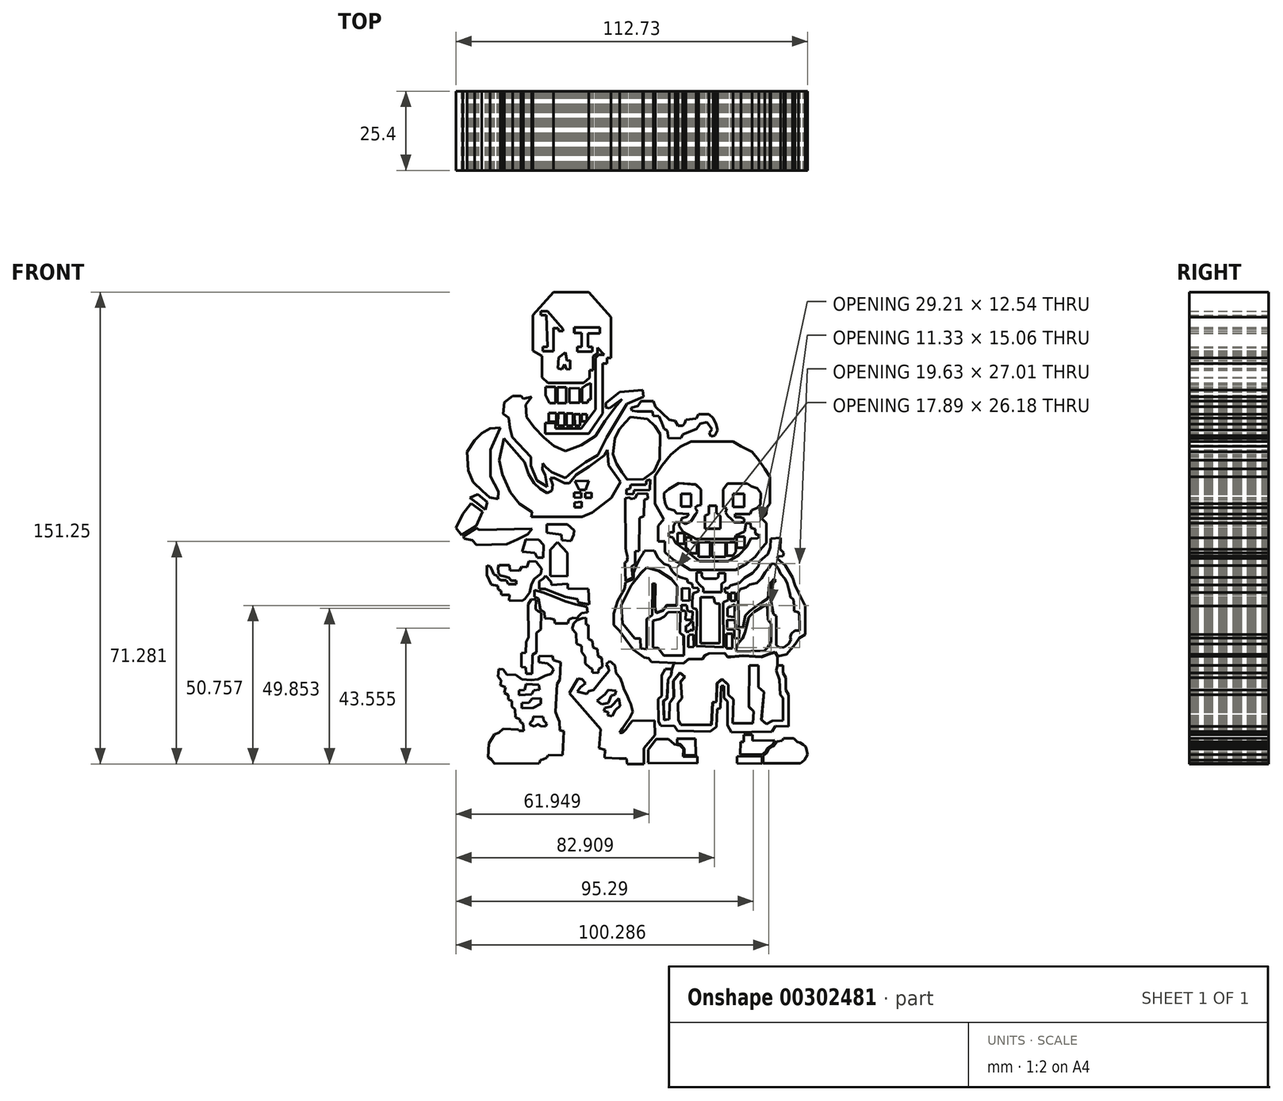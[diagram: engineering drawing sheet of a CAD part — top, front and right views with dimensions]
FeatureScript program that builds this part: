
annotation { "Feature Type Name" : "Feature", "Feature Type Description" : "" }
export const myFeature = defineFeature(function(context is Context, id is Id, definition is map)
    precondition{}
    {
        {
            var Q0;
            Q0=qCreatedBy(makeId("Front.planeOp"),FACE);
            var sketch = newSketch(context, id + "F0", { "sketchPlane" : qUnion([Q0])});
            skLineSegment(sketch, "E0", {"start": v(-16.69, 75) * mm, "end": v(-28, 75) * mm});
            skLineSegment(sketch, "E1", {"start": v(-28, 75) * mm, "end": v(-34.64, 67.58) * mm});
            skLineSegment(sketch, "E2", {"start": v(-34.64, 67.58) * mm, "end": v(-34.64, 56.21) * mm});
            skLineSegment(sketch, "E3", {"start": v(-34.64, 56.21) * mm, "end": v(-31.66, 54.56) * mm});
            skLineSegment(sketch, "E4", {"start": v(-31.66, 54.56) * mm, "end": v(-31.66, 47.68) * mm});
            skLineSegment(sketch, "E5", {"start": v(-31.66, 47.68) * mm, "end": v(-29.8, 45.82) * mm});
            skLineSegment(sketch, "E6", {"start": v(-29.8, 45.82) * mm, "end": v(-18.33, 45.82) * mm});
            skLineSegment(sketch, "E7", {"start": v(-18.33, 45.82) * mm, "end": v(-16.52, 47.56) * mm});
            skLineSegment(sketch, "E8", {"start": v(-16.52, 47.56) * mm, "end": v(-16.52, 49.98) * mm});
            skLineSegment(sketch, "E9", {"start": v(-16.52, 49.98) * mm, "end": v(-15.38, 49.98) * mm});
            skLineSegment(sketch, "E10", {"start": v(-15.38, 49.98) * mm, "end": v(-15.38, 54.44) * mm});
            skLineSegment(sketch, "E11", {"start": v(-15.38, 54.44) * mm, "end": v(-14.6, 54.44) * mm});
            skLineSegment(sketch, "E12", {"start": v(-14.6, 54.44) * mm, "end": v(-14.6, 37.31) * mm});
            skLineSegment(sketch, "E13", {"start": v(-14.6, 37.31) * mm, "end": v(-19.11, 31.33) * mm});
            skLineSegment(sketch, "E14", {"start": v(-19.11, 31.33) * mm, "end": v(-27.42, 31.33) * mm});
            skLineSegment(sketch, "E15", {"start": v(-27.42, 31.33) * mm, "end": v(-27.42, 32.99) * mm});
            skLineSegment(sketch, "E16", {"start": v(-27.42, 32.99) * mm, "end": v(-30.74, 32.99) * mm});
            skLineSegment(sketch, "E17", {"start": v(-30.74, 32.99) * mm, "end": v(-30.74, 29.66) * mm});
            skLineSegment(sketch, "E18", {"start": v(-30.74, 29.66) * mm, "end": v(-16.75, 29.66) * mm});
            skLineSegment(sketch, "E19", {"start": v(-16.75, 29.66) * mm, "end": v(-12.34, 36.12) * mm});
            skLineSegment(sketch, "E20", {"start": v(-12.34, 36.12) * mm, "end": v(-12.34, 52.15) * mm});
            skLineSegment(sketch, "E21", {"start": v(-12.34, 52.15) * mm, "end": v(-10.87, 52.15) * mm});
            skLineSegment(sketch, "E22", {"start": v(-10.87, 52.15) * mm, "end": v(-10.87, 53.88) * mm});
            skLineSegment(sketch, "E23", {"start": v(-10.87, 53.88) * mm, "end": v(-9.6, 53.88) * mm});
            skLineSegment(sketch, "E24", {"start": v(-9.6, 53.88) * mm, "end": v(-9.6, 66.91) * mm});
            skLineSegment(sketch, "E25", {"start": v(-9.6, 66.91) * mm, "end": v(-16.69, 75) * mm});
            skLineSegment(sketch, "E26", {"start": v(-29.94, 57.5) * mm, "end": v(-31.48, 57.5) * mm});
            skLineSegment(sketch, "E27", {"start": v(-31.48, 57.5) * mm, "end": v(-31.48, 56.06) * mm});
            skLineSegment(sketch, "E28", {"start": v(-31.48, 56.06) * mm, "end": v(-28.08, 56.06) * mm});
            skLineSegment(sketch, "E29", {"start": v(-28.08, 56.06) * mm, "end": v(-28.08, 63.46) * mm});
            skLineSegment(sketch, "E30", {"start": v(-28.08, 63.46) * mm, "end": v(-26.52, 63.46) * mm});
            skLineSegment(sketch, "E31", {"start": v(-26.52, 63.46) * mm, "end": v(-26.44, 62.47) * mm});
            skLineSegment(sketch, "E32", {"start": v(-26.44, 62.47) * mm, "end": v(-24.97, 62.47) * mm});
            skLineSegment(sketch, "E33", {"start": v(-24.97, 62.47) * mm, "end": v(-24.97, 63.1) * mm});
            skLineSegment(sketch, "E34", {"start": v(-24.97, 63.1) * mm, "end": v(-29.96, 68.9) * mm});
            skLineSegment(sketch, "E35", {"start": v(-29.96, 68.9) * mm, "end": v(-32.1, 68.9) * mm});
            skLineSegment(sketch, "E36", {"start": v(-32.1, 68.9) * mm, "end": v(-32.1, 67.6) * mm});
            skLineSegment(sketch, "E37", {"start": v(-32.1, 67.6) * mm, "end": v(-30.3, 67.6) * mm});
            skLineSegment(sketch, "E38", {"start": v(-30.3, 67.6) * mm, "end": v(-29.94, 57.5) * mm});
            skLineSegment(sketch, "E39", {"start": v(-21.37, 63.41) * mm, "end": v(-21.37, 61.88) * mm});
            skLineSegment(sketch, "E40", {"start": v(-21.37, 61.88) * mm, "end": v(-19.04, 61.88) * mm});
            skLineSegment(sketch, "E41", {"start": v(-19.04, 61.88) * mm, "end": v(-19.04, 57.4) * mm});
            skLineSegment(sketch, "E42", {"start": v(-19.04, 57.4) * mm, "end": v(-20.43, 57.4) * mm});
            skLineSegment(sketch, "E43", {"start": v(-20.43, 57.4) * mm, "end": v(-20.43, 55.93) * mm});
            skLineSegment(sketch, "E44", {"start": v(-20.43, 55.93) * mm, "end": v(-15.62, 55.93) * mm});
            skLineSegment(sketch, "E45", {"start": v(-15.62, 55.93) * mm, "end": v(-15.62, 57.47) * mm});
            skLineSegment(sketch, "E46", {"start": v(-15.62, 57.47) * mm, "end": v(-16.99, 57.47) * mm});
            skLineSegment(sketch, "E47", {"start": v(-16.99, 57.47) * mm, "end": v(-16.99, 61.76) * mm});
            skLineSegment(sketch, "E48", {"start": v(-16.99, 61.76) * mm, "end": v(-13.12, 61.76) * mm});
            skLineSegment(sketch, "E49", {"start": v(-13.12, 61.76) * mm, "end": v(-13.12, 63.61) * mm});
            skLineSegment(sketch, "E50", {"start": v(-13.12, 63.61) * mm, "end": v(-21.37, 63.61) * mm});
            skLineSegment(sketch, "E51", {"start": v(-21.37, 63.61) * mm, "end": v(-21.37, 63.41) * mm});
            skLineSegment(sketch, "E52", {"start": v(-24.17, 55.7) * mm, "end": v(-23.76, 52.96) * mm});
            skLineSegment(sketch, "E53", {"start": v(-23.76, 52.96) * mm, "end": v(-22.73, 53.11) * mm});
            skLineSegment(sketch, "E54", {"start": v(-22.73, 53.11) * mm, "end": v(-22.73, 50.35) * mm});
            skLineSegment(sketch, "E55", {"start": v(-22.73, 50.35) * mm, "end": v(-23.86, 50.22) * mm});
            skLineSegment(sketch, "E56", {"start": v(-23.86, 50.22) * mm, "end": v(-24.5, 51.88) * mm});
            skLineSegment(sketch, "E57", {"start": v(-24.5, 51.88) * mm, "end": v(-25.32, 50.18) * mm});
            skLineSegment(sketch, "E58", {"start": v(-25.32, 50.18) * mm, "end": v(-26.67, 50.56) * mm});
            skLineSegment(sketch, "E59", {"start": v(-26.67, 50.56) * mm, "end": v(-26.33, 54.04) * mm});
            skLineSegment(sketch, "E60", {"start": v(-26.33, 54.04) * mm, "end": v(-24.17, 55.7) * mm});
            skLineSegment(sketch, "E61", {"start": v(-13.91, 57.13) * mm, "end": v(-13.91, 54.9) * mm});
            skLineSegment(sketch, "E62", {"start": v(-13.91, 54.9) * mm, "end": v(-11.83, 54.86) * mm});
            skLineSegment(sketch, "E63", {"start": v(-11.83, 54.86) * mm, "end": v(-13.91, 57.13) * mm});
            skLineSegment(sketch, "E64", {"start": v(-15.38, 54.44) * mm, "end": v(-13.91, 55.31) * mm});
            skLineSegment(sketch, "E65", {"start": v(-13.91, 55.31) * mm, "end": v(-13.91, 54.9) * mm});
            skLineSegment(sketch, "E66", {"start": v(-14.6, 53.9) * mm, "end": v(-13.52, 54.89) * mm});
            skLineSegment(sketch, "E67", {"start": v(-13.52, 54.89) * mm, "end": v(-13.91, 54.9) * mm});
            skLineSegment(sketch, "E68", {"start": v(-30.64, 44.3) * mm, "end": v(-30.64, 41.9) * mm});
            skLineSegment(sketch, "E69", {"start": v(-30.64, 41.9) * mm, "end": v(-29.36, 39.43) * mm});
            skLineSegment(sketch, "E70", {"start": v(-29.36, 39.43) * mm, "end": v(-27.4, 39.43) * mm});
            skLineSegment(sketch, "E71", {"start": v(-27.4, 39.43) * mm, "end": v(-27.4, 44.55) * mm});
            skLineSegment(sketch, "E72", {"start": v(-27.4, 44.55) * mm, "end": v(-30.64, 44.55) * mm});
            skLineSegment(sketch, "E73", {"start": v(-30.64, 44.55) * mm, "end": v(-30.64, 44.3) * mm});
            skLineSegment(sketch, "E74", {"start": v(-26.73, 44.47) * mm, "end": v(-26.73, 39.36) * mm});
            skLineSegment(sketch, "E75", {"start": v(-26.73, 39.36) * mm, "end": v(-23.91, 39.36) * mm});
            skLineSegment(sketch, "E76", {"start": v(-23.91, 39.36) * mm, "end": v(-23.91, 44.44) * mm});
            skLineSegment(sketch, "E77", {"start": v(-23.91, 44.44) * mm, "end": v(-26.73, 44.47) * mm});
            skLineSegment(sketch, "E78", {"start": v(-22.96, 44.18) * mm, "end": v(-22.96, 39.55) * mm});
            skLineSegment(sketch, "E79", {"start": v(-22.96, 39.55) * mm, "end": v(-19.7, 39.55) * mm});
            skLineSegment(sketch, "E80", {"start": v(-19.7, 39.55) * mm, "end": v(-19.7, 44.15) * mm});
            skLineSegment(sketch, "E81", {"start": v(-19.7, 44.15) * mm, "end": v(-22.96, 44.18) * mm});
            skLineSegment(sketch, "E82", {"start": v(-18.87, 44.28) * mm, "end": v(-18.87, 39.55) * mm});
            skLineSegment(sketch, "E83", {"start": v(-18.87, 39.55) * mm, "end": v(-17.17, 39.55) * mm});
            skLineSegment(sketch, "E84", {"start": v(-17.17, 39.55) * mm, "end": v(-16.82, 40.54) * mm});
            skLineSegment(sketch, "E85", {"start": v(-16.82, 40.54) * mm, "end": v(-16.15, 40.54) * mm});
            skLineSegment(sketch, "E86", {"start": v(-16.15, 40.54) * mm, "end": v(-16.15, 45.78) * mm});
            skLineSegment(sketch, "E87", {"start": v(-16.15, 45.78) * mm, "end": v(-17.5, 45.27) * mm});
            skLineSegment(sketch, "E88", {"start": v(-17.5, 45.27) * mm, "end": v(-18.87, 44.28) * mm});
            skLineSegment(sketch, "E89", {"start": v(-29.52, 33.48) * mm, "end": v(-29.52, 36.2) * mm});
            skLineSegment(sketch, "E90", {"start": v(-29.52, 36.2) * mm, "end": v(-27.18, 36.2) * mm});
            skLineSegment(sketch, "E91", {"start": v(-27.18, 36.2) * mm, "end": v(-27.18, 33.48) * mm});
            skLineSegment(sketch, "E92", {"start": v(-27.18, 33.48) * mm, "end": v(-29.52, 33.48) * mm});
            skLineSegment(sketch, "E93", {"start": v(-26.62, 32.2) * mm, "end": v(-24.53, 32.2) * mm});
            skLineSegment(sketch, "E94", {"start": v(-24.53, 32.2) * mm, "end": v(-24.53, 36.2) * mm});
            skLineSegment(sketch, "E95", {"start": v(-24.53, 36.2) * mm, "end": v(-26.54, 36.2) * mm});
            skLineSegment(sketch, "E96", {"start": v(-26.54, 36.2) * mm, "end": v(-26.62, 32.2) * mm});
            skLineSegment(sketch, "E97", {"start": v(-23.9, 32.2) * mm, "end": v(-21.85, 32.2) * mm});
            skLineSegment(sketch, "E98", {"start": v(-21.85, 32.2) * mm, "end": v(-21.85, 36.03) * mm});
            skLineSegment(sketch, "E99", {"start": v(-21.85, 36.03) * mm, "end": v(-23.85, 36.03) * mm});
            skLineSegment(sketch, "E100", {"start": v(-23.85, 36.03) * mm, "end": v(-23.9, 32.2) * mm});
            skLineSegment(sketch, "E101", {"start": v(-21.17, 32.15) * mm, "end": v(-19.55, 32.15) * mm});
            skLineSegment(sketch, "E102", {"start": v(-19.55, 32.15) * mm, "end": v(-19.55, 35.86) * mm});
            skLineSegment(sketch, "E103", {"start": v(-19.55, 35.86) * mm, "end": v(-21.25, 35.86) * mm});
            skLineSegment(sketch, "E104", {"start": v(-21.25, 35.86) * mm, "end": v(-21.17, 32.15) * mm});
            skLineSegment(sketch, "E105", {"start": v(-19.03, 35.57) * mm, "end": v(-19.03, 33.6) * mm});
            skLineSegment(sketch, "E106", {"start": v(-19.03, 33.6) * mm, "end": v(-17.4, 33.6) * mm});
            skLineSegment(sketch, "E107", {"start": v(-17.4, 33.6) * mm, "end": v(-17.4, 35.86) * mm});
            skLineSegment(sketch, "E108", {"start": v(-17.4, 35.86) * mm, "end": v(-19.03, 35.86) * mm});
            skLineSegment(sketch, "E109", {"start": v(-19.03, 35.86) * mm, "end": v(-19.03, 35.57) * mm});
            skLineSegment(sketch, "E110", {"start": v(-35.03, 41.37) * mm, "end": v(-36.94, 38.85) * mm});
            skLineSegment(sketch, "E111", {"start": v(-36.94, 38.85) * mm, "end": v(-36.63, 34.91) * mm});
            skLineSegment(sketch, "E112", {"start": v(-36.63, 34.91) * mm, "end": v(-34.2, 31.65) * mm});
            skLineSegment(sketch, "E113", {"start": v(-34.2, 31.65) * mm, "end": v(-31.08, 28.3) * mm});
            skLineSegment(sketch, "E114", {"start": v(-31.08, 28.3) * mm, "end": v(-27.97, 25.64) * mm});
            skLineSegment(sketch, "E115", {"start": v(-27.97, 25.64) * mm, "end": v(-24.17, 24.05) * mm});
            skLineSegment(sketch, "E116", {"start": v(-24.17, 24.05) * mm, "end": v(-19.15, 25.87) * mm});
            skLineSegment(sketch, "E117", {"start": v(-19.15, 25.87) * mm, "end": v(-14.52, 28.83) * mm});
            skLineSegment(sketch, "E118", {"start": v(-14.52, 28.83) * mm, "end": v(-11.48, 33.7) * mm});
            skLineSegment(sketch, "E119", {"start": v(-11.48, 33.7) * mm, "end": v(-7.76, 38.71) * mm});
            skLineSegment(sketch, "E120", {"start": v(-7.76, 38.71) * mm, "end": v(-6.09, 40.61) * mm});
            skLineSegment(sketch, "E121", {"start": v(-6.09, 40.61) * mm, "end": v(-10.11, 37.72) * mm});
            skLineSegment(sketch, "E122", {"start": v(-10.11, 37.72) * mm, "end": v(-11.33, 38.03) * mm});
            skLineSegment(sketch, "E123", {"start": v(-11.33, 38.03) * mm, "end": v(-11.33, 39.4) * mm});
            skLineSegment(sketch, "E124", {"start": v(-11.33, 39.4) * mm, "end": v(-6.85, 42.97) * mm});
            skLineSegment(sketch, "E125", {"start": v(-6.85, 42.97) * mm, "end": v(0.6, 43.57) * mm});
            skLineSegment(sketch, "E126", {"start": v(0.6, 43.57) * mm, "end": v(0.77, 41.46) * mm});
            skLineSegment(sketch, "E127", {"start": v(0.77, 41.46) * mm, "end": v(-4.5, 39.1) * mm});
            skLineSegment(sketch, "E128", {"start": v(-4.5, 39.1) * mm, "end": v(-10.96, 28.4) * mm});
            skLineSegment(sketch, "E129", {"start": v(-10.96, 28.4) * mm, "end": v(-13.86, 22.7) * mm});
            skLineSegment(sketch, "E130", {"start": v(-13.86, 22.7) * mm, "end": v(-17.73, 20.45) * mm});
            skLineSegment(sketch, "E131", {"start": v(-17.73, 20.45) * mm, "end": v(-21.97, 17.44) * mm});
            skLineSegment(sketch, "E132", {"start": v(-21.97, 17.44) * mm, "end": v(-24.18, 15.4) * mm});
            skLineSegment(sketch, "E133", {"start": v(-24.18, 15.4) * mm, "end": v(-28.69, 17.33) * mm});
            skLineSegment(sketch, "E134", {"start": v(-28.69, 17.33) * mm, "end": v(-30.62, 18.95) * mm});
            skLineSegment(sketch, "E135", {"start": v(-30.62, 18.95) * mm, "end": v(-31.43, 20.08) * mm});
            skLineSegment(sketch, "E136", {"start": v(-31.43, 20.08) * mm, "end": v(-31.55, 18.1) * mm});
            skLineSegment(sketch, "E137", {"start": v(-31.55, 18.1) * mm, "end": v(-30.65, 16.38) * mm});
            skLineSegment(sketch, "E138", {"start": v(-30.65, 16.38) * mm, "end": v(-30.1, 12.59) * mm});
            skLineSegment(sketch, "E139", {"start": v(-30.1, 12.59) * mm, "end": v(-33.36, 14.66) * mm});
            skLineSegment(sketch, "E140", {"start": v(-33.36, 14.66) * mm, "end": v(-35.26, 19.36) * mm});
            skLineSegment(sketch, "E141", {"start": v(-35.26, 19.36) * mm, "end": v(-35.26, 22.16) * mm});
            skLineSegment(sketch, "E142", {"start": v(-35.26, 22.16) * mm, "end": v(-41.3, 28.49) * mm});
            skLineSegment(sketch, "E143", {"start": v(-41.3, 28.49) * mm, "end": v(-42.03, 31.47) * mm});
            skLineSegment(sketch, "E144", {"start": v(-42.03, 31.47) * mm, "end": v(-42.4, 34.72) * mm});
            skLineSegment(sketch, "E145", {"start": v(-42.4, 34.72) * mm, "end": v(-44.2, 35.99) * mm});
            skLineSegment(sketch, "E146", {"start": v(-44.2, 35.99) * mm, "end": v(-43.75, 39.6) * mm});
            skLineSegment(sketch, "E147", {"start": v(-43.75, 39.6) * mm, "end": v(-41.13, 41.68) * mm});
            skLineSegment(sketch, "E148", {"start": v(-41.13, 41.68) * mm, "end": v(-38.42, 41.68) * mm});
            skLineSegment(sketch, "E149", {"start": v(-38.42, 41.68) * mm, "end": v(-37.7, 40.78) * mm});
            skLineSegment(sketch, "E150", {"start": v(-37.7, 40.78) * mm, "end": v(-35.03, 41.37) * mm});
            skLineSegment(sketch, "E151", {"start": v(-3.09, 37.93) * mm, "end": v(-0.94, 38.5) * mm});
            skLineSegment(sketch, "E152", {"start": v(-0.94, 38.5) * mm, "end": v(0, 40.09) * mm});
            skLineSegment(sketch, "E153", {"start": v(0, 40.09) * mm, "end": v(3.94, 40.09) * mm});
            skLineSegment(sketch, "E154", {"start": v(3.94, 40.09) * mm, "end": v(4.66, 38.3) * mm});
            skLineSegment(sketch, "E155", {"start": v(4.66, 38.3) * mm, "end": v(9.1, 34.06) * mm});
            skLineSegment(sketch, "E156", {"start": v(9.1, 34.06) * mm, "end": v(10.9, 33.7) * mm});
            skLineSegment(sketch, "E157", {"start": v(10.9, 33.7) * mm, "end": v(11.83, 32.13) * mm});
            skLineSegment(sketch, "E158", {"start": v(11.83, 32.13) * mm, "end": v(13.4, 32.2) * mm});
            skLineSegment(sketch, "E159", {"start": v(13.4, 32.2) * mm, "end": v(13.98, 32.91) * mm});
            skLineSegment(sketch, "E160", {"start": v(13.98, 32.91) * mm, "end": v(14.4, 34.06) * mm});
            skLineSegment(sketch, "E161", {"start": v(14.4, 34.06) * mm, "end": v(17.64, 34.42) * mm});
            skLineSegment(sketch, "E162", {"start": v(17.64, 34.42) * mm, "end": v(18.5, 35.78) * mm});
            skLineSegment(sketch, "E163", {"start": v(18.5, 35.78) * mm, "end": v(21.72, 35.78) * mm});
            skLineSegment(sketch, "E164", {"start": v(21.72, 35.78) * mm, "end": v(23.09, 34.56) * mm});
            skLineSegment(sketch, "E165", {"start": v(23.09, 34.56) * mm, "end": v(24.02, 32.63) * mm});
            skLineSegment(sketch, "E166", {"start": v(24.02, 32.63) * mm, "end": v(24.6, 30.76) * mm});
            skLineSegment(sketch, "E167", {"start": v(24.6, 30.76) * mm, "end": v(23.66, 29.04) * mm});
            skLineSegment(sketch, "E168", {"start": v(23.66, 29.04) * mm, "end": v(22.44, 28.76) * mm});
            skLineSegment(sketch, "E169", {"start": v(22.44, 28.76) * mm, "end": v(21.87, 29.83) * mm});
            skLineSegment(sketch, "E170", {"start": v(21.87, 29.83) * mm, "end": v(22.73, 31.05) * mm});
            skLineSegment(sketch, "E171", {"start": v(22.73, 31.05) * mm, "end": v(21.15, 33.34) * mm});
            skLineSegment(sketch, "E172", {"start": v(21.15, 33.34) * mm, "end": v(19, 32.77) * mm});
            skLineSegment(sketch, "E173", {"start": v(19, 32.77) * mm, "end": v(17.78, 31.2) * mm});
            skLineSegment(sketch, "E174", {"start": v(17.78, 31.2) * mm, "end": v(15.05, 30.05) * mm});
            skLineSegment(sketch, "E175", {"start": v(15.05, 30.05) * mm, "end": v(13.4, 29.33) * mm});
            skLineSegment(sketch, "E176", {"start": v(13.4, 29.33) * mm, "end": v(12.83, 28.25) * mm});
            skLineSegment(sketch, "E177", {"start": v(12.83, 28.25) * mm, "end": v(8.81, 28.04) * mm});
            skLineSegment(sketch, "E178", {"start": v(8.81, 28.04) * mm, "end": v(8.38, 30.62) * mm});
            skLineSegment(sketch, "E179", {"start": v(8.38, 30.62) * mm, "end": v(7.38, 31.2) * mm});
            skLineSegment(sketch, "E180", {"start": v(7.38, 31.2) * mm, "end": v(6.66, 33.2) * mm});
            skLineSegment(sketch, "E181", {"start": v(6.66, 33.2) * mm, "end": v(5.8, 35.2) * mm});
            skLineSegment(sketch, "E182", {"start": v(5.8, 35.2) * mm, "end": v(3.87, 35.35) * mm});
            skLineSegment(sketch, "E183", {"start": v(3.87, 35.35) * mm, "end": v(3.72, 36.79) * mm});
            skLineSegment(sketch, "E184", {"start": v(3.72, 36.79) * mm, "end": v(-1.22, 36.79) * mm});
            skLineSegment(sketch, "E185", {"start": v(-1.22, 36.79) * mm, "end": v(-2.95, 36.93) * mm});
            skLineSegment(sketch, "E186", {"start": v(-2.95, 36.93) * mm, "end": v(-3.16, 37.8) * mm});
            skLineSegment(sketch, "E187", {"start": v(-3.16, 37.8) * mm, "end": v(-3.09, 37.93) * mm});
            skLineSegment(sketch, "E188", {"start": v(-3.09, 35.2) * mm, "end": v(-5.01, 33.2) * mm});
            skLineSegment(sketch, "E189", {"start": v(-5.01, 33.2) * mm, "end": v(-6.77, 31.12) * mm});
            skLineSegment(sketch, "E190", {"start": v(-6.77, 31.12) * mm, "end": v(-8.4, 28.28) * mm});
            skLineSegment(sketch, "E191", {"start": v(-8.4, 28.28) * mm, "end": v(-8.94, 23) * mm});
            skLineSegment(sketch, "E192", {"start": v(-8.94, 23) * mm, "end": v(-7.85, 20.02) * mm});
            skLineSegment(sketch, "E193", {"start": v(-7.85, 20.02) * mm, "end": v(-6.1, 17.1) * mm});
            skLineSegment(sketch, "E194", {"start": v(-6.1, 17.1) * mm, "end": v(-4.47, 14.87) * mm});
            skLineSegment(sketch, "E195", {"start": v(-4.47, 14.87) * mm, "end": v(0.81, 15.01) * mm});
            skLineSegment(sketch, "E196", {"start": v(0.81, 15.01) * mm, "end": v(4.2, 17.58) * mm});
            skLineSegment(sketch, "E197", {"start": v(4.2, 17.58) * mm, "end": v(5.95, 21.5) * mm});
            skLineSegment(sketch, "E198", {"start": v(5.95, 21.5) * mm, "end": v(6.1, 29.43) * mm});
            skLineSegment(sketch, "E199", {"start": v(6.1, 29.43) * mm, "end": v(4.53, 32.07) * mm});
            skLineSegment(sketch, "E200", {"start": v(4.53, 32.07) * mm, "end": v(2.03, 34.37) * mm});
            skLineSegment(sketch, "E201", {"start": v(2.03, 34.37) * mm, "end": v(-3.38, 34.9) * mm});
            skLineSegment(sketch, "E202", {"start": v(-3.38, 34.9) * mm, "end": v(-5.01, 33.2) * mm});
            skLineSegment(sketch, "E203", {"start": v(-43.86, 28.08) * mm, "end": v(-37.36, 20.49) * mm});
            skLineSegment(sketch, "E204", {"start": v(-37.36, 20.49) * mm, "end": v(-36.1, 16.7) * mm});
            skLineSegment(sketch, "E205", {"start": v(-36.1, 16.7) * mm, "end": v(-34.29, 13.8) * mm});
            skLineSegment(sketch, "E206", {"start": v(-34.29, 13.8) * mm, "end": v(-32.3, 12) * mm});
            skLineSegment(sketch, "E207", {"start": v(-32.3, 12) * mm, "end": v(-30.13, 10.55) * mm});
            skLineSegment(sketch, "E208", {"start": v(-30.13, 10.55) * mm, "end": v(-28.6, 11.27) * mm});
            skLineSegment(sketch, "E209", {"start": v(-28.6, 11.27) * mm, "end": v(-28.32, 13.26) * mm});
            skLineSegment(sketch, "E210", {"start": v(-28.32, 13.26) * mm, "end": v(-29.05, 15.34) * mm});
            skLineSegment(sketch, "E211", {"start": v(-29.05, 15.34) * mm, "end": v(-27.78, 15.34) * mm});
            skLineSegment(sketch, "E212", {"start": v(-27.78, 15.34) * mm, "end": v(-24.53, 13.7) * mm});
            skLineSegment(sketch, "E213", {"start": v(-24.53, 13.7) * mm, "end": v(-23, 13.7) * mm});
            skLineSegment(sketch, "E214", {"start": v(-23, 13.7) * mm, "end": v(-20.82, 16.42) * mm});
            skLineSegment(sketch, "E215", {"start": v(-20.82, 16.42) * mm, "end": v(-16.67, 19.13) * mm});
            skLineSegment(sketch, "E216", {"start": v(-16.67, 19.13) * mm, "end": v(-11.79, 22.65) * mm});
            skLineSegment(sketch, "E217", {"start": v(-11.79, 22.65) * mm, "end": v(-10.8, 24.37) * mm});
            skLineSegment(sketch, "E218", {"start": v(-10.8, 24.37) * mm, "end": v(-10.43, 19.4) * mm});
            skLineSegment(sketch, "E219", {"start": v(-10.43, 19.4) * mm, "end": v(-6.55, 14.16) * mm});
            skLineSegment(sketch, "E220", {"start": v(-6.55, 14.16) * mm, "end": v(-9.53, 9.1) * mm});
            skLineSegment(sketch, "E221", {"start": v(-9.53, 9.1) * mm, "end": v(-15.65, 4.36) * mm});
            skLineSegment(sketch, "E222", {"start": v(-15.65, 4.36) * mm, "end": v(-18.9, 2.9) * mm});
            skLineSegment(sketch, "E223", {"start": v(-18.9, 2.9) * mm, "end": v(-35.1, 2.9) * mm});
            skLineSegment(sketch, "E224", {"start": v(-35.1, 2.9) * mm, "end": v(-34.92, 4.53) * mm});
            skLineSegment(sketch, "E225", {"start": v(-34.92, 4.53) * mm, "end": v(-39.02, 7.09) * mm});
            skLineSegment(sketch, "E226", {"start": v(-39.02, 7.09) * mm, "end": v(-41.92, 10.84) * mm});
            skLineSegment(sketch, "E227", {"start": v(-41.92, 10.84) * mm, "end": v(-44.47, 16.55) * mm});
            skLineSegment(sketch, "E228", {"start": v(-44.47, 16.55) * mm, "end": v(-45.5, 21.07) * mm});
            skLineSegment(sketch, "E229", {"start": v(-45.5, 21.07) * mm, "end": v(-43.86, 28.08) * mm});
            skLineSegment(sketch, "E230", {"start": v(-20.94, 13.9) * mm, "end": v(-19.74, 11.6) * mm});
            skLineSegment(sketch, "E231", {"start": v(-19.74, 11.6) * mm, "end": v(-17.78, 11.6) * mm});
            skLineSegment(sketch, "E232", {"start": v(-17.78, 11.6) * mm, "end": v(-16.67, 14.5) * mm});
            skLineSegment(sketch, "E233", {"start": v(-16.67, 14.5) * mm, "end": v(-21.2, 14.42) * mm});
            skLineSegment(sketch, "E234", {"start": v(-21.2, 14.42) * mm, "end": v(-20.94, 13.9) * mm});
            skLineSegment(sketch, "E235", {"start": v(-21.4, 10.65) * mm, "end": v(-21.4, 9.15) * mm});
            skLineSegment(sketch, "E236", {"start": v(-21.4, 9.15) * mm, "end": v(-19.16, 9) * mm});
            skLineSegment(sketch, "E237", {"start": v(-19.16, 9) * mm, "end": v(-19.16, 10.65) * mm});
            skLineSegment(sketch, "E238", {"start": v(-19.16, 10.65) * mm, "end": v(-21.4, 10.65) * mm});
            skLineSegment(sketch, "E239", {"start": v(-17.82, 10.59) * mm, "end": v(-17.82, 9.05) * mm});
            skLineSegment(sketch, "E240", {"start": v(-17.82, 9.05) * mm, "end": v(-15.9, 9.05) * mm});
            skLineSegment(sketch, "E241", {"start": v(-15.9, 9.05) * mm, "end": v(-15.9, 10.65) * mm});
            skLineSegment(sketch, "E242", {"start": v(-15.9, 10.65) * mm, "end": v(-17.82, 10.59) * mm});
            skLineSegment(sketch, "E243", {"start": v(-21.27, 7.52) * mm, "end": v(-21.27, 5.96) * mm});
            skLineSegment(sketch, "E244", {"start": v(-21.27, 5.96) * mm, "end": v(-18.97, 5.96) * mm});
            skLineSegment(sketch, "E245", {"start": v(-18.97, 5.96) * mm, "end": v(-18.97, 7.71) * mm});
            skLineSegment(sketch, "E246", {"start": v(-18.97, 7.71) * mm, "end": v(-21.27, 7.52) * mm});
            skLineSegment(sketch, "E247", {"start": v(-45.15, 31.32) * mm, "end": v(-48.21, 24.4) * mm});
            skLineSegment(sketch, "E248", {"start": v(-48.21, 24.4) * mm, "end": v(-48.21, 15.87) * mm});
            skLineSegment(sketch, "E249", {"start": v(-48.21, 15.87) * mm, "end": v(-45.64, 11.04) * mm});
            skLineSegment(sketch, "E250", {"start": v(-45.64, 11.04) * mm, "end": v(-45.8, 8.63) * mm});
            skLineSegment(sketch, "E251", {"start": v(-45.8, 8.63) * mm, "end": v(-48.53, 9.1) * mm});
            skLineSegment(sketch, "E252", {"start": v(-48.53, 9.1) * mm, "end": v(-50.79, 11.2) * mm});
            skLineSegment(sketch, "E253", {"start": v(-50.79, 11.2) * mm, "end": v(-53.85, 14.1) * mm});
            skLineSegment(sketch, "E254", {"start": v(-53.85, 14.1) * mm, "end": v(-55.38, 17.8) * mm});
            skLineSegment(sketch, "E255", {"start": v(-55.38, 17.8) * mm, "end": v(-55.7, 23.76) * mm});
            skLineSegment(sketch, "E256", {"start": v(-55.7, 23.76) * mm, "end": v(-53.35, 27.5) * mm});
            skLineSegment(sketch, "E257", {"start": v(-53.35, 27.5) * mm, "end": v(-50.97, 29.74) * mm});
            skLineSegment(sketch, "E258", {"start": v(-50.97, 29.74) * mm, "end": v(-48.4, 31.3) * mm});
            skLineSegment(sketch, "E259", {"start": v(-48.4, 31.3) * mm, "end": v(-45, 31.49) * mm});
            skLineSegment(sketch, "E260", {"start": v(-45, 31.49) * mm, "end": v(-45.15, 31.32) * mm});
            skLineSegment(sketch, "E261", {"start": v(-54.84, 9.08) * mm, "end": v(-52.57, 7.43) * mm});
            skLineSegment(sketch, "E262", {"start": v(-52.57, 7.43) * mm, "end": v(-49.9, 5.21) * mm});
            skLineSegment(sketch, "E263", {"start": v(-49.9, 5.21) * mm, "end": v(-49.27, 7.6) * mm});
            skLineSegment(sketch, "E264", {"start": v(-49.27, 7.6) * mm, "end": v(-52.34, 10.17) * mm});
            skLineSegment(sketch, "E265", {"start": v(-52.34, 10.17) * mm, "end": v(-54.84, 9.08) * mm});
            skLineSegment(sketch, "E266", {"start": v(-54.44, 7.23) * mm, "end": v(-50.8, 4.6) * mm});
            skLineSegment(sketch, "E267", {"start": v(-50.8, 4.6) * mm, "end": v(-52.83, 0) * mm});
            skLineSegment(sketch, "E268", {"start": v(-52.83, 0) * mm, "end": v(-57.45, -2.87) * mm});
            skLineSegment(sketch, "E269", {"start": v(-57.45, -2.87) * mm, "end": v(-59.33, -0.67) * mm});
            skLineSegment(sketch, "E270", {"start": v(-59.33, -0.67) * mm, "end": v(-57.13, 3.8) * mm});
            skLineSegment(sketch, "E271", {"start": v(-57.13, 3.8) * mm, "end": v(-54.44, 7.23) * mm});
            skLineSegment(sketch, "E272", {"start": v(-56.92, -3.3) * mm, "end": v(-52.62, -0.61) * mm});
            skLineSegment(sketch, "E273", {"start": v(-52.62, -0.61) * mm, "end": v(-51.87, -1.26) * mm});
            skLineSegment(sketch, "E274", {"start": v(-51.87, -1.26) * mm, "end": v(-34.89, -0.83) * mm});
            skLineSegment(sketch, "E275", {"start": v(-34.89, -0.83) * mm, "end": v(-36.23, -2.66) * mm});
            skLineSegment(sketch, "E276", {"start": v(-36.23, -2.66) * mm, "end": v(-39.56, -4.27) * mm});
            skLineSegment(sketch, "E277", {"start": v(-39.56, -4.27) * mm, "end": v(-43.05, -5.88) * mm});
            skLineSegment(sketch, "E278", {"start": v(-43.05, -5.88) * mm, "end": v(-52.62, -6.1) * mm});
            skLineSegment(sketch, "E279", {"start": v(-52.62, -6.1) * mm, "end": v(-54.07, -4.48) * mm});
            skLineSegment(sketch, "E280", {"start": v(-54.07, -4.48) * mm, "end": v(-56.65, -4.05) * mm});
            skLineSegment(sketch, "E281", {"start": v(-56.65, -4.05) * mm, "end": v(-56.92, -3.3) * mm});
            skLineSegment(sketch, "E282", {"start": v(-36.96, -4.31) * mm, "end": v(-38, -8.25) * mm});
            skLineSegment(sketch, "E283", {"start": v(-38, -8.25) * mm, "end": v(-33.98, -8.58) * mm});
            skLineSegment(sketch, "E284", {"start": v(-33.98, -8.58) * mm, "end": v(-33.26, -10.19) * mm});
            skLineSegment(sketch, "E285", {"start": v(-33.26, -10.19) * mm, "end": v(-31.33, -10.19) * mm});
            skLineSegment(sketch, "E286", {"start": v(-31.33, -10.19) * mm, "end": v(-31.25, -6.08) * mm});
            skLineSegment(sketch, "E287", {"start": v(-31.25, -6.08) * mm, "end": v(-32.7, -4.47) * mm});
            skLineSegment(sketch, "E288", {"start": v(-32.7, -4.47) * mm, "end": v(-36.8, -4.31) * mm});
            skLineSegment(sketch, "E289", {"start": v(-36.8, -4.31) * mm, "end": v(-36.96, -4.31) * mm});
            skLineSegment(sketch, "E290", {"start": v(-30.2, 0.54) * mm, "end": v(-30.2, -2.15) * mm});
            skLineSegment(sketch, "E291", {"start": v(-30.2, -2.15) * mm, "end": v(-25.53, -2.8) * mm});
            skLineSegment(sketch, "E292", {"start": v(-25.53, -2.8) * mm, "end": v(-25.38, -4.58) * mm});
            skLineSegment(sketch, "E293", {"start": v(-25.38, -4.58) * mm, "end": v(-22.49, -4.79) * mm});
            skLineSegment(sketch, "E294", {"start": v(-22.49, -4.79) * mm, "end": v(-21.52, -2.76) * mm});
            skLineSegment(sketch, "E295", {"start": v(-21.52, -2.76) * mm, "end": v(-21.37, -1.39) * mm});
            skLineSegment(sketch, "E296", {"start": v(-21.37, -1.39) * mm, "end": v(-23.6, 0.49) * mm});
            skLineSegment(sketch, "E297", {"start": v(-23.6, 0.49) * mm, "end": v(-30.2, 0.54) * mm});
            skLineSegment(sketch, "E298", {"start": v(-29, -7.43) * mm, "end": v(-29, -15.95) * mm});
            skLineSegment(sketch, "E299", {"start": v(-29, -15.95) * mm, "end": v(-23.65, -16.05) * mm});
            skLineSegment(sketch, "E300", {"start": v(-23.65, -16.05) * mm, "end": v(-23.55, -8.58) * mm});
            skLineSegment(sketch, "E301", {"start": v(-23.55, -8.58) * mm, "end": v(-26.71, -5.23) * mm});
            skLineSegment(sketch, "E302", {"start": v(-26.71, -5.23) * mm, "end": v(-28.91, -7.43) * mm});
            skLineSegment(sketch, "E303", {"start": v(-28.91, -7.43) * mm, "end": v(-29, -7.43) * mm});
            skLineSegment(sketch, "E304", {"start": v(-44.86, -17.4) * mm, "end": v(-43.1, -17.4) * mm});
            skLineSegment(sketch, "E305", {"start": v(-43.1, -17.4) * mm, "end": v(-42.56, -18.68) * mm});
            skLineSegment(sketch, "E306", {"start": v(-42.56, -18.68) * mm, "end": v(-39.92, -18.61) * mm});
            skLineSegment(sketch, "E307", {"start": v(-39.92, -18.61) * mm, "end": v(-39.98, -17.53) * mm});
            skLineSegment(sketch, "E308", {"start": v(-39.98, -17.53) * mm, "end": v(-41.6, -17.46) * mm});
            skLineSegment(sketch, "E309", {"start": v(-41.6, -17.46) * mm, "end": v(-42.28, -16.58) * mm});
            skLineSegment(sketch, "E310", {"start": v(-42.28, -16.58) * mm, "end": v(-43.37, -16.18) * mm});
            skLineSegment(sketch, "E311", {"start": v(-43.37, -16.18) * mm, "end": v(-45, -15.9) * mm});
            skLineSegment(sketch, "E312", {"start": v(-45.4, -12.59) * mm, "end": v(-42.08, -12.59) * mm});
            skLineSegment(sketch, "E313", {"start": v(-42.08, -12.59) * mm, "end": v(-42.01, -14.21) * mm});
            skLineSegment(sketch, "E314", {"start": v(-42.01, -14.21) * mm, "end": v(-38.9, -14.35) * mm});
            skLineSegment(sketch, "E315", {"start": v(-38.9, -14.35) * mm, "end": v(-38.16, -13.06) * mm});
            skLineSegment(sketch, "E316", {"start": v(-38.16, -13.06) * mm, "end": v(-36.53, -13.13) * mm});
            skLineSegment(sketch, "E317", {"start": v(-36.53, -13.13) * mm, "end": v(-35.92, -11.3) * mm});
            skLineSegment(sketch, "E318", {"start": v(-35.92, -11.3) * mm, "end": v(-33.62, -11.37) * mm});
            skLineSegment(sketch, "E319", {"start": v(-33.62, -11.37) * mm, "end": v(-31.86, -13.67) * mm});
            skLineSegment(sketch, "E320", {"start": v(-31.86, -13.67) * mm, "end": v(-32.13, -15.3) * mm});
            skLineSegment(sketch, "E321", {"start": v(-32.13, -15.3) * mm, "end": v(-34.3, -16.99) * mm});
            skLineSegment(sketch, "E322", {"start": v(-34.3, -16.99) * mm, "end": v(-35.1, -18.95) * mm});
            skLineSegment(sketch, "E323", {"start": v(-35.1, -18.95) * mm, "end": v(-35.72, -21.25) * mm});
            skLineSegment(sketch, "E324", {"start": v(-35.72, -21.25) * mm, "end": v(-37.2, -23.28) * mm});
            skLineSegment(sketch, "E325", {"start": v(-37.2, -23.28) * mm, "end": v(-38.09, -24.03) * mm});
            skLineSegment(sketch, "E326", {"start": v(-38.09, -24.03) * mm, "end": v(-42.28, -23.82) * mm});
            skLineSegment(sketch, "E327", {"start": v(-42.28, -23.82) * mm, "end": v(-42.15, -22.06) * mm});
            skLineSegment(sketch, "E328", {"start": v(-42.15, -22.06) * mm, "end": v(-44.65, -22.06) * mm});
            skLineSegment(sketch, "E329", {"start": v(-44.65, -22.06) * mm, "end": v(-44.98, -20.62) * mm});
            skLineSegment(sketch, "E330", {"start": v(-44.98, -20.62) * mm, "end": v(-45.67, -20.37) * mm});
            skLineSegment(sketch, "E331", {"start": v(-45.67, -20.37) * mm, "end": v(-46, -19.16) * mm});
            skLineSegment(sketch, "E332", {"start": v(-46, -19.16) * mm, "end": v(-47.97, -18.75) * mm});
            skLineSegment(sketch, "E333", {"start": v(-47.97, -18.75) * mm, "end": v(-49.36, -15.76) * mm});
            skLineSegment(sketch, "E334", {"start": v(-32.67, -19.63) * mm, "end": v(-32.67, -17.7) * mm});
            skLineSegment(sketch, "E335", {"start": v(-32.67, -17.7) * mm, "end": v(-31.35, -16.85) * mm});
            skLineSegment(sketch, "E336", {"start": v(-31.35, -16.85) * mm, "end": v(-30.62, -16.01) * mm});
            skLineSegment(sketch, "E337", {"start": v(-30.62, -16.01) * mm, "end": v(-28.81, -17.82) * mm});
            skLineSegment(sketch, "E338", {"start": v(-28.81, -17.82) * mm, "end": v(-28.7, -18.9) * mm});
            skLineSegment(sketch, "E339", {"start": v(-28.7, -18.9) * mm, "end": v(-23.45, -18.48) * mm});
            skLineSegment(sketch, "E340", {"start": v(-23.45, -18.48) * mm, "end": v(-23.45, -20.05) * mm});
            skLineSegment(sketch, "E341", {"start": v(-23.45, -20.05) * mm, "end": v(-16.81, -20.11) * mm});
            skLineSegment(sketch, "E342", {"start": v(-16.81, -20.11) * mm, "end": v(-16.63, -25.12) * mm});
            skLineSegment(sketch, "E343", {"start": v(-16.63, -25.12) * mm, "end": v(-20.13, -24.51) * mm});
            skLineSegment(sketch, "E344", {"start": v(-20.13, -24.51) * mm, "end": v(-20.25, -23.43) * mm});
            skLineSegment(sketch, "E345", {"start": v(-20.25, -23.43) * mm, "end": v(-24.23, -22.7) * mm});
            skLineSegment(sketch, "E346", {"start": v(-24.23, -22.7) * mm, "end": v(-28.51, -21.02) * mm});
            skLineSegment(sketch, "E347", {"start": v(-28.51, -21.02) * mm, "end": v(-30.74, -20.11) * mm});
            skLineSegment(sketch, "E348", {"start": v(-30.74, -20.11) * mm, "end": v(-32.59, -20.17) * mm});
            skLineSegment(sketch, "E349", {"start": v(-32.59, -20.17) * mm, "end": v(-32.67, -19.63) * mm});
            skLineSegment(sketch, "E350", {"start": v(-34.08, -20.51) * mm, "end": v(-34.08, -22.75) * mm});
            skLineSegment(sketch, "E351", {"start": v(-34.08, -22.75) * mm, "end": v(-32.83, -23.2) * mm});
            skLineSegment(sketch, "E352", {"start": v(-32.83, -23.2) * mm, "end": v(-32.29, -26.77) * mm});
            skLineSegment(sketch, "E353", {"start": v(-32.29, -26.77) * mm, "end": v(-30.98, -27.6) * mm});
            skLineSegment(sketch, "E354", {"start": v(-30.98, -27.6) * mm, "end": v(-30.79, -29.52) * mm});
            skLineSegment(sketch, "E355", {"start": v(-30.79, -29.52) * mm, "end": v(-28.9, -29.65) * mm});
            skLineSegment(sketch, "E356", {"start": v(-28.9, -29.65) * mm, "end": v(-27.85, -30) * mm});
            skLineSegment(sketch, "E357", {"start": v(-27.85, -30) * mm, "end": v(-27.53, -31.18) * mm});
            skLineSegment(sketch, "E358", {"start": v(-27.53, -31.18) * mm, "end": v(-23.44, -31.24) * mm});
            skLineSegment(sketch, "E359", {"start": v(-23.44, -31.24) * mm, "end": v(-23.02, -29.9) * mm});
            skLineSegment(sketch, "E360", {"start": v(-23.02, -29.9) * mm, "end": v(-21.78, -29.49) * mm});
            skLineSegment(sketch, "E361", {"start": v(-21.78, -29.49) * mm, "end": v(-20.6, -29.58) * mm});
            skLineSegment(sketch, "E362", {"start": v(-20.6, -29.58) * mm, "end": v(-19.73, -28.69) * mm});
            skLineSegment(sketch, "E363", {"start": v(-19.73, -28.69) * mm, "end": v(-19, -27.92) * mm});
            skLineSegment(sketch, "E364", {"start": v(-19, -27.92) * mm, "end": v(-17.18, -27.6) * mm});
            skLineSegment(sketch, "E365", {"start": v(-17.18, -27.6) * mm, "end": v(-17.37, -25.88) * mm});
            skLineSegment(sketch, "E366", {"start": v(-17.37, -25.88) * mm, "end": v(-20.95, -25.15) * mm});
            skLineSegment(sketch, "E367", {"start": v(-20.95, -25.15) * mm, "end": v(-24.4, -24.16) * mm});
            skLineSegment(sketch, "E368", {"start": v(-24.4, -24.16) * mm, "end": v(-27.4, -22.89) * mm});
            skLineSegment(sketch, "E369", {"start": v(-27.4, -22.89) * mm, "end": v(-31.3, -21.26) * mm});
            skLineSegment(sketch, "E370", {"start": v(-31.3, -21.26) * mm, "end": v(-34.08, -20.51) * mm});
            skLineSegment(sketch, "E371", {"start": v(-35.14, -23.44) * mm, "end": v(-33.6, -23.65) * mm});
            skLineSegment(sketch, "E372", {"start": v(-33.6, -23.65) * mm, "end": v(-33.72, -26.62) * mm});
            skLineSegment(sketch, "E373", {"start": v(-33.72, -26.62) * mm, "end": v(-33.05, -27.31) * mm});
            skLineSegment(sketch, "E374", {"start": v(-33.05, -27.31) * mm, "end": v(-31.98, -27.74) * mm});
            skLineSegment(sketch, "E375", {"start": v(-31.98, -27.74) * mm, "end": v(-32.08, -33.15) * mm});
            skLineSegment(sketch, "E376", {"start": v(-32.08, -33.15) * mm, "end": v(-33.44, -34.33) * mm});
            skLineSegment(sketch, "E377", {"start": v(-33.44, -34.33) * mm, "end": v(-33.44, -40.42) * mm});
            skLineSegment(sketch, "E378", {"start": v(-33.44, -40.42) * mm, "end": v(-34.8, -41.19) * mm});
            skLineSegment(sketch, "E379", {"start": v(-34.8, -41.19) * mm, "end": v(-34.95, -47.34) * mm});
            skLineSegment(sketch, "E380", {"start": v(-34.95, -47.34) * mm, "end": v(-36.81, -47.3) * mm});
            skLineSegment(sketch, "E381", {"start": v(-36.81, -47.3) * mm, "end": v(-36.89, -45.33) * mm});
            skLineSegment(sketch, "E382", {"start": v(-36.89, -45.33) * mm, "end": v(-38.3, -45.18) * mm});
            skLineSegment(sketch, "E383", {"start": v(-38.3, -45.18) * mm, "end": v(-38.33, -40.7) * mm});
            skLineSegment(sketch, "E384", {"start": v(-38.33, -40.7) * mm, "end": v(-36.96, -40.58) * mm});
            skLineSegment(sketch, "E385", {"start": v(-36.96, -40.58) * mm, "end": v(-36.85, -37.16) * mm});
            skLineSegment(sketch, "E386", {"start": v(-36.85, -37.16) * mm, "end": v(-36.1, -35.68) * mm});
            skLineSegment(sketch, "E387", {"start": v(-36.1, -35.68) * mm, "end": v(-36.13, -25.16) * mm});
            skLineSegment(sketch, "E388", {"start": v(-36.13, -25.16) * mm, "end": v(-35.14, -23.44) * mm});
            skLineSegment(sketch, "E389", {"start": v(-20.58, -30.2) * mm, "end": v(-21.6, -31.18) * mm});
            skLineSegment(sketch, "E390", {"start": v(-21.6, -31.18) * mm, "end": v(-22.09, -33.03) * mm});
            skLineSegment(sketch, "E391", {"start": v(-22.09, -33.03) * mm, "end": v(-20.76, -34.35) * mm});
            skLineSegment(sketch, "E392", {"start": v(-20.76, -34.35) * mm, "end": v(-20.64, -37.73) * mm});
            skLineSegment(sketch, "E393", {"start": v(-20.64, -37.73) * mm, "end": v(-19.01, -38.4) * mm});
            skLineSegment(sketch, "E394", {"start": v(-19.01, -38.4) * mm, "end": v(-19.07, -40.32) * mm});
            skLineSegment(sketch, "E395", {"start": v(-19.07, -40.32) * mm, "end": v(-17.93, -41.83) * mm});
            skLineSegment(sketch, "E396", {"start": v(-17.93, -41.83) * mm, "end": v(-17.86, -44.07) * mm});
            skLineSegment(sketch, "E397", {"start": v(-17.86, -44.07) * mm, "end": v(-16.38, -45.38) * mm});
            skLineSegment(sketch, "E398", {"start": v(-16.38, -45.38) * mm, "end": v(-15.64, -45.78) * mm});
            skLineSegment(sketch, "E399", {"start": v(-15.64, -45.78) * mm, "end": v(-15.58, -46.92) * mm});
            skLineSegment(sketch, "E400", {"start": v(-15.58, -46.92) * mm, "end": v(-13.65, -47.15) * mm});
            skLineSegment(sketch, "E401", {"start": v(-13.65, -47.15) * mm, "end": v(-13.53, -45.78) * mm});
            skLineSegment(sketch, "E402", {"start": v(-13.53, -45.78) * mm, "end": v(-12.4, -45.16) * mm});
            skLineSegment(sketch, "E403", {"start": v(-12.4, -45.16) * mm, "end": v(-12.51, -42.37) * mm});
            skLineSegment(sketch, "E404", {"start": v(-12.51, -42.37) * mm, "end": v(-13.88, -41.68) * mm});
            skLineSegment(sketch, "E405", {"start": v(-13.88, -41.68) * mm, "end": v(-13.99, -39.4) * mm});
            skLineSegment(sketch, "E406", {"start": v(-13.99, -39.4) * mm, "end": v(-15.3, -38.95) * mm});
            skLineSegment(sketch, "E407", {"start": v(-15.3, -38.95) * mm, "end": v(-15.58, -36.79) * mm});
            skLineSegment(sketch, "E408", {"start": v(-15.58, -36.79) * mm, "end": v(-16.84, -36.22) * mm});
            skLineSegment(sketch, "E409", {"start": v(-16.84, -36.22) * mm, "end": v(-16.84, -31.72) * mm});
            skLineSegment(sketch, "E410", {"start": v(-16.84, -31.72) * mm, "end": v(-17.58, -31.55) * mm});
            skLineSegment(sketch, "E411", {"start": v(-17.58, -31.55) * mm, "end": v(-17.63, -29.4) * mm});
            skLineSegment(sketch, "E412", {"start": v(-17.63, -29.4) * mm, "end": v(-18.83, -29.62) * mm});
            skLineSegment(sketch, "E413", {"start": v(-18.83, -29.62) * mm, "end": v(-20.58, -30.2) * mm});
            skLineSegment(sketch, "E414", {"start": v(-32.71, -41.74) * mm, "end": v(-32.71, -43.67) * mm});
            skLineSegment(sketch, "E415", {"start": v(-32.71, -43.67) * mm, "end": v(-29.92, -44.05) * mm});
            skLineSegment(sketch, "E416", {"start": v(-29.92, -44.05) * mm, "end": v(-28.63, -45.12) * mm});
            skLineSegment(sketch, "E417", {"start": v(-28.63, -45.12) * mm, "end": v(-28.04, -45.98) * mm});
            skLineSegment(sketch, "E418", {"start": v(-28.04, -45.98) * mm, "end": v(-28.63, -47.38) * mm});
            skLineSegment(sketch, "E419", {"start": v(-28.63, -47.38) * mm, "end": v(-30.67, -47.92) * mm});
            skLineSegment(sketch, "E420", {"start": v(-30.67, -47.92) * mm, "end": v(-32.98, -49.1) * mm});
            skLineSegment(sketch, "E421", {"start": v(-32.98, -49.1) * mm, "end": v(-35.19, -49.37) * mm});
            skLineSegment(sketch, "E422", {"start": v(-35.19, -49.37) * mm, "end": v(-38.2, -49.1) * mm});
            skLineSegment(sketch, "E423", {"start": v(-38.2, -49.1) * mm, "end": v(-40.07, -47.76) * mm});
            skLineSegment(sketch, "E424", {"start": v(-40.07, -47.76) * mm, "end": v(-43.03, -47.54) * mm});
            skLineSegment(sketch, "E425", {"start": v(-43.03, -47.54) * mm, "end": v(-44.1, -45.93) * mm});
            skLineSegment(sketch, "E426", {"start": v(-44.1, -45.93) * mm, "end": v(-45.6, -45.82) * mm});
            skLineSegment(sketch, "E427", {"start": v(-45.6, -45.82) * mm, "end": v(-45.82, -48.24) * mm});
            skLineSegment(sketch, "E428", {"start": v(-45.82, -48.24) * mm, "end": v(-44.75, -49.53) * mm});
            skLineSegment(sketch, "E429", {"start": v(-44.75, -49.53) * mm, "end": v(-45.02, -50.98) * mm});
            skLineSegment(sketch, "E430", {"start": v(-45.02, -50.98) * mm, "end": v(-43.35, -51.63) * mm});
            skLineSegment(sketch, "E431", {"start": v(-43.35, -51.63) * mm, "end": v(-43.78, -53.45) * mm});
            skLineSegment(sketch, "E432", {"start": v(-43.78, -53.45) * mm, "end": v(-42.5, -54.2) * mm});
            skLineSegment(sketch, "E433", {"start": v(-42.5, -54.2) * mm, "end": v(-42.5, -55.6) * mm});
            skLineSegment(sketch, "E434", {"start": v(-42.5, -55.6) * mm, "end": v(-41.42, -56.08) * mm});
            skLineSegment(sketch, "E435", {"start": v(-41.42, -56.08) * mm, "end": v(-41.36, -57.91) * mm});
            skLineSegment(sketch, "E436", {"start": v(-41.36, -57.91) * mm, "end": v(-40.34, -58.77) * mm});
            skLineSegment(sketch, "E437", {"start": v(-40.34, -58.77) * mm, "end": v(-40.18, -61.3) * mm});
            skLineSegment(sketch, "E438", {"start": v(-40.18, -61.3) * mm, "end": v(-38.9, -61.94) * mm});
            skLineSegment(sketch, "E439", {"start": v(-38.9, -61.94) * mm, "end": v(-38.52, -63.01) * mm});
            skLineSegment(sketch, "E440", {"start": v(-38.52, -63.01) * mm, "end": v(-37.76, -63.23) * mm});
            skLineSegment(sketch, "E441", {"start": v(-37.76, -63.23) * mm, "end": v(-37.55, -65.65) * mm});
            skLineSegment(sketch, "E442", {"start": v(-37.55, -65.65) * mm, "end": v(-39.05, -65.6) * mm});
            skLineSegment(sketch, "E443", {"start": v(-39.05, -65.6) * mm, "end": v(-39.22, -65.22) * mm});
            skLineSegment(sketch, "E444", {"start": v(-39.22, -65.22) * mm, "end": v(-44.21, -65.06) * mm});
            skLineSegment(sketch, "E445", {"start": v(-44.21, -65.06) * mm, "end": v(-45.5, -66.24) * mm});
            skLineSegment(sketch, "E446", {"start": v(-45.5, -66.24) * mm, "end": v(-47, -66.72) * mm});
            skLineSegment(sketch, "E447", {"start": v(-47, -66.72) * mm, "end": v(-48.78, -69.72) * mm});
            skLineSegment(sketch, "E448", {"start": v(-48.78, -69.72) * mm, "end": v(-49, -74.13) * mm});
            skLineSegment(sketch, "E449", {"start": v(-49, -74.13) * mm, "end": v(-47.92, -74.77) * mm});
            skLineSegment(sketch, "E450", {"start": v(-47.92, -74.77) * mm, "end": v(-46.9, -76.12) * mm});
            skLineSegment(sketch, "E451", {"start": v(-46.9, -76.12) * mm, "end": v(-32.55, -76.06) * mm});
            skLineSegment(sketch, "E452", {"start": v(-32.55, -76.06) * mm, "end": v(-32.28, -75.04) * mm});
            skLineSegment(sketch, "E453", {"start": v(-32.28, -75.04) * mm, "end": v(-31.32, -74.72) * mm});
            skLineSegment(sketch, "E454", {"start": v(-31.32, -74.72) * mm, "end": v(-30.24, -74.24) * mm});
            skLineSegment(sketch, "E455", {"start": v(-30.24, -74.24) * mm, "end": v(-29.81, -73.48) * mm});
            skLineSegment(sketch, "E456", {"start": v(-29.81, -73.48) * mm, "end": v(-25.14, -73.38) * mm});
            skLineSegment(sketch, "E457", {"start": v(-25.14, -73.38) * mm, "end": v(-24.7, -65.75) * mm});
            skLineSegment(sketch, "E458", {"start": v(-24.7, -65.75) * mm, "end": v(-26, -65.48) * mm});
            skLineSegment(sketch, "E459", {"start": v(-26, -65.48) * mm, "end": v(-26.16, -62.74) * mm});
            skLineSegment(sketch, "E460", {"start": v(-26.16, -62.74) * mm, "end": v(-26.86, -60.97) * mm});
            skLineSegment(sketch, "E461", {"start": v(-26.86, -60.97) * mm, "end": v(-27.34, -59.52) * mm});
            skLineSegment(sketch, "E462", {"start": v(-27.34, -59.52) * mm, "end": v(-26.91, -50.6) * mm});
            skLineSegment(sketch, "E463", {"start": v(-26.91, -50.6) * mm, "end": v(-25.95, -49.3) * mm});
            skLineSegment(sketch, "E464", {"start": v(-25.95, -49.3) * mm, "end": v(-25.73, -43.67) * mm});
            skLineSegment(sketch, "E465", {"start": v(-25.73, -43.67) * mm, "end": v(-28.04, -43.08) * mm});
            skLineSegment(sketch, "E466", {"start": v(-28.04, -43.08) * mm, "end": v(-28.42, -41.68) * mm});
            skLineSegment(sketch, "E467", {"start": v(-28.42, -41.68) * mm, "end": v(-32.71, -41.74) * mm});
            skLineSegment(sketch, "E468", {"start": v(-39.07, -52.71) * mm, "end": v(-39.07, -54.2) * mm});
            skLineSegment(sketch, "E469", {"start": v(-39.07, -54.2) * mm, "end": v(-35.03, -53.96) * mm});
            skLineSegment(sketch, "E470", {"start": v(-35.03, -53.96) * mm, "end": v(-34.4, -52.71) * mm});
            skLineSegment(sketch, "E471", {"start": v(-34.4, -52.71) * mm, "end": v(-32.46, -52.48) * mm});
            skLineSegment(sketch, "E472", {"start": v(-32.46, -52.48) * mm, "end": v(-32.7, -50.95) * mm});
            skLineSegment(sketch, "E473", {"start": v(-32.7, -50.95) * mm, "end": v(-36.85, -50.66) * mm});
            skLineSegment(sketch, "E474", {"start": v(-36.85, -50.66) * mm, "end": v(-37.36, -52.6) * mm});
            skLineSegment(sketch, "E475", {"start": v(-37.36, -52.6) * mm, "end": v(-39.07, -52.71) * mm});
            skLineSegment(sketch, "E476", {"start": v(-38.15, -56.74) * mm, "end": v(-38.15, -58.4) * mm});
            skLineSegment(sketch, "E477", {"start": v(-38.15, -58.4) * mm, "end": v(-34.49, -58.21) * mm});
            skLineSegment(sketch, "E478", {"start": v(-34.49, -58.21) * mm, "end": v(-32.05, -57.04) * mm});
            skLineSegment(sketch, "E479", {"start": v(-32.05, -57.04) * mm, "end": v(-32.12, -55.23) * mm});
            skLineSegment(sketch, "E480", {"start": v(-32.12, -55.23) * mm, "end": v(-34.85, -55.34) * mm});
            skLineSegment(sketch, "E481", {"start": v(-34.85, -55.34) * mm, "end": v(-35.87, -56.59) * mm});
            skLineSegment(sketch, "E482", {"start": v(-35.87, -56.59) * mm, "end": v(-38.15, -56.74) * mm});
            skLineSegment(sketch, "E483", {"start": v(-35.47, -63.71) * mm, "end": v(-34.16, -64.23) * mm});
            skLineSegment(sketch, "E484", {"start": v(-34.16, -64.23) * mm, "end": v(-33.24, -63.59) * mm});
            skLineSegment(sketch, "E485", {"start": v(-33.24, -63.59) * mm, "end": v(-32.76, -63.59) * mm});
            skLineSegment(sketch, "E486", {"start": v(-32.76, -63.59) * mm, "end": v(-32.18, -64.16) * mm});
            skLineSegment(sketch, "E487", {"start": v(-32.18, -64.16) * mm, "end": v(-30.55, -64.23) * mm});
            skLineSegment(sketch, "E488", {"start": v(-30.55, -64.23) * mm, "end": v(-30.14, -63.33) * mm});
            skLineSegment(sketch, "E489", {"start": v(-30.14, -63.33) * mm, "end": v(-31.2, -62.37) * mm});
            skLineSegment(sketch, "E490", {"start": v(-31.2, -62.37) * mm, "end": v(-31.35, -61.22) * mm});
            skLineSegment(sketch, "E491", {"start": v(-31.35, -61.22) * mm, "end": v(-34.45, -61.1) * mm});
            skLineSegment(sketch, "E492", {"start": v(-34.45, -61.1) * mm, "end": v(-34.58, -62.25) * mm});
            skLineSegment(sketch, "E493", {"start": v(-34.58, -62.25) * mm, "end": v(-35.5, -63.08) * mm});
            skLineSegment(sketch, "E494", {"start": v(-35.5, -63.08) * mm, "end": v(-35.47, -63.71) * mm});
            skLineSegment(sketch, "E495", {"start": v(-4.98, -17.64) * mm, "end": v(-2.7, -16.54) * mm});
            skLineSegment(sketch, "E496", {"start": v(-2.7, -16.54) * mm, "end": v(-3.05, -12.91) * mm});
            skLineSegment(sketch, "E497", {"start": v(-3.05, -12.91) * mm, "end": v(-1.9, -12.13) * mm});
            skLineSegment(sketch, "E498", {"start": v(-1.9, -12.13) * mm, "end": v(-1.93, -8.15) * mm});
            skLineSegment(sketch, "E499", {"start": v(-1.93, -8.15) * mm, "end": v(-0.57, -7.94) * mm});
            skLineSegment(sketch, "E500", {"start": v(-0.57, -7.94) * mm, "end": v(-0.43, 2.6) * mm});
            skLineSegment(sketch, "E501", {"start": v(-0.43, 2.6) * mm, "end": v(0.98, 3.24) * mm});
            skLineSegment(sketch, "E502", {"start": v(0.98, 3.24) * mm, "end": v(1, 8.37) * mm});
            skLineSegment(sketch, "E503", {"start": v(1, 8.37) * mm, "end": v(2.2, 8.73) * mm});
            skLineSegment(sketch, "E504", {"start": v(2.2, 8.73) * mm, "end": v(2.08, 10.42) * mm});
            skLineSegment(sketch, "E505", {"start": v(2.08, 10.42) * mm, "end": v(-1.3, 10.36) * mm});
            skLineSegment(sketch, "E506", {"start": v(-1.3, 10.36) * mm, "end": v(-1.83, 8.91) * mm});
            skLineSegment(sketch, "E507", {"start": v(-1.83, 8.91) * mm, "end": v(-3.4, 8.64) * mm});
            skLineSegment(sketch, "E508", {"start": v(-3.4, 8.64) * mm, "end": v(-3.55, 9.21) * mm});
            skLineSegment(sketch, "E509", {"start": v(-3.55, 9.21) * mm, "end": v(-5.1, 8.97) * mm});
            skLineSegment(sketch, "E510", {"start": v(-5.1, 8.97) * mm, "end": v(-4.96, -7.04) * mm});
            skLineSegment(sketch, "E511", {"start": v(-4.96, -7.04) * mm, "end": v(-4.79, -8) * mm});
            skLineSegment(sketch, "E512", {"start": v(-4.79, -8) * mm, "end": v(-4.24, -9.95) * mm});
            skLineSegment(sketch, "E513", {"start": v(-4.24, -9.95) * mm, "end": v(-4.51, -11.45) * mm});
            skLineSegment(sketch, "E514", {"start": v(-4.51, -11.45) * mm, "end": v(-5.15, -11.64) * mm});
            skLineSegment(sketch, "E515", {"start": v(-5.15, -11.64) * mm, "end": v(-4.98, -17.64) * mm});
            skLineSegment(sketch, "E516", {"start": v(-4.63, 11.7) * mm, "end": v(-4.63, 10.16) * mm});
            skLineSegment(sketch, "E517", {"start": v(-4.63, 10.16) * mm, "end": v(-2.33, 10.28) * mm});
            skLineSegment(sketch, "E518", {"start": v(-2.33, 10.28) * mm, "end": v(-2.22, 11.47) * mm});
            skLineSegment(sketch, "E519", {"start": v(-2.22, 11.47) * mm, "end": v(2.8, 11.61) * mm});
            skLineSegment(sketch, "E520", {"start": v(2.8, 11.61) * mm, "end": v(2.94, 14.94) * mm});
            skLineSegment(sketch, "E521", {"start": v(2.94, 14.94) * mm, "end": v(1.8, 14.66) * mm});
            skLineSegment(sketch, "E522", {"start": v(1.8, 14.66) * mm, "end": v(1.57, 13.24) * mm});
            skLineSegment(sketch, "E523", {"start": v(1.57, 13.24) * mm, "end": v(-3.27, 13.24) * mm});
            skLineSegment(sketch, "E524", {"start": v(-3.27, 13.24) * mm, "end": v(-3.5, 11.96) * mm});
            skLineSegment(sketch, "E525", {"start": v(-3.5, 11.96) * mm, "end": v(-4.63, 11.7) * mm});
            skLineSegment(sketch, "E526", {"start": v(-17.76, -50.4) * mm, "end": v(-19.43, -51.69) * mm});
            skLineSegment(sketch, "E527", {"start": v(-19.43, -51.69) * mm, "end": v(-20.36, -53.1) * mm});
            skLineSegment(sketch, "E528", {"start": v(-20.36, -53.1) * mm, "end": v(-17.39, -53.86) * mm});
            skLineSegment(sketch, "E529", {"start": v(-17.39, -53.86) * mm, "end": v(-16.72, -52.9) * mm});
            skLineSegment(sketch, "E530", {"start": v(-16.72, -52.9) * mm, "end": v(-15.19, -52.61) * mm});
            skLineSegment(sketch, "E531", {"start": v(-15.19, -52.61) * mm, "end": v(-12.32, -48.88) * mm});
            skLineSegment(sketch, "E532", {"start": v(-12.32, -48.88) * mm, "end": v(-10.22, -46.43) * mm});
            skLineSegment(sketch, "E533", {"start": v(-10.22, -46.43) * mm, "end": v(-10.4, -45.63) * mm});
            skLineSegment(sketch, "E534", {"start": v(-10.4, -45.63) * mm, "end": v(-11.17, -44.29) * mm});
            skLineSegment(sketch, "E535", {"start": v(-11.17, -44.29) * mm, "end": v(-10.02, -43.23) * mm});
            skLineSegment(sketch, "E536", {"start": v(-10.02, -43.23) * mm, "end": v(-8.3, -44.67) * mm});
            skLineSegment(sketch, "E537", {"start": v(-8.3, -44.67) * mm, "end": v(-7.91, -47.16) * mm});
            skLineSegment(sketch, "E538", {"start": v(-7.91, -47.16) * mm, "end": v(-6.67, -48.6) * mm});
            skLineSegment(sketch, "E539", {"start": v(-6.67, -48.6) * mm, "end": v(-6.1, -50.32) * mm});
            skLineSegment(sketch, "E540", {"start": v(-6.1, -50.32) * mm, "end": v(-5.42, -52.42) * mm});
            skLineSegment(sketch, "E541", {"start": v(-5.42, -52.42) * mm, "end": v(-4.47, -54.34) * mm});
            skLineSegment(sketch, "E542", {"start": v(-4.47, -54.34) * mm, "end": v(-3.9, -55.68) * mm});
            skLineSegment(sketch, "E543", {"start": v(-3.9, -55.68) * mm, "end": v(-3.32, -57.02) * mm});
            skLineSegment(sketch, "E544", {"start": v(-3.32, -57.02) * mm, "end": v(-2.65, -59.5) * mm});
            skLineSegment(sketch, "E545", {"start": v(-2.65, -59.5) * mm, "end": v(-3.7, -61.61) * mm});
            skLineSegment(sketch, "E546", {"start": v(-3.7, -61.61) * mm, "end": v(-4.4, -62.58) * mm});
            skLineSegment(sketch, "E547", {"start": v(-4.4, -62.58) * mm, "end": v(-5.92, -64.86) * mm});
            skLineSegment(sketch, "E548", {"start": v(-5.92, -64.86) * mm, "end": v(-6.86, -66.3) * mm});
            skLineSegment(sketch, "E549", {"start": v(-6.86, -66.3) * mm, "end": v(-6, -66.3) * mm});
            skLineSegment(sketch, "E550", {"start": v(-6, -66.3) * mm, "end": v(-4.85, -65.15) * mm});
            skLineSegment(sketch, "E551", {"start": v(-4.85, -65.15) * mm, "end": v(-3.6, -63.43) * mm});
            skLineSegment(sketch, "E552", {"start": v(-3.6, -63.43) * mm, "end": v(-2.74, -62.47) * mm});
            skLineSegment(sketch, "E553", {"start": v(-2.74, -62.47) * mm, "end": v(4.34, -62.38) * mm});
            skLineSegment(sketch, "E554", {"start": v(4.34, -62.38) * mm, "end": v(4.53, -67.07) * mm});
            skLineSegment(sketch, "E555", {"start": v(4.53, -67.07) * mm, "end": v(0.9, -71.28) * mm});
            skLineSegment(sketch, "E556", {"start": v(0.9, -71.28) * mm, "end": v(0.9, -76.26) * mm});
            skLineSegment(sketch, "E557", {"start": v(0.9, -76.26) * mm, "end": v(-4.37, -76.26) * mm});
            skLineSegment(sketch, "E558", {"start": v(-4.37, -76.26) * mm, "end": v(-4.66, -74.54) * mm});
            skLineSegment(sketch, "E559", {"start": v(-4.66, -74.54) * mm, "end": v(-6.96, -74.54) * mm});
            skLineSegment(sketch, "E560", {"start": v(-6.96, -74.54) * mm, "end": v(-11.65, -74.25) * mm});
            skLineSegment(sketch, "E561", {"start": v(-11.65, -74.25) * mm, "end": v(-11.55, -71.76) * mm});
            skLineSegment(sketch, "E562", {"start": v(-11.55, -71.76) * mm, "end": v(-13.46, -71.18) * mm});
            skLineSegment(sketch, "E563", {"start": v(-13.46, -71.18) * mm, "end": v(-12.99, -65.15) * mm});
            skLineSegment(sketch, "E564", {"start": v(-12.99, -65.15) * mm, "end": v(-22.94, -53.57) * mm});
            skLineSegment(sketch, "E565", {"start": v(-22.94, -53.57) * mm, "end": v(-20.16, -48.88) * mm});
            skLineSegment(sketch, "E566", {"start": v(-20.16, -48.88) * mm, "end": v(-18.85, -49.07) * mm});
            skLineSegment(sketch, "E567", {"start": v(-18.85, -49.07) * mm, "end": v(-17.76, -50.4) * mm});
            skLineSegment(sketch, "E568", {"start": v(-14.04, -55.98) * mm, "end": v(-12.71, -57.07) * mm});
            skLineSegment(sketch, "E569", {"start": v(-12.71, -57.07) * mm, "end": v(-10.54, -56.7) * mm});
            skLineSegment(sketch, "E570", {"start": v(-10.54, -56.7) * mm, "end": v(-9.5, -54.3) * mm});
            skLineSegment(sketch, "E571", {"start": v(-9.5, -54.3) * mm, "end": v(-8.33, -54.09) * mm});
            skLineSegment(sketch, "E572", {"start": v(-8.33, -54.09) * mm, "end": v(-7.97, -52.76) * mm});
            skLineSegment(sketch, "E573", {"start": v(-7.97, -52.76) * mm, "end": v(-10.54, -52.52) * mm});
            skLineSegment(sketch, "E574", {"start": v(-10.54, -52.52) * mm, "end": v(-11.55, -53.89) * mm});
            skLineSegment(sketch, "E575", {"start": v(-11.55, -53.89) * mm, "end": v(-13.12, -55.18) * mm});
            skLineSegment(sketch, "E576", {"start": v(-13.12, -55.18) * mm, "end": v(-14.04, -55.98) * mm});
            skLineSegment(sketch, "E577", {"start": v(-11.95, -59.26) * mm, "end": v(-10.48, -59.65) * mm});
            skLineSegment(sketch, "E578", {"start": v(-10.48, -59.65) * mm, "end": v(-10.59, -60.73) * mm});
            skLineSegment(sketch, "E579", {"start": v(-10.59, -60.73) * mm, "end": v(-9.19, -60.94) * mm});
            skLineSegment(sketch, "E580", {"start": v(-9.19, -60.94) * mm, "end": v(-8.22, -58.97) * mm});
            skLineSegment(sketch, "E581", {"start": v(-8.22, -58.97) * mm, "end": v(-6.64, -57.6) * mm});
            skLineSegment(sketch, "E582", {"start": v(-6.64, -57.6) * mm, "end": v(-7.04, -55.17) * mm});
            skLineSegment(sketch, "E583", {"start": v(-7.04, -55.17) * mm, "end": v(-9.65, -57.86) * mm});
            skLineSegment(sketch, "E584", {"start": v(-9.65, -57.86) * mm, "end": v(-11.52, -58.25) * mm});
            skLineSegment(sketch, "E585", {"start": v(-11.52, -58.25) * mm, "end": v(-11.95, -59.26) * mm});
            skLineSegment(sketch, "E586", {"start": v(-49.36, -15.76) * mm, "end": v(-49.36, -12.65) * mm});
            skLineSegment(sketch, "E587", {"start": v(-49.36, -12.65) * mm, "end": v(-48.34, -12.88) * mm});
            skLineSegment(sketch, "E588", {"start": v(-48.34, -12.88) * mm, "end": v(-47.76, -14.1) * mm});
            skLineSegment(sketch, "E589", {"start": v(-47.76, -14.1) * mm, "end": v(-47.17, -15.45) * mm});
            skLineSegment(sketch, "E590", {"start": v(-47.17, -15.45) * mm, "end": v(-46.13, -15.95) * mm});
            skLineSegment(sketch, "E591", {"start": v(-46.13, -15.95) * mm, "end": v(-45.61, -17.04) * mm});
            skLineSegment(sketch, "E592", {"start": v(-45.61, -17.04) * mm, "end": v(-44.86, -17.4) * mm});
            skLineSegment(sketch, "E593", {"start": v(-45, -15.9) * mm, "end": v(-45.7, -15.13) * mm});
            skLineSegment(sketch, "E594", {"start": v(-45.7, -15.13) * mm, "end": v(-45.75, -13.14) * mm});
            skLineSegment(sketch, "E595", {"start": v(-45.75, -13.14) * mm, "end": v(-45.4, -12.59) * mm});
            skLineSegment(sketch, "E596", {"start": v(-28.08, 56.06) * mm, "end": v(-28.1, 63.47) * mm});
            skLineSegment(sketch, "E597", {"start": v(-28.1, 63.47) * mm, "end": v(-26.5, 63.46) * mm});
            skLineSegment(sketch, "E598", {"start": v(-26.5, 63.46) * mm, "end": v(-26.44, 62.47) * mm});
            skLineSegment(sketch, "E599", {"start": v(-21.37, 63.6) * mm, "end": v(-21.37, 61.88) * mm});
            skLineSegment(sketch, "E600", {"start": v(-20.43, 55.93) * mm, "end": v(-15.63, 55.93) * mm});
            skLineSegment(sketch, "E601", {"start": v(-15.63, 55.93) * mm, "end": v(-15.63, 57.46) * mm});
            skLineSegment(sketch, "E602", {"start": v(-15.63, 57.46) * mm, "end": v(-17, 57.46) * mm});
            skLineSegment(sketch, "E603", {"start": v(-17, 57.46) * mm, "end": v(-17, 61.77) * mm});
            skLineSegment(sketch, "E604", {"start": v(-17, 61.77) * mm, "end": v(-13.12, 61.77) * mm});
            skLineSegment(sketch, "E605", {"start": v(-13.12, 61.77) * mm, "end": v(-13.12, 63.61) * mm});
            skLineSegment(sketch, "E606", {"start": v(-13.12, 63.61) * mm, "end": v(-21.37, 63.6) * mm});
            skSolve(sketch);
        }
        {
            var Q0;
            Q0=makeQuery(id+"F0.imprint","IMPRINT",FACE,{"disambiguationData":[TD([[makeQuery(id+"F0.imprint","IMPRINT",EDGE,{"derivedFrom":sQuery(id+"F0.wireOp",EDGE,"E0")}),1.0]])]});
            var Q1;
            Q1=makeQuery(id+"F0.imprint","IMPRINT",FACE,{"disambiguationData":[TD([[makeQuery(id+"F0.imprint","IMPRINT",EDGE,{"derivedFrom":sQuery(id+"F0.wireOp",EDGE,"E68")}),1.0]])]});
            var Q2;
            Q2=makeQuery(id+"F0.imprint","IMPRINT",FACE,{"disambiguationData":[TD([[makeQuery(id+"F0.imprint","IMPRINT",EDGE,{"derivedFrom":sQuery(id+"F0.wireOp",EDGE,"E74")}),1.0]])]});
            var Q3;
            Q3=makeQuery(id+"F0.imprint","IMPRINT",FACE,{"disambiguationData":[TD([[makeQuery(id+"F0.imprint","IMPRINT",EDGE,{"derivedFrom":sQuery(id+"F0.wireOp",EDGE,"E78")}),1.0]])]});
            var Q4;
            Q4=makeQuery(id+"F0.imprint","IMPRINT",FACE,{"disambiguationData":[TD([[makeQuery(id+"F0.imprint","IMPRINT",EDGE,{"derivedFrom":sQuery(id+"F0.wireOp",EDGE,"E82")}),1.0]])]});
            var Q5;
            Q5=makeQuery(id+"F0.imprint","IMPRINT",FACE,{"disambiguationData":[TD([[makeQuery(id+"F0.imprint","IMPRINT",EDGE,{"derivedFrom":sQuery(id+"F0.wireOp",EDGE,"E105")}),1.0]])]});
            var Q6;
            Q6=makeQuery(id+"F0.imprint","IMPRINT",FACE,{"disambiguationData":[TD([[makeQuery(id+"F0.imprint","IMPRINT",EDGE,{"derivedFrom":sQuery(id+"F0.wireOp",EDGE,"E101")}),1.0]])]});
            var Q7;
            Q7=makeQuery(id+"F0.imprint","IMPRINT",FACE,{"disambiguationData":[TD([[makeQuery(id+"F0.imprint","IMPRINT",EDGE,{"derivedFrom":sQuery(id+"F0.wireOp",EDGE,"E97")}),1.0]])]});
            var Q8;
            Q8=makeQuery(id+"F0.imprint","IMPRINT",FACE,{"disambiguationData":[TD([[makeQuery(id+"F0.imprint","IMPRINT",EDGE,{"derivedFrom":sQuery(id+"F0.wireOp",EDGE,"E93")}),1.0]])]});
            var Q9;
            Q9=makeQuery(id+"F0.imprint","IMPRINT",FACE,{"disambiguationData":[TD([[makeQuery(id+"F0.imprint","IMPRINT",EDGE,{"derivedFrom":sQuery(id+"F0.wireOp",EDGE,"E89")}),-1.0]])]});
            var Q10;
            Q10=makeQuery(id+"F0.imprint","IMPRINT",FACE,{"disambiguationData":[TD([[makeQuery(id+"F0.imprint","IMPRINT",EDGE,{"derivedFrom":sQuery(id+"F0.wireOp",EDGE,"E110")}),-1.0]])]});
            var Q11;
            Q11=makeQuery(id+"F0.imprint","IMPRINT",FACE,{"disambiguationData":[TD([[makeQuery(id+"F0.imprint","IMPRINT",EDGE,{"derivedFrom":sQuery(id+"F0.wireOp",EDGE,"E151")}),-1.0]])]});
            var Q12;
            Q12=makeQuery(id+"F0.imprint","IMPRINT",FACE,{"disambiguationData":[TD([[makeQuery(id+"F0.imprint","IMPRINT",EDGE,{"derivedFrom":sQuery(id+"F0.wireOp",EDGE,"E189")}),1.0]])]});
            var Q13;
            Q13=makeQuery(id+"F0.imprint","IMPRINT",FACE,{"disambiguationData":[TD([[makeQuery(id+"F0.imprint","IMPRINT",EDGE,{"derivedFrom":sQuery(id+"F0.wireOp",EDGE,"E203")}),-1.0]])]});
            var Q14;
            Q14=makeQuery(id+"F0.imprint","IMPRINT",FACE,{"disambiguationData":[TD([[makeQuery(id+"F0.imprint","IMPRINT",EDGE,{"derivedFrom":sQuery(id+"F0.wireOp",EDGE,"E247")}),-1.0]])]});
            var Q15;
            Q15=makeQuery(id+"F0.imprint","IMPRINT",FACE,{"disambiguationData":[TD([[makeQuery(id+"F0.imprint","IMPRINT",EDGE,{"derivedFrom":sQuery(id+"F0.wireOp",EDGE,"E261")}),1.0]])]});
            var Q16;
            Q16=makeQuery(id+"F0.imprint","IMPRINT",FACE,{"disambiguationData":[TD([[makeQuery(id+"F0.imprint","IMPRINT",EDGE,{"derivedFrom":sQuery(id+"F0.wireOp",EDGE,"E266")}),-1.0]])]});
            var Q17;
            Q17=makeQuery(id+"F0.imprint","IMPRINT",FACE,{"disambiguationData":[TD([[makeQuery(id+"F0.imprint","IMPRINT",EDGE,{"derivedFrom":sQuery(id+"F0.wireOp",EDGE,"E272")}),-1.0]])]});
            var Q18;
            Q18=makeQuery(id+"F0.imprint","IMPRINT",FACE,{"disambiguationData":[TD([[makeQuery(id+"F0.imprint","IMPRINT",EDGE,{"derivedFrom":sQuery(id+"F0.wireOp",EDGE,"E290")}),1.0]])]});
            var Q19;
            Q19=makeQuery(id+"F0.imprint","IMPRINT",FACE,{"disambiguationData":[TD([[makeQuery(id+"F0.imprint","IMPRINT",EDGE,{"derivedFrom":sQuery(id+"F0.wireOp",EDGE,"E282")}),1.0]])]});
            var Q20;
            Q20=makeQuery(id+"F0.imprint","IMPRINT",FACE,{"disambiguationData":[TD([[makeQuery(id+"F0.imprint","IMPRINT",EDGE,{"derivedFrom":sQuery(id+"F0.wireOp",EDGE,"E298")}),1.0]])]});
            var Q21;
            Q21=makeQuery(id+"F0.imprint","IMPRINT",FACE,{"disambiguationData":[TD([[makeQuery(id+"F0.imprint","IMPRINT",EDGE,{"derivedFrom":sQuery(id+"F0.wireOp",EDGE,"E495")}),1.0]])]});
            var Q22;
            Q22=makeQuery(id+"F0.imprint","IMPRINT",FACE,{"disambiguationData":[TD([[makeQuery(id+"F0.imprint","IMPRINT",EDGE,{"derivedFrom":sQuery(id+"F0.wireOp",EDGE,"E516")}),1.0]])]});
            var Q23;
            Q23=makeQuery(id+"F0.imprint","IMPRINT",FACE,{"disambiguationData":[TD([[makeQuery(id+"F0.imprint","IMPRINT",EDGE,{"derivedFrom":sQuery(id+"F0.wireOp",EDGE,"E334")}),-1.0]])]});
            var Q24;
            Q24=makeQuery(id+"F0.imprint","IMPRINT",FACE,{"disambiguationData":[TD([[makeQuery(id+"F0.imprint","IMPRINT",EDGE,{"derivedFrom":sQuery(id+"F0.wireOp",EDGE,"E350")}),1.0]])]});
            var Q25;
            Q25=makeQuery(id+"F0.imprint","IMPRINT",FACE,{"disambiguationData":[TD([[makeQuery(id+"F0.imprint","IMPRINT",EDGE,{"derivedFrom":sQuery(id+"F0.wireOp",EDGE,"E304")}),-1.0]])]});
            var Q26;
            Q26=makeQuery(id+"F0.imprint","IMPRINT",FACE,{"disambiguationData":[TD([[makeQuery(id+"F0.imprint","IMPRINT",EDGE,{"derivedFrom":sQuery(id+"F0.wireOp",EDGE,"E371")}),-1.0]])]});
            var Q27;
            Q27=makeQuery(id+"F0.imprint","IMPRINT",FACE,{"disambiguationData":[TD([[makeQuery(id+"F0.imprint","IMPRINT",EDGE,{"derivedFrom":sQuery(id+"F0.wireOp",EDGE,"E389")}),1.0]])]});
            var Q28;
            Q28=makeQuery(id+"F0.imprint","IMPRINT",FACE,{"disambiguationData":[TD([[makeQuery(id+"F0.imprint","IMPRINT",EDGE,{"derivedFrom":sQuery(id+"F0.wireOp",EDGE,"E414")}),1.0]])]});
            var Q29;
            Q29=makeQuery(id+"F0.imprint","IMPRINT",FACE,{"disambiguationData":[TD([[makeQuery(id+"F0.imprint","IMPRINT",EDGE,{"derivedFrom":sQuery(id+"F0.wireOp",EDGE,"E526")}),-1.0]])]});
            var Q30;
            Q30=makeQuery(id+"F0.imprint","IMPRINT",FACE,{"disambiguationData":[TD([[makeQuery(id+"F0.imprint","IMPRINT",EDGE,{"derivedFrom":sQuery(id+"F0.wireOp",EDGE,"E36")}),1.0]])]});
            var Q31;
            Q31=makeQuery(id+"F0.imprint","IMPRINT",FACE,{"disambiguationData":[TD([[makeQuery(id+"F0.imprint","IMPRINT",EDGE,{"derivedFrom":sQuery(id+"F0.wireOp",EDGE,"E599")}),1.0]])]});
            extrude(context, id + "F1", {"entities" : qUnion([Q0, Q1, Q2, Q3, Q4, Q5, Q6, Q7, Q8, Q9, Q10, Q11, Q12, Q13, Q14, Q15, Q16, Q17, Q18, Q19, Q20, Q21, Q22, Q23, Q24, Q25, Q26, Q27, Q28, Q29, Q30, Q31]), "depth" : 12.7 * mm, "hasSecondDirection" : true, "secondDirectionOppositeDirection" : true, "secondDirectionDepth" : 12.7 * mm});
        }
        {
            var Q0;
            Q0=qCreatedBy(makeId("Front.planeOp"),FACE);
            var sketch = newSketch(context, id + "F2", { "sketchPlane" : qUnion([Q0])});
            skLineSegment(sketch, "E607", {"start": v(15.98, 27.1) * mm, "end": v(29.52, 27.1) * mm});
            skLineSegment(sketch, "E608", {"start": v(29.52, 27.1) * mm, "end": v(32.1, 25.6) * mm});
            skLineSegment(sketch, "E609", {"start": v(32.1, 25.6) * mm, "end": v(35.53, 23.77) * mm});
            skLineSegment(sketch, "E610", {"start": v(35.53, 23.77) * mm, "end": v(37.79, 21.09) * mm});
            skLineSegment(sketch, "E611", {"start": v(37.79, 21.09) * mm, "end": v(39.72, 18.3) * mm});
            skLineSegment(sketch, "E612", {"start": v(39.72, 18.3) * mm, "end": v(41.33, 15.82) * mm});
            skLineSegment(sketch, "E613", {"start": v(41.33, 15.82) * mm, "end": v(41.33, 7.12) * mm});
            skLineSegment(sketch, "E614", {"start": v(41.33, 7.12) * mm, "end": v(40.26, 5.83) * mm});
            skLineSegment(sketch, "E615", {"start": v(40.26, 5.83) * mm, "end": v(40.15, 3.9) * mm});
            skLineSegment(sketch, "E616", {"start": v(40.15, 3.9) * mm, "end": v(38.65, 2.4) * mm});
            skLineSegment(sketch, "E617", {"start": v(38.65, 2.4) * mm, "end": v(40.15, 0.89) * mm});
            skLineSegment(sketch, "E618", {"start": v(40.15, 0.89) * mm, "end": v(40.15, -5.45) * mm});
            skLineSegment(sketch, "E619", {"start": v(40.15, -5.45) * mm, "end": v(38.65, -7.06) * mm});
            skLineSegment(sketch, "E620", {"start": v(38.65, -7.06) * mm, "end": v(36.6, -9.86) * mm});
            skLineSegment(sketch, "E621", {"start": v(36.6, -9.86) * mm, "end": v(33.81, -12) * mm});
            skLineSegment(sketch, "E622", {"start": v(33.81, -12) * mm, "end": v(30.37, -14.05) * mm});
            skLineSegment(sketch, "E623", {"start": v(30.37, -14.05) * mm, "end": v(15.76, -14.05) * mm});
            skLineSegment(sketch, "E624", {"start": v(15.76, -14.05) * mm, "end": v(12.97, -12.33) * mm});
            skLineSegment(sketch, "E625", {"start": v(12.97, -12.33) * mm, "end": v(10.5, -10.93) * mm});
            skLineSegment(sketch, "E626", {"start": v(10.5, -10.93) * mm, "end": v(7.6, -8.35) * mm});
            skLineSegment(sketch, "E627", {"start": v(7.6, -8.35) * mm, "end": v(7.6, -4.92) * mm});
            skLineSegment(sketch, "E628", {"start": v(7.6, -4.92) * mm, "end": v(5.45, -4.92) * mm});
            skLineSegment(sketch, "E629", {"start": v(5.45, -4.92) * mm, "end": v(5.45, 0) * mm});
            skLineSegment(sketch, "E630", {"start": v(5.45, 0) * mm, "end": v(7.27, 2.18) * mm});
            skLineSegment(sketch, "E631", {"start": v(7.27, 2.18) * mm, "end": v(5.98, 4.43) * mm});
            skLineSegment(sketch, "E632", {"start": v(5.98, 4.43) * mm, "end": v(4.48, 7.12) * mm});
            skLineSegment(sketch, "E633", {"start": v(4.48, 7.12) * mm, "end": v(4.48, 16.04) * mm});
            skLineSegment(sketch, "E634", {"start": v(4.48, 16.04) * mm, "end": v(6.74, 19.47) * mm});
            skLineSegment(sketch, "E635", {"start": v(6.74, 19.47) * mm, "end": v(9.53, 22.91) * mm});
            skLineSegment(sketch, "E636", {"start": v(9.53, 22.91) * mm, "end": v(12.54, 25.38) * mm});
            skLineSegment(sketch, "E637", {"start": v(12.54, 25.38) * mm, "end": v(15.98, 27.1) * mm});
            skLineSegment(sketch, "E638", {"start": v(9.54, -1.97) * mm, "end": v(10.47, -1.97) * mm});
            skLineSegment(sketch, "E639", {"start": v(10.47, -1.97) * mm, "end": v(10.47, 0.01) * mm});
            skLineSegment(sketch, "E640", {"start": v(10.47, 0.01) * mm, "end": v(11.02, 1.29) * mm});
            skLineSegment(sketch, "E641", {"start": v(11.02, 1.29) * mm, "end": v(12.22, 1.12) * mm});
            skLineSegment(sketch, "E642", {"start": v(12.22, 1.12) * mm, "end": v(12.22, 0) * mm});
            skLineSegment(sketch, "E643", {"start": v(12.22, 0) * mm, "end": v(13.5, -1.9) * mm});
            skLineSegment(sketch, "E644", {"start": v(13.5, -1.9) * mm, "end": v(17.7, -4.2) * mm});
            skLineSegment(sketch, "E645", {"start": v(17.7, -4.2) * mm, "end": v(23.54, -4.2) * mm});
            skLineSegment(sketch, "E646", {"start": v(23.54, -4.2) * mm, "end": v(29.97, -4.2) * mm});
            skLineSegment(sketch, "E647", {"start": v(30.34, -3.05) * mm, "end": v(31.77, -2.4) * mm});
            skLineSegment(sketch, "E648", {"start": v(31.77, -2.4) * mm, "end": v(33.2, -1.7) * mm});
            skLineSegment(sketch, "E649", {"start": v(33.2, -1.7) * mm, "end": v(33.7, 0.86) * mm});
            skLineSegment(sketch, "E650", {"start": v(33.7, 0.86) * mm, "end": v(35.07, 0.95) * mm});
            skLineSegment(sketch, "E651", {"start": v(35.07, 0.95) * mm, "end": v(35.2, -0.63) * mm});
            skLineSegment(sketch, "E652", {"start": v(35.2, -0.63) * mm, "end": v(36.6, -1.01) * mm});
            skLineSegment(sketch, "E653", {"start": v(36.6, -1.01) * mm, "end": v(36.6, -2.38) * mm});
            skLineSegment(sketch, "E654", {"start": v(36.6, -2.38) * mm, "end": v(38.19, -3.23) * mm});
            skLineSegment(sketch, "E655", {"start": v(38.19, -3.23) * mm, "end": v(37.08, -4.08) * mm});
            skLineSegment(sketch, "E656", {"start": v(37.08, -4.08) * mm, "end": v(35.24, -3.96) * mm});
            skLineSegment(sketch, "E657", {"start": v(35.24, -3.96) * mm, "end": v(33.88, -6.56) * mm});
            skLineSegment(sketch, "E658", {"start": v(33.88, -6.56) * mm, "end": v(31.24, -9.37) * mm});
            skLineSegment(sketch, "E659", {"start": v(31.24, -9.37) * mm, "end": v(28.8, -10.73) * mm});
            skLineSegment(sketch, "E660", {"start": v(28.8, -10.73) * mm, "end": v(27.82, -11.25) * mm});
            skLineSegment(sketch, "E661", {"start": v(27.82, -11.25) * mm, "end": v(18.74, -11.25) * mm});
            skLineSegment(sketch, "E662", {"start": v(18.74, -11.25) * mm, "end": v(17.12, -10.14) * mm});
            skLineSegment(sketch, "E663", {"start": v(17.12, -10.14) * mm, "end": v(14.9, -8.18) * mm});
            skLineSegment(sketch, "E664", {"start": v(14.9, -8.18) * mm, "end": v(12.43, -6.43) * mm});
            skLineSegment(sketch, "E665", {"start": v(8.97, -3.36) * mm, "end": v(8.97, -2.12) * mm});
            skLineSegment(sketch, "E666", {"start": v(8.97, -2.12) * mm, "end": v(9.54, -1.97) * mm});
            skLineSegment(sketch, "E667", {"start": v(8.97, -3.36) * mm, "end": v(10.15, -3.7) * mm});
            skLineSegment(sketch, "E668", {"start": v(10.15, -3.7) * mm, "end": v(11.04, -5.42) * mm});
            skLineSegment(sketch, "E669", {"start": v(11.04, -5.42) * mm, "end": v(12.43, -6.43) * mm});
            skLineSegment(sketch, "E670", {"start": v(29.97, -4.2) * mm, "end": v(30.34, -3.05) * mm});
            skLineSegment(sketch, "E671", {"start": v(15.4, 3.88) * mm, "end": v(14.64, 2.97) * mm});
            skLineSegment(sketch, "E672", {"start": v(14.64, 2.97) * mm, "end": v(13.01, 2.48) * mm});
            skLineSegment(sketch, "E673", {"start": v(13.01, 2.48) * mm, "end": v(12.88, 1.4) * mm});
            skLineSegment(sketch, "E674", {"start": v(12.88, 1.4) * mm, "end": v(14.28, 0.72) * mm});
            skLineSegment(sketch, "E675", {"start": v(14.28, 0.72) * mm, "end": v(16, 1.53) * mm});
            skLineSegment(sketch, "E676", {"start": v(16, 1.53) * mm, "end": v(17.44, 3.7) * mm});
            skLineSegment(sketch, "E677", {"start": v(17.7, 5.37) * mm, "end": v(17.28, 5.85) * mm});
            skLineSegment(sketch, "E678", {"start": v(17.28, 5.85) * mm, "end": v(18.04, 6.53) * mm});
            skLineSegment(sketch, "E679", {"start": v(18.04, 6.53) * mm, "end": v(19.23, 6.7) * mm});
            skLineSegment(sketch, "E680", {"start": v(19.23, 6.7) * mm, "end": v(19.23, 11.74) * mm});
            skLineSegment(sketch, "E681", {"start": v(19.23, 11.74) * mm, "end": v(17.53, 13.32) * mm});
            skLineSegment(sketch, "E682", {"start": v(17.53, 13.32) * mm, "end": v(12.1, 13.73) * mm});
            skLineSegment(sketch, "E683", {"start": v(12.1, 13.73) * mm, "end": v(8.86, 11.87) * mm});
            skLineSegment(sketch, "E684", {"start": v(8.86, 11.87) * mm, "end": v(7.41, 10.52) * mm});
            skLineSegment(sketch, "E685", {"start": v(7.41, 10.52) * mm, "end": v(7.41, 9.12) * mm});
            skLineSegment(sketch, "E686", {"start": v(7.41, 9.12) * mm, "end": v(7.77, 7.18) * mm});
            skLineSegment(sketch, "E687", {"start": v(7.77, 7.18) * mm, "end": v(8.58, 5.64) * mm});
            skLineSegment(sketch, "E688", {"start": v(8.58, 5.64) * mm, "end": v(10.66, 4.96) * mm});
            skLineSegment(sketch, "E689", {"start": v(10.66, 4.96) * mm, "end": v(11.3, 4.06) * mm});
            skLineSegment(sketch, "E690", {"start": v(11.3, 4.06) * mm, "end": v(15.4, 3.88) * mm});
            skLineSegment(sketch, "E691", {"start": v(17.44, 3.7) * mm, "end": v(18, 4.57) * mm});
            skLineSegment(sketch, "E692", {"start": v(18, 4.57) * mm, "end": v(17.7, 5.37) * mm});
            skLineSegment(sketch, "E693", {"start": v(21.77, 6.56) * mm, "end": v(21.77, 3.87) * mm});
            skLineSegment(sketch, "E694", {"start": v(21.77, 3.87) * mm, "end": v(20.42, 3.4) * mm});
            skLineSegment(sketch, "E695", {"start": v(20.42, 3.4) * mm, "end": v(20.42, -0.9) * mm});
            skLineSegment(sketch, "E696", {"start": v(20.42, -0.9) * mm, "end": v(25.47, -0.9) * mm});
            skLineSegment(sketch, "E697", {"start": v(25.47, -0.9) * mm, "end": v(25.47, 3.2) * mm});
            skLineSegment(sketch, "E698", {"start": v(25.47, 3.2) * mm, "end": v(24.18, 4.2) * mm});
            skLineSegment(sketch, "E699", {"start": v(24.18, 4.2) * mm, "end": v(24.18, 6.5) * mm});
            skLineSegment(sketch, "E700", {"start": v(24.18, 6.5) * mm, "end": v(21.77, 6.56) * mm});
            skLineSegment(sketch, "E701", {"start": v(31.84, 2.77) * mm, "end": v(33.04, 2.31) * mm});
            skLineSegment(sketch, "E702", {"start": v(33.04, 2.31) * mm, "end": v(33.04, 1.18) * mm});
            skLineSegment(sketch, "E703", {"start": v(33.04, 1.18) * mm, "end": v(29.9, 1.18) * mm});
            skLineSegment(sketch, "E704", {"start": v(29.9, 1.18) * mm, "end": v(28.83, 2.31) * mm});
            skLineSegment(sketch, "E705", {"start": v(28.83, 2.31) * mm, "end": v(27.86, 3.22) * mm});
            skLineSegment(sketch, "E706", {"start": v(27.86, 3.22) * mm, "end": v(27.06, 4.36) * mm});
            skLineSegment(sketch, "E707", {"start": v(27.06, 4.36) * mm, "end": v(27.52, 5.61) * mm});
            skLineSegment(sketch, "E708", {"start": v(27.52, 5.61) * mm, "end": v(26.36, 6.04) * mm});
            skLineSegment(sketch, "E709", {"start": v(26.36, 6.04) * mm, "end": v(26.36, 11.65) * mm});
            skLineSegment(sketch, "E710", {"start": v(26.36, 11.65) * mm, "end": v(27.69, 13.58) * mm});
            skLineSegment(sketch, "E711", {"start": v(27.69, 13.58) * mm, "end": v(34.12, 13.58) * mm});
            skLineSegment(sketch, "E712", {"start": v(34.12, 13.58) * mm, "end": v(35.32, 12.67) * mm});
            skLineSegment(sketch, "E713", {"start": v(35.32, 12.67) * mm, "end": v(37.2, 12.05) * mm});
            skLineSegment(sketch, "E714", {"start": v(37.2, 12.05) * mm, "end": v(38.33, 10.5) * mm});
            skLineSegment(sketch, "E715", {"start": v(38.33, 10.5) * mm, "end": v(38.22, 6.87) * mm});
            skLineSegment(sketch, "E716", {"start": v(38.22, 6.87) * mm, "end": v(37.08, 5.73) * mm});
            skLineSegment(sketch, "E717", {"start": v(37.08, 5.73) * mm, "end": v(35.43, 5.05) * mm});
            skLineSegment(sketch, "E718", {"start": v(35.43, 5.05) * mm, "end": v(34.92, 3.85) * mm});
            skLineSegment(sketch, "E719", {"start": v(34.92, 3.85) * mm, "end": v(30.14, 3.85) * mm});
            skLineSegment(sketch, "E720", {"start": v(30.14, 3.85) * mm, "end": v(30.14, 2.88) * mm});
            skLineSegment(sketch, "E721", {"start": v(30.14, 2.88) * mm, "end": v(31.84, 2.77) * mm});
            skLineSegment(sketch, "E722", {"start": v(17.84, -14.9) * mm, "end": v(19.41, -14.9) * mm});
            skLineSegment(sketch, "E723", {"start": v(19.41, -14.9) * mm, "end": v(19.41, -16.16) * mm});
            skLineSegment(sketch, "E724", {"start": v(19.41, -16.16) * mm, "end": v(20.2, -16.88) * mm});
            skLineSegment(sketch, "E725", {"start": v(20.2, -16.88) * mm, "end": v(24.18, -16.88) * mm});
            skLineSegment(sketch, "E726", {"start": v(24.18, -16.88) * mm, "end": v(24.78, -16.4) * mm});
            skLineSegment(sketch, "E727", {"start": v(24.78, -16.4) * mm, "end": v(24.78, -15.07) * mm});
            skLineSegment(sketch, "E728", {"start": v(24.78, -15.07) * mm, "end": v(26.95, -15.07) * mm});
            skLineSegment(sketch, "E729", {"start": v(26.95, -15.07) * mm, "end": v(26.95, -17.73) * mm});
            skLineSegment(sketch, "E730", {"start": v(26.95, -17.73) * mm, "end": v(25.8, -18.57) * mm});
            skLineSegment(sketch, "E731", {"start": v(25.8, -18.57) * mm, "end": v(25.8, -21.22) * mm});
            skLineSegment(sketch, "E732", {"start": v(25.8, -21.22) * mm, "end": v(20.01, -21.22) * mm});
            skLineSegment(sketch, "E733", {"start": v(20.01, -21.22) * mm, "end": v(20.01, -19.9) * mm});
            skLineSegment(sketch, "E734", {"start": v(20.01, -19.9) * mm, "end": v(18.99, -19.05) * mm});
            skLineSegment(sketch, "E735", {"start": v(18.99, -19.05) * mm, "end": v(17.84, -17.73) * mm});
            skLineSegment(sketch, "E736", {"start": v(17.84, -17.73) * mm, "end": v(17.84, -14.9) * mm});
            skLineSegment(sketch, "E737", {"start": v(19.11, -22.8) * mm, "end": v(19.11, -37.51) * mm});
            skLineSegment(sketch, "E738", {"start": v(25.14, -37.51) * mm, "end": v(25.14, -24.91) * mm});
            skLineSegment(sketch, "E739", {"start": v(25.14, -24.91) * mm, "end": v(24.3, -24.85) * mm});
            skLineSegment(sketch, "E740", {"start": v(24.3, -24.85) * mm, "end": v(23.7, -24.55) * mm});
            skLineSegment(sketch, "E741", {"start": v(23.7, -24.55) * mm, "end": v(23.4, -23.28) * mm});
            skLineSegment(sketch, "E742", {"start": v(19.11, -22.8) * mm, "end": v(23.24, -22.8) * mm});
            skLineSegment(sketch, "E743", {"start": v(23.24, -22.8) * mm, "end": v(23.4, -23.28) * mm});
            skLineSegment(sketch, "E744", {"start": v(19.11, -37.51) * mm, "end": v(25.14, -37.51) * mm});
            skLineSegment(sketch, "E745", {"start": v(4.22, -7.85) * mm, "end": v(5.5, -10.22) * mm});
            skLineSegment(sketch, "E746", {"start": v(5.5, -10.22) * mm, "end": v(7.37, -12.23) * mm});
            skLineSegment(sketch, "E747", {"start": v(7.37, -12.23) * mm, "end": v(9.02, -12.73) * mm});
            skLineSegment(sketch, "E748", {"start": v(9.02, -12.73) * mm, "end": v(10.1, -14.6) * mm});
            skLineSegment(sketch, "E749", {"start": v(10.1, -14.6) * mm, "end": v(11.1, -15.6) * mm});
            skLineSegment(sketch, "E750", {"start": v(11.1, -15.6) * mm, "end": v(12.53, -16.39) * mm});
            skLineSegment(sketch, "E751", {"start": v(12.53, -16.39) * mm, "end": v(14.83, -17.18) * mm});
            skLineSegment(sketch, "E752", {"start": v(14.83, -17.18) * mm, "end": v(14.9, -18.04) * mm});
            skLineSegment(sketch, "E753", {"start": v(14.9, -18.04) * mm, "end": v(16.4, -18.47) * mm});
            skLineSegment(sketch, "E754", {"start": v(16.4, -18.47) * mm, "end": v(16.55, -19.76) * mm});
            skLineSegment(sketch, "E755", {"start": v(16.55, -19.76) * mm, "end": v(18.27, -19.9) * mm});
            skLineSegment(sketch, "E756", {"start": v(18.27, -19.9) * mm, "end": v(18.41, -20.9) * mm});
            skLineSegment(sketch, "E757", {"start": v(18.41, -20.9) * mm, "end": v(17.48, -21.34) * mm});
            skLineSegment(sketch, "E758", {"start": v(17.48, -21.34) * mm, "end": v(16.62, -21.62) * mm});
            skLineSegment(sketch, "E759", {"start": v(16.62, -21.62) * mm, "end": v(16.4, -24.2) * mm});
            skLineSegment(sketch, "E760", {"start": v(16.4, -24.2) * mm, "end": v(16.4, -26.07) * mm});
            skLineSegment(sketch, "E761", {"start": v(16.4, -26.07) * mm, "end": v(16.84, -26.43) * mm});
            skLineSegment(sketch, "E762", {"start": v(16.84, -26.43) * mm, "end": v(17.84, -26.64) * mm});
            skLineSegment(sketch, "E763", {"start": v(17.84, -26.64) * mm, "end": v(17.91, -27.72) * mm});
            skLineSegment(sketch, "E764", {"start": v(17.91, -27.72) * mm, "end": v(17.98, -31.6) * mm});
            skLineSegment(sketch, "E765", {"start": v(17.98, -31.6) * mm, "end": v(17.7, -34.03) * mm});
            skLineSegment(sketch, "E766", {"start": v(17.7, -34.03) * mm, "end": v(17.71, -38.42) * mm});
            skLineSegment(sketch, "E767", {"start": v(17.71, -38.42) * mm, "end": v(26.44, -38.78) * mm});
            skLineSegment(sketch, "E768", {"start": v(26.44, -38.78) * mm, "end": v(26.37, -24.5) * mm});
            skLineSegment(sketch, "E769", {"start": v(26.37, -24.5) * mm, "end": v(28.02, -23.77) * mm});
            skLineSegment(sketch, "E770", {"start": v(28.02, -23.77) * mm, "end": v(27.95, -21.4) * mm});
            skLineSegment(sketch, "E771", {"start": v(27.95, -21.4) * mm, "end": v(27.02, -21.26) * mm});
            skLineSegment(sketch, "E772", {"start": v(27.02, -21.26) * mm, "end": v(26.8, -19.9) * mm});
            skLineSegment(sketch, "E773", {"start": v(26.8, -19.9) * mm, "end": v(28.02, -19.97) * mm});
            skLineSegment(sketch, "E774", {"start": v(28.02, -19.97) * mm, "end": v(28.67, -18.97) * mm});
            skLineSegment(sketch, "E775", {"start": v(28.67, -18.97) * mm, "end": v(31.54, -18.25) * mm});
            skLineSegment(sketch, "E776", {"start": v(31.54, -18.25) * mm, "end": v(33.11, -16.6) * mm});
            skLineSegment(sketch, "E777", {"start": v(33.11, -16.6) * mm, "end": v(35.77, -15.1) * mm});
            skLineSegment(sketch, "E778", {"start": v(35.77, -15.1) * mm, "end": v(37.63, -12.95) * mm});
            skLineSegment(sketch, "E779", {"start": v(37.63, -12.95) * mm, "end": v(37.92, -11.37) * mm});
            skLineSegment(sketch, "E780", {"start": v(37.92, -11.37) * mm, "end": v(40.72, -8.93) * mm});
            skLineSegment(sketch, "E781", {"start": v(40.72, -8.93) * mm, "end": v(41.43, -6.85) * mm});
            skLineSegment(sketch, "E782", {"start": v(41.43, -6.85) * mm, "end": v(41.58, -4.05) * mm});
            skLineSegment(sketch, "E783", {"start": v(41.58, -4.05) * mm, "end": v(44.73, -3.77) * mm});
            skLineSegment(sketch, "E784", {"start": v(44.73, -3.77) * mm, "end": v(44.59, -7.5) * mm});
            skLineSegment(sketch, "E785", {"start": v(44.59, -7.5) * mm, "end": v(45.74, -8.64) * mm});
            skLineSegment(sketch, "E786", {"start": v(45.74, -8.64) * mm, "end": v(45.52, -9.65) * mm});
            skLineSegment(sketch, "E787", {"start": v(45.52, -9.65) * mm, "end": v(43.94, -9.8) * mm});
            skLineSegment(sketch, "E788", {"start": v(43.94, -9.8) * mm, "end": v(43.58, -10.36) * mm});
            skLineSegment(sketch, "E789", {"start": v(43.58, -10.36) * mm, "end": v(46.3, -12.73) * mm});
            skLineSegment(sketch, "E790", {"start": v(46.3, -12.73) * mm, "end": v(48.6, -16.46) * mm});
            skLineSegment(sketch, "E791", {"start": v(48.6, -16.46) * mm, "end": v(49.25, -18.9) * mm});
            skLineSegment(sketch, "E792", {"start": v(49.25, -18.9) * mm, "end": v(50.4, -21.34) * mm});
            skLineSegment(sketch, "E793", {"start": v(50.4, -21.34) * mm, "end": v(51.83, -24.06) * mm});
            skLineSegment(sketch, "E794", {"start": v(51.83, -24.06) * mm, "end": v(52.65, -25.59) * mm});
            skLineSegment(sketch, "E795", {"start": v(52.65, -25.59) * mm, "end": v(52.55, -34.82) * mm});
            skLineSegment(sketch, "E796", {"start": v(52.55, -34.82) * mm, "end": v(50.76, -35.96) * mm});
            skLineSegment(sketch, "E797", {"start": v(50.76, -35.96) * mm, "end": v(49.47, -37.83) * mm});
            skLineSegment(sketch, "E798", {"start": v(49.47, -37.83) * mm, "end": v(46.6, -41.13) * mm});
            skLineSegment(sketch, "E799", {"start": v(46.6, -41.13) * mm, "end": v(43.8, -41.7) * mm});
            skLineSegment(sketch, "E800", {"start": v(43.8, -41.7) * mm, "end": v(43.01, -40.34) * mm});
            skLineSegment(sketch, "E801", {"start": v(43.01, -40.34) * mm, "end": v(40.86, -41.06) * mm});
            skLineSegment(sketch, "E802", {"start": v(40.86, -41.06) * mm, "end": v(38.56, -41.92) * mm});
            skLineSegment(sketch, "E803", {"start": v(38.56, -41.92) * mm, "end": v(32.68, -41.56) * mm});
            skLineSegment(sketch, "E804", {"start": v(32.68, -41.56) * mm, "end": v(28.81, -41.92) * mm});
            skLineSegment(sketch, "E805", {"start": v(28.81, -41.92) * mm, "end": v(27.66, -41.92) * mm});
            skLineSegment(sketch, "E806", {"start": v(27.66, -41.92) * mm, "end": v(26.8, -40.7) * mm});
            skLineSegment(sketch, "E807", {"start": v(26.8, -40.7) * mm, "end": v(21.78, -40.84) * mm});
            skLineSegment(sketch, "E808", {"start": v(21.78, -40.84) * mm, "end": v(20.35, -41.56) * mm});
            skLineSegment(sketch, "E809", {"start": v(20.35, -41.56) * mm, "end": v(19.63, -42.63) * mm});
            skLineSegment(sketch, "E810", {"start": v(19.63, -42.63) * mm, "end": v(15.19, -42.7) * mm});
            skLineSegment(sketch, "E811", {"start": v(15.19, -42.7) * mm, "end": v(13.6, -44) * mm});
            skLineSegment(sketch, "E812", {"start": v(13.6, -44) * mm, "end": v(3.35, -43.57) * mm});
            skLineSegment(sketch, "E813", {"start": v(3.35, -43.57) * mm, "end": v(2.5, -42.35) * mm});
            skLineSegment(sketch, "E814", {"start": v(2.5, -42.35) * mm, "end": v(0.99, -42.13) * mm});
            skLineSegment(sketch, "E815", {"start": v(0.99, -42.13) * mm, "end": v(-2.45, -39.55) * mm});
            skLineSegment(sketch, "E816", {"start": v(-2.45, -39.55) * mm, "end": v(-4.96, -36.32) * mm});
            skLineSegment(sketch, "E817", {"start": v(-4.96, -36.32) * mm, "end": v(-6.9, -33.45) * mm});
            skLineSegment(sketch, "E818", {"start": v(-6.9, -33.45) * mm, "end": v(-8.7, -31.66) * mm});
            skLineSegment(sketch, "E819", {"start": v(-8.7, -31.66) * mm, "end": v(-8.7, -28.08) * mm});
            skLineSegment(sketch, "E820", {"start": v(-8.7, -28.08) * mm, "end": v(-7.47, -23.99) * mm});
            skLineSegment(sketch, "E821", {"start": v(-7.47, -23.99) * mm, "end": v(-5.32, -20.19) * mm});
            skLineSegment(sketch, "E822", {"start": v(-5.32, -20.19) * mm, "end": v(-4.9, -17.97) * mm});
            skLineSegment(sketch, "E823", {"start": v(-4.9, -17.97) * mm, "end": v(-2.41, -17.03) * mm});
            skLineSegment(sketch, "E824", {"start": v(-2.41, -17.03) * mm, "end": v(-2.41, -15.02) * mm});
            skLineSegment(sketch, "E825", {"start": v(-2.41, -15.02) * mm, "end": v(-1.45, -12.66) * mm});
            skLineSegment(sketch, "E826", {"start": v(-1.45, -12.66) * mm, "end": v(-0.52, -10.5) * mm});
            skLineSegment(sketch, "E827", {"start": v(-0.52, -10.5) * mm, "end": v(0.85, -8.64) * mm});
            skLineSegment(sketch, "E828", {"start": v(0.85, -8.64) * mm, "end": v(0.99, -7.93) * mm});
            skLineSegment(sketch, "E829", {"start": v(0.99, -7.93) * mm, "end": v(4.22, -7.85) * mm});
            skLineSegment(sketch, "E830", {"start": v(1.78, -13.32) * mm, "end": v(5.69, -14.32) * mm});
            skLineSegment(sketch, "E831", {"start": v(5.69, -14.32) * mm, "end": v(9.65, -16.88) * mm});
            skLineSegment(sketch, "E832", {"start": v(9.65, -16.88) * mm, "end": v(11.56, -19.3) * mm});
            skLineSegment(sketch, "E833", {"start": v(11.56, -19.3) * mm, "end": v(11.46, -25.49) * mm});
            skLineSegment(sketch, "E834", {"start": v(11.46, -25.49) * mm, "end": v(8.24, -25.44) * mm});
            skLineSegment(sketch, "E835", {"start": v(8.24, -25.44) * mm, "end": v(7, -27.16) * mm});
            skLineSegment(sketch, "E836", {"start": v(7, -27.16) * mm, "end": v(4.8, -27.9) * mm});
            skLineSegment(sketch, "E837", {"start": v(4.8, -27.9) * mm, "end": v(4.46, -25.97) * mm});
            skLineSegment(sketch, "E838", {"start": v(4.46, -25.97) * mm, "end": v(4.55, -18.5) * mm});
            skLineSegment(sketch, "E839", {"start": v(4.55, -18.5) * mm, "end": v(3.78, -18.46) * mm});
            skLineSegment(sketch, "E840", {"start": v(3.78, -18.46) * mm, "end": v(3.62, -28.6) * mm});
            skLineSegment(sketch, "E841", {"start": v(3.62, -28.6) * mm, "end": v(1.85, -29.79) * mm});
            skLineSegment(sketch, "E842", {"start": v(1.85, -29.79) * mm, "end": v(1.85, -39.5) * mm});
            skLineSegment(sketch, "E843", {"start": v(1.85, -39.5) * mm, "end": v(-0.1, -39.16) * mm});
            skLineSegment(sketch, "E844", {"start": v(-0.1, -39.16) * mm, "end": v(-0.2, -36.05) * mm});
            skLineSegment(sketch, "E845", {"start": v(-0.2, -36.05) * mm, "end": v(-1.98, -36.05) * mm});
            skLineSegment(sketch, "E846", {"start": v(-1.98, -36.05) * mm, "end": v(-5.94, -31.2) * mm});
            skLineSegment(sketch, "E847", {"start": v(-5.94, -31.2) * mm, "end": v(-6.33, -25.31) * mm});
            skLineSegment(sketch, "E848", {"start": v(-6.33, -25.31) * mm, "end": v(-3.19, -19.02) * mm});
            skLineSegment(sketch, "E849", {"start": v(-3.19, -19.02) * mm, "end": v(0, -15.02) * mm});
            skLineSegment(sketch, "E850", {"start": v(0, -15.02) * mm, "end": v(1.78, -13.32) * mm});
            skLineSegment(sketch, "E851", {"start": v(3.79, -30.34) * mm, "end": v(3.79, -38.96) * mm});
            skLineSegment(sketch, "E852", {"start": v(3.79, -38.96) * mm, "end": v(5.48, -39.04) * mm});
            skLineSegment(sketch, "E853", {"start": v(5.48, -39.04) * mm, "end": v(7.25, -41.53) * mm});
            skLineSegment(sketch, "E854", {"start": v(7.25, -41.53) * mm, "end": v(13.69, -41.53) * mm});
            skLineSegment(sketch, "E855", {"start": v(13.69, -41.53) * mm, "end": v(13.69, -35.1) * mm});
            skLineSegment(sketch, "E856", {"start": v(13.69, -35.1) * mm, "end": v(12.48, -34.29) * mm});
            skLineSegment(sketch, "E857", {"start": v(12.48, -34.29) * mm, "end": v(12.56, -27.53) * mm});
            skLineSegment(sketch, "E858", {"start": v(12.56, -27.53) * mm, "end": v(8.7, -27.6) * mm});
            skLineSegment(sketch, "E859", {"start": v(8.7, -27.6) * mm, "end": v(7.4, -29.05) * mm});
            skLineSegment(sketch, "E860", {"start": v(7.4, -29.05) * mm, "end": v(6.04, -29.78) * mm});
            skLineSegment(sketch, "E861", {"start": v(6.04, -29.78) * mm, "end": v(3.79, -30.34) * mm});
            skLineSegment(sketch, "E862", {"start": v(13.11, -19.96) * mm, "end": v(13.11, -23.88) * mm});
            skLineSegment(sketch, "E863", {"start": v(13.11, -23.88) * mm, "end": v(15.58, -23.94) * mm});
            skLineSegment(sketch, "E864", {"start": v(15.58, -23.94) * mm, "end": v(15.58, -20.02) * mm});
            skLineSegment(sketch, "E865", {"start": v(15.58, -20.02) * mm, "end": v(13.11, -19.96) * mm});
            skLineSegment(sketch, "E866", {"start": v(12.95, -26.09) * mm, "end": v(12.95, -27.12) * mm});
            skLineSegment(sketch, "E867", {"start": v(12.95, -27.12) * mm, "end": v(14.03, -27.2) * mm});
            skLineSegment(sketch, "E868", {"start": v(14.03, -27.2) * mm, "end": v(14.4, -27.68) * mm});
            skLineSegment(sketch, "E869", {"start": v(14.4, -27.68) * mm, "end": v(14.3, -30.1) * mm});
            skLineSegment(sketch, "E870", {"start": v(14.3, -30.1) * mm, "end": v(16.41, -30.1) * mm});
            skLineSegment(sketch, "E871", {"start": v(16.41, -30.1) * mm, "end": v(16.56, -27.42) * mm});
            skLineSegment(sketch, "E872", {"start": v(16.56, -27.42) * mm, "end": v(15.37, -27.35) * mm});
            skLineSegment(sketch, "E873", {"start": v(15.37, -27.35) * mm, "end": v(14.84, -26.97) * mm});
            skLineSegment(sketch, "E874", {"start": v(14.84, -26.97) * mm, "end": v(14.66, -25.4) * mm});
            skLineSegment(sketch, "E875", {"start": v(14.66, -25.4) * mm, "end": v(12.91, -25.4) * mm});
            skLineSegment(sketch, "E876", {"start": v(12.91, -25.4) * mm, "end": v(12.95, -26.09) * mm});
            skLineSegment(sketch, "E877", {"start": v(14.33, -31.97) * mm, "end": v(14.33, -33.94) * mm});
            skLineSegment(sketch, "E878", {"start": v(14.33, -33.94) * mm, "end": v(15.43, -33.94) * mm});
            skLineSegment(sketch, "E879", {"start": v(15.43, -33.94) * mm, "end": v(15.67, -33.38) * mm});
            skLineSegment(sketch, "E880", {"start": v(15.67, -33.38) * mm, "end": v(16.8, -33.4) * mm});
            skLineSegment(sketch, "E881", {"start": v(16.8, -33.4) * mm, "end": v(16.72, -30.66) * mm});
            skLineSegment(sketch, "E882", {"start": v(16.72, -30.66) * mm, "end": v(16.1, -30.58) * mm});
            skLineSegment(sketch, "E883", {"start": v(16.1, -30.58) * mm, "end": v(15.57, -31.4) * mm});
            skLineSegment(sketch, "E884", {"start": v(15.57, -31.4) * mm, "end": v(14.83, -31.97) * mm});
            skLineSegment(sketch, "E885", {"start": v(14.83, -31.97) * mm, "end": v(14.33, -31.97) * mm});
            skLineSegment(sketch, "E886", {"start": v(15.12, -35.6) * mm, "end": v(15.12, -38.78) * mm});
            skLineSegment(sketch, "E887", {"start": v(15.12, -38.78) * mm, "end": v(16.9, -38.75) * mm});
            skLineSegment(sketch, "E888", {"start": v(16.9, -38.75) * mm, "end": v(16.83, -34.82) * mm});
            skLineSegment(sketch, "E889", {"start": v(16.83, -34.82) * mm, "end": v(15.45, -34.85) * mm});
            skLineSegment(sketch, "E890", {"start": v(15.45, -34.85) * mm, "end": v(15.12, -35.6) * mm});
            skLineSegment(sketch, "E891", {"start": v(31.22, -32.46) * mm, "end": v(32.7, -32.46) * mm});
            skLineSegment(sketch, "E892", {"start": v(32.7, -32.46) * mm, "end": v(33.5, -28.66) * mm});
            skLineSegment(sketch, "E893", {"start": v(33.5, -28.66) * mm, "end": v(34.83, -27.25) * mm});
            skLineSegment(sketch, "E894", {"start": v(34.83, -27.25) * mm, "end": v(36.5, -26.04) * mm});
            skLineSegment(sketch, "E895", {"start": v(36.5, -26.04) * mm, "end": v(38.94, -24.33) * mm});
            skLineSegment(sketch, "E896", {"start": v(38.94, -24.33) * mm, "end": v(40.66, -23.2) * mm});
            skLineSegment(sketch, "E897", {"start": v(40.66, -23.2) * mm, "end": v(41.02, -18.77) * mm});
            skLineSegment(sketch, "E898", {"start": v(41.02, -18.77) * mm, "end": v(42.51, -17.05) * mm});
            skLineSegment(sketch, "E899", {"start": v(42.51, -17.05) * mm, "end": v(43.19, -17.46) * mm});
            skLineSegment(sketch, "E900", {"start": v(43.19, -17.46) * mm, "end": v(41.74, -19.13) * mm});
            skLineSegment(sketch, "E901", {"start": v(41.74, -19.13) * mm, "end": v(41.6, -23.56) * mm});
            skLineSegment(sketch, "E902", {"start": v(41.6, -23.56) * mm, "end": v(42.47, -28.26) * mm});
            skLineSegment(sketch, "E903", {"start": v(42.47, -28.26) * mm, "end": v(43.33, -28.8) * mm});
            skLineSegment(sketch, "E904", {"start": v(43.33, -28.8) * mm, "end": v(43.33, -38.26) * mm});
            skLineSegment(sketch, "E905", {"start": v(43.33, -38.26) * mm, "end": v(44.48, -39) * mm});
            skLineSegment(sketch, "E906", {"start": v(44.48, -39) * mm, "end": v(45.83, -38.87) * mm});
            skLineSegment(sketch, "E907", {"start": v(45.83, -38.87) * mm, "end": v(47.39, -37.72) * mm});
            skLineSegment(sketch, "E908", {"start": v(47.39, -37.72) * mm, "end": v(48.06, -36.3) * mm});
            skLineSegment(sketch, "E909", {"start": v(48.06, -36.3) * mm, "end": v(47.72, -35.7) * mm});
            skLineSegment(sketch, "E910", {"start": v(47.72, -35.7) * mm, "end": v(48.2, -34.47) * mm});
            skLineSegment(sketch, "E911", {"start": v(48.2, -34.47) * mm, "end": v(49.35, -33.46) * mm});
            skLineSegment(sketch, "E912", {"start": v(49.35, -33.46) * mm, "end": v(50.77, -33.52) * mm});
            skLineSegment(sketch, "E913", {"start": v(50.77, -33.52) * mm, "end": v(50.77, -31.63) * mm});
            skLineSegment(sketch, "E914", {"start": v(50.77, -31.63) * mm, "end": v(50.7, -28.92) * mm});
            skLineSegment(sketch, "E915", {"start": v(50.7, -28.92) * mm, "end": v(50.64, -27.7) * mm});
            skLineSegment(sketch, "E916", {"start": v(50.64, -27.7) * mm, "end": v(49.01, -27.3) * mm});
            skLineSegment(sketch, "E917", {"start": v(49.01, -27.3) * mm, "end": v(49.08, -25.4) * mm});
            skLineSegment(sketch, "E918", {"start": v(49.08, -25.4) * mm, "end": v(48.8, -23.5) * mm});
            skLineSegment(sketch, "E919", {"start": v(48.8, -23.5) * mm, "end": v(47.93, -22.83) * mm});
            skLineSegment(sketch, "E920", {"start": v(47.93, -22.83) * mm, "end": v(47.66, -21.48) * mm});
            skLineSegment(sketch, "E921", {"start": v(47.66, -21.48) * mm, "end": v(47.25, -19.99) * mm});
            skLineSegment(sketch, "E922", {"start": v(47.25, -19.99) * mm, "end": v(46.91, -18.5) * mm});
            skLineSegment(sketch, "E923", {"start": v(46.91, -18.5) * mm, "end": v(46.17, -16.87) * mm});
            skLineSegment(sketch, "E924", {"start": v(46.17, -16.87) * mm, "end": v(44.75, -15.38) * mm});
            skLineSegment(sketch, "E925", {"start": v(44.75, -15.38) * mm, "end": v(43.93, -13.62) * mm});
            skLineSegment(sketch, "E926", {"start": v(43.93, -13.62) * mm, "end": v(42.78, -12.2) * mm});
            skLineSegment(sketch, "E927", {"start": v(42.78, -12.2) * mm, "end": v(41.77, -12) * mm});
            skLineSegment(sketch, "E928", {"start": v(41.77, -12) * mm, "end": v(40.89, -13.42) * mm});
            skLineSegment(sketch, "E929", {"start": v(40.89, -13.42) * mm, "end": v(39.74, -14.84) * mm});
            skLineSegment(sketch, "E930", {"start": v(39.74, -14.84) * mm, "end": v(38.59, -16.74) * mm});
            skLineSegment(sketch, "E931", {"start": v(38.59, -16.74) * mm, "end": v(37.1, -18.3) * mm});
            skLineSegment(sketch, "E932", {"start": v(37.1, -18.3) * mm, "end": v(34.86, -18.77) * mm});
            skLineSegment(sketch, "E933", {"start": v(34.86, -18.77) * mm, "end": v(33.71, -19.65) * mm});
            skLineSegment(sketch, "E934", {"start": v(33.71, -19.65) * mm, "end": v(31.62, -20.33) * mm});
            skLineSegment(sketch, "E935", {"start": v(31.62, -20.33) * mm, "end": v(31.14, -21.4) * mm});
            skLineSegment(sketch, "E936", {"start": v(31.14, -21.4) * mm, "end": v(31.22, -32.46) * mm});
            skLineSegment(sketch, "E937", {"start": v(30.3, -39.66) * mm, "end": v(31.08, -37.58) * mm});
            skLineSegment(sketch, "E938", {"start": v(31.08, -37.58) * mm, "end": v(32.59, -35.93) * mm});
            skLineSegment(sketch, "E939", {"start": v(32.59, -35.93) * mm, "end": v(33.38, -33.78) * mm});
            skLineSegment(sketch, "E940", {"start": v(33.38, -33.78) * mm, "end": v(33.98, -31.18) * mm});
            skLineSegment(sketch, "E941", {"start": v(33.98, -31.18) * mm, "end": v(34.53, -29.2) * mm});
            skLineSegment(sketch, "E942", {"start": v(34.53, -29.2) * mm, "end": v(36.17, -27.54) * mm});
            skLineSegment(sketch, "E943", {"start": v(36.17, -27.54) * mm, "end": v(38.68, -26.04) * mm});
            skLineSegment(sketch, "E944", {"start": v(38.68, -26.04) * mm, "end": v(40.48, -25.18) * mm});
            skLineSegment(sketch, "E945", {"start": v(40.48, -25.18) * mm, "end": v(40.62, -30.12) * mm});
            skLineSegment(sketch, "E946", {"start": v(40.62, -30.12) * mm, "end": v(41.62, -31.34) * mm});
            skLineSegment(sketch, "E947", {"start": v(41.62, -31.34) * mm, "end": v(41.62, -37.15) * mm});
            skLineSegment(sketch, "E948", {"start": v(41.62, -37.15) * mm, "end": v(40.7, -38.8) * mm});
            skLineSegment(sketch, "E949", {"start": v(40.7, -38.8) * mm, "end": v(39.47, -39.95) * mm});
            skLineSegment(sketch, "E950", {"start": v(39.47, -39.95) * mm, "end": v(30.87, -40.23) * mm});
            skLineSegment(sketch, "E951", {"start": v(30.87, -40.23) * mm, "end": v(30.3, -39.66) * mm});
            skLineSegment(sketch, "E952.bottom", {"start": v(28.71, -21.41) * mm, "end": v(30.22, -21.41) * mm});
            skLineSegment(sketch, "E952.top", {"start": v(28.71, -24) * mm, "end": v(30.22, -24) * mm});
            skLineSegment(sketch, "E952.left", {"start": v(28.71, -21.41) * mm, "end": v(28.71, -24) * mm});
            skLineSegment(sketch, "E952.right", {"start": v(30.22, -21.41) * mm, "end": v(30.22, -24) * mm});
            skLineSegment(sketch, "E953.bottom", {"start": v(27.36, -34.55) * mm, "end": v(29.23, -34.55) * mm});
            skLineSegment(sketch, "E953.top", {"start": v(27.36, -39.2) * mm, "end": v(29.23, -39.2) * mm});
            skLineSegment(sketch, "E953.left", {"start": v(27.36, -34.55) * mm, "end": v(27.36, -39.2) * mm});
            skLineSegment(sketch, "E953.right", {"start": v(29.23, -34.55) * mm, "end": v(29.23, -39.2) * mm});
            skLineSegment(sketch, "E954", {"start": v(27.72, -26.23) * mm, "end": v(27.73, -28.94) * mm});
            skLineSegment(sketch, "E955", {"start": v(27.73, -28.94) * mm, "end": v(30.01, -29.12) * mm});
            skLineSegment(sketch, "E956", {"start": v(30.01, -29.12) * mm, "end": v(29.95, -25.14) * mm});
            skLineSegment(sketch, "E957", {"start": v(29.95, -25.14) * mm, "end": v(27.72, -26.23) * mm});
            skLineSegment(sketch, "E958", {"start": v(27.54, -30.09) * mm, "end": v(27.54, -33.1) * mm});
            skLineSegment(sketch, "E959", {"start": v(27.54, -33.1) * mm, "end": v(29.54, -33.26) * mm});
            skLineSegment(sketch, "E960", {"start": v(29.54, -33.26) * mm, "end": v(29.92, -33.45) * mm});
            skLineSegment(sketch, "E961", {"start": v(29.92, -33.45) * mm, "end": v(29.83, -35.94) * mm});
            skLineSegment(sketch, "E962", {"start": v(29.83, -35.94) * mm, "end": v(31.4, -36.06) * mm});
            skLineSegment(sketch, "E963", {"start": v(31.4, -36.06) * mm, "end": v(31.52, -33.29) * mm});
            skLineSegment(sketch, "E964", {"start": v(31.52, -33.29) * mm, "end": v(30.25, -32.62) * mm});
            skLineSegment(sketch, "E965", {"start": v(30.25, -32.62) * mm, "end": v(30.13, -30.21) * mm});
            skLineSegment(sketch, "E966", {"start": v(30.13, -30.21) * mm, "end": v(27.54, -30.09) * mm});
            skLineSegment(sketch, "E967", {"start": v(7.75, -45.8) * mm, "end": v(9.85, -45.8) * mm});
            skLineSegment(sketch, "E968", {"start": v(9.85, -45.8) * mm, "end": v(9.66, -47.8) * mm});
            skLineSegment(sketch, "E969", {"start": v(9.66, -47.8) * mm, "end": v(8.6, -49.14) * mm});
            skLineSegment(sketch, "E970", {"start": v(8.6, -49.14) * mm, "end": v(8.33, -55.16) * mm});
            skLineSegment(sketch, "E971", {"start": v(8.33, -55.16) * mm, "end": v(7.17, -56.03) * mm});
            skLineSegment(sketch, "E972", {"start": v(7.17, -56.03) * mm, "end": v(7.36, -62.16) * mm});
            skLineSegment(sketch, "E973", {"start": v(7.36, -62.16) * mm, "end": v(9.09, -61.97) * mm});
            skLineSegment(sketch, "E974", {"start": v(9.09, -61.97) * mm, "end": v(9.18, -56.7) * mm});
            skLineSegment(sketch, "E975", {"start": v(9.18, -56.7) * mm, "end": v(10.52, -54.79) * mm});
            skLineSegment(sketch, "E976", {"start": v(10.52, -54.79) * mm, "end": v(10.43, -49.62) * mm});
            skLineSegment(sketch, "E977", {"start": v(10.43, -49.62) * mm, "end": v(12.44, -47.13) * mm});
            skLineSegment(sketch, "E978", {"start": v(12.44, -47.13) * mm, "end": v(13.97, -48.37) * mm});
            skLineSegment(sketch, "E979", {"start": v(13.97, -48.37) * mm, "end": v(12.72, -49.81) * mm});
            skLineSegment(sketch, "E980", {"start": v(12.72, -49.81) * mm, "end": v(13.1, -55.17) * mm});
            skLineSegment(sketch, "E981", {"start": v(13.1, -55.17) * mm, "end": v(11.86, -56.7) * mm});
            skLineSegment(sketch, "E982", {"start": v(11.86, -56.7) * mm, "end": v(11.96, -62.25) * mm});
            skLineSegment(sketch, "E983", {"start": v(11.96, -62.25) * mm, "end": v(12.72, -63.7) * mm});
            skLineSegment(sketch, "E984", {"start": v(12.72, -63.7) * mm, "end": v(22.58, -63.79) * mm});
            skLineSegment(sketch, "E985", {"start": v(22.58, -63.79) * mm, "end": v(22.97, -56.6) * mm});
            skLineSegment(sketch, "E986", {"start": v(22.97, -56.6) * mm, "end": v(24.21, -56.42) * mm});
            skLineSegment(sketch, "E987", {"start": v(24.21, -56.42) * mm, "end": v(24.4, -50.48) * mm});
            skLineSegment(sketch, "E988", {"start": v(24.4, -50.48) * mm, "end": v(25.93, -49.14) * mm});
            skLineSegment(sketch, "E989", {"start": v(25.93, -49.14) * mm, "end": v(27.94, -50.86) * mm});
            skLineSegment(sketch, "E990", {"start": v(27.94, -50.86) * mm, "end": v(27.94, -54.02) * mm});
            skLineSegment(sketch, "E991", {"start": v(27.94, -54.02) * mm, "end": v(29.57, -55.65) * mm});
            skLineSegment(sketch, "E992", {"start": v(29.57, -55.65) * mm, "end": v(29.38, -63.21) * mm});
            skLineSegment(sketch, "E993", {"start": v(29.38, -63.21) * mm, "end": v(35.89, -63.21) * mm});
            skLineSegment(sketch, "E994", {"start": v(35.89, -63.21) * mm, "end": v(36.08, -59.38) * mm});
            skLineSegment(sketch, "E995", {"start": v(36.08, -59.38) * mm, "end": v(34.55, -57.95) * mm});
            skLineSegment(sketch, "E996", {"start": v(34.55, -57.95) * mm, "end": v(34.74, -44.64) * mm});
            skLineSegment(sketch, "E997", {"start": v(34.74, -44.64) * mm, "end": v(37.61, -44.74) * mm});
            skLineSegment(sketch, "E998", {"start": v(37.61, -44.74) * mm, "end": v(37.61, -51.73) * mm});
            skLineSegment(sketch, "E999", {"start": v(37.61, -51.73) * mm, "end": v(39.34, -53.16) * mm});
            skLineSegment(sketch, "E1000", {"start": v(39.34, -53.16) * mm, "end": v(38.57, -62.06) * mm});
            skLineSegment(sketch, "E1001", {"start": v(38.57, -62.06) * mm, "end": v(40.2, -63.5) * mm});
            skLineSegment(sketch, "E1002", {"start": v(40.2, -63.5) * mm, "end": v(42.02, -62.45) * mm});
            skLineSegment(sketch, "E1003", {"start": v(42.02, -62.45) * mm, "end": v(45.56, -62.35) * mm});
            skLineSegment(sketch, "E1004", {"start": v(45.56, -62.35) * mm, "end": v(45.56, -55.08) * mm});
            skLineSegment(sketch, "E1005", {"start": v(45.56, -55.08) * mm, "end": v(44.6, -54.02) * mm});
            skLineSegment(sketch, "E1006", {"start": v(44.6, -54.02) * mm, "end": v(44.4, -49.24) * mm});
            skLineSegment(sketch, "E1007", {"start": v(44.4, -49.24) * mm, "end": v(43.36, -46.27) * mm});
            skLineSegment(sketch, "E1008", {"start": v(43.36, -46.27) * mm, "end": v(43.74, -44.64) * mm});
            skLineSegment(sketch, "E1009", {"start": v(43.74, -44.64) * mm, "end": v(45.46, -44.74) * mm});
            skLineSegment(sketch, "E1010", {"start": v(45.46, -44.74) * mm, "end": v(45.46, -47.03) * mm});
            skLineSegment(sketch, "E1011", {"start": v(45.46, -47.03) * mm, "end": v(46.42, -48.57) * mm});
            skLineSegment(sketch, "E1012", {"start": v(46.42, -48.57) * mm, "end": v(46.32, -52.59) * mm});
            skLineSegment(sketch, "E1013", {"start": v(46.32, -52.59) * mm, "end": v(47.28, -54.12) * mm});
            skLineSegment(sketch, "E1014", {"start": v(47.28, -54.12) * mm, "end": v(47.28, -64.26) * mm});
            skLineSegment(sketch, "E1015", {"start": v(47.28, -64.26) * mm, "end": v(43.07, -64.07) * mm});
            skLineSegment(sketch, "E1016", {"start": v(43.07, -64.07) * mm, "end": v(41.92, -65.9) * mm});
            skLineSegment(sketch, "E1017", {"start": v(41.92, -65.9) * mm, "end": v(29, -66.18) * mm});
            skLineSegment(sketch, "E1018", {"start": v(29, -66.18) * mm, "end": v(27.66, -63.88) * mm});
            skLineSegment(sketch, "E1019", {"start": v(27.66, -63.88) * mm, "end": v(27.66, -56.22) * mm});
            skLineSegment(sketch, "E1020", {"start": v(27.66, -56.22) * mm, "end": v(26.5, -55.08) * mm});
            skLineSegment(sketch, "E1021", {"start": v(26.5, -55.08) * mm, "end": v(26.6, -51.25) * mm});
            skLineSegment(sketch, "E1022", {"start": v(26.6, -51.25) * mm, "end": v(25.63, -51.22) * mm});
            skLineSegment(sketch, "E1023", {"start": v(25.63, -51.22) * mm, "end": v(25.38, -58.34) * mm});
            skLineSegment(sketch, "E1024", {"start": v(25.38, -58.34) * mm, "end": v(24.42, -58.64) * mm});
            skLineSegment(sketch, "E1025", {"start": v(24.42, -58.64) * mm, "end": v(24.18, -64.3) * mm});
            skLineSegment(sketch, "E1026", {"start": v(24.18, -64.3) * mm, "end": v(22.19, -65.87) * mm});
            skLineSegment(sketch, "E1027", {"start": v(22.19, -65.87) * mm, "end": v(11.7, -65.57) * mm});
            skLineSegment(sketch, "E1028", {"start": v(11.7, -65.57) * mm, "end": v(10.66, -64.13) * mm});
            skLineSegment(sketch, "E1029", {"start": v(10.66, -64.13) * mm, "end": v(6.2, -64.03) * mm});
            skLineSegment(sketch, "E1030", {"start": v(6.2, -64.03) * mm, "end": v(5.6, -62.56) * mm});
            skLineSegment(sketch, "E1031", {"start": v(5.6, -62.56) * mm, "end": v(5.55, -55.5) * mm});
            skLineSegment(sketch, "E1032", {"start": v(5.55, -55.5) * mm, "end": v(6.57, -54.42) * mm});
            skLineSegment(sketch, "E1033", {"start": v(6.57, -54.42) * mm, "end": v(6.63, -47.9) * mm});
            skLineSegment(sketch, "E1034", {"start": v(6.63, -47.9) * mm, "end": v(7.75, -45.8) * mm});
            skLineSegment(sketch, "E1035", {"start": v(2.25, -75.54) * mm, "end": v(2.25, -71.7) * mm});
            skLineSegment(sketch, "E1036", {"start": v(2.25, -71.7) * mm, "end": v(4.8, -68.32) * mm});
            skLineSegment(sketch, "E1037", {"start": v(4.8, -68.32) * mm, "end": v(8.83, -68.32) * mm});
            skLineSegment(sketch, "E1038", {"start": v(8.83, -68.32) * mm, "end": v(10.68, -69.98) * mm});
            skLineSegment(sketch, "E1039", {"start": v(10.68, -69.98) * mm, "end": v(12.54, -70.36) * mm});
            skLineSegment(sketch, "E1040", {"start": v(12.54, -70.36) * mm, "end": v(13.56, -71.51) * mm});
            skLineSegment(sketch, "E1041", {"start": v(13.56, -71.51) * mm, "end": v(13.45, -73.94) * mm});
            skLineSegment(sketch, "E1042", {"start": v(13.45, -73.94) * mm, "end": v(18.03, -73.88) * mm});
            skLineSegment(sketch, "E1043", {"start": v(18.03, -73.88) * mm, "end": v(18.1, -75.98) * mm});
            skLineSegment(sketch, "E1044", {"start": v(18.1, -75.98) * mm, "end": v(2.25, -75.96) * mm});
            skLineSegment(sketch, "E1045", {"start": v(2.25, -75.96) * mm, "end": v(2.25, -75.54) * mm});
            skLineSegment(sketch, "E1046", {"start": v(11.54, -68.35) * mm, "end": v(11.54, -69.68) * mm});
            skLineSegment(sketch, "E1047", {"start": v(11.54, -69.68) * mm, "end": v(12.62, -69.9) * mm});
            skLineSegment(sketch, "E1048", {"start": v(12.62, -69.9) * mm, "end": v(13.9, -71.3) * mm});
            skLineSegment(sketch, "E1049", {"start": v(13.9, -71.3) * mm, "end": v(13.92, -73.48) * mm});
            skLineSegment(sketch, "E1050", {"start": v(13.92, -73.48) * mm, "end": v(17.54, -73.42) * mm});
            skLineSegment(sketch, "E1051", {"start": v(17.54, -73.42) * mm, "end": v(17.39, -68.23) * mm});
            skLineSegment(sketch, "E1052", {"start": v(17.39, -68.23) * mm, "end": v(11.5, -68.11) * mm});
            skLineSegment(sketch, "E1053", {"start": v(11.5, -68.11) * mm, "end": v(11.54, -68.35) * mm});
            skLineSegment(sketch, "E1054", {"start": v(30.75, -73.84) * mm, "end": v(30.75, -76.04) * mm});
            skLineSegment(sketch, "E1055", {"start": v(30.75, -76.04) * mm, "end": v(38.8, -76.16) * mm});
            skLineSegment(sketch, "E1056", {"start": v(38.8, -76.16) * mm, "end": v(38.73, -73.72) * mm});
            skLineSegment(sketch, "E1057", {"start": v(38.73, -73.72) * mm, "end": v(30.75, -73.84) * mm});
            skLineSegment(sketch, "E1058", {"start": v(32.87, -66.87) * mm, "end": v(32.87, -69.13) * mm});
            skLineSegment(sketch, "E1059", {"start": v(32.87, -69.13) * mm, "end": v(31.86, -69.2) * mm});
            skLineSegment(sketch, "E1060", {"start": v(31.86, -69.2) * mm, "end": v(31.78, -73.31) * mm});
            skLineSegment(sketch, "E1061", {"start": v(31.78, -73.31) * mm, "end": v(38.82, -73.27) * mm});
            skLineSegment(sketch, "E1062", {"start": v(38.82, -73.27) * mm, "end": v(39.87, -72.43) * mm});
            skLineSegment(sketch, "E1063", {"start": v(39.87, -72.43) * mm, "end": v(40.47, -71.3) * mm});
            skLineSegment(sketch, "E1064", {"start": v(40.47, -71.3) * mm, "end": v(41.2, -70.7) * mm});
            skLineSegment(sketch, "E1065", {"start": v(41.2, -70.7) * mm, "end": v(42.32, -69.97) * mm});
            skLineSegment(sketch, "E1066", {"start": v(42.32, -69.97) * mm, "end": v(42.77, -68.72) * mm});
            skLineSegment(sketch, "E1067", {"start": v(42.77, -68.72) * mm, "end": v(35.72, -68.8) * mm});
            skLineSegment(sketch, "E1068", {"start": v(35.72, -68.8) * mm, "end": v(35.76, -66.95) * mm});
            skLineSegment(sketch, "E1069", {"start": v(35.76, -66.95) * mm, "end": v(32.87, -66.87) * mm});
            skLineSegment(sketch, "E1070", {"start": v(39.3, -73.5) * mm, "end": v(40.25, -72.79) * mm});
            skLineSegment(sketch, "E1071", {"start": v(40.25, -72.79) * mm, "end": v(40.8, -71.56) * mm});
            skLineSegment(sketch, "E1072", {"start": v(40.8, -71.56) * mm, "end": v(41.66, -70.82) * mm});
            skLineSegment(sketch, "E1073", {"start": v(41.66, -70.82) * mm, "end": v(42.57, -70.46) * mm});
            skLineSegment(sketch, "E1074", {"start": v(42.57, -70.46) * mm, "end": v(43.53, -69) * mm});
            skLineSegment(sketch, "E1075", {"start": v(43.53, -69) * mm, "end": v(45.2, -68.78) * mm});
            skLineSegment(sketch, "E1076", {"start": v(45.2, -68.78) * mm, "end": v(45.66, -68.08) * mm});
            skLineSegment(sketch, "E1077", {"start": v(45.66, -68.08) * mm, "end": v(48.93, -68.05) * mm});
            skLineSegment(sketch, "E1078", {"start": v(48.93, -68.05) * mm, "end": v(50.01, -69.2) * mm});
            skLineSegment(sketch, "E1079", {"start": v(50.01, -69.2) * mm, "end": v(50.9, -69.43) * mm});
            skLineSegment(sketch, "E1080", {"start": v(50.9, -69.43) * mm, "end": v(52.02, -70.02) * mm});
            skLineSegment(sketch, "E1081", {"start": v(52.02, -70.02) * mm, "end": v(52.69, -70.72) * mm});
            skLineSegment(sketch, "E1082", {"start": v(52.69, -70.72) * mm, "end": v(53.01, -71.45) * mm});
            skLineSegment(sketch, "E1083", {"start": v(53.01, -71.45) * mm, "end": v(53.4, -73.26) * mm});
            skLineSegment(sketch, "E1084", {"start": v(53.4, -73.26) * mm, "end": v(52.4, -75.1) * mm});
            skLineSegment(sketch, "E1085", {"start": v(52.4, -75.1) * mm, "end": v(51.08, -76.02) * mm});
            skLineSegment(sketch, "E1086", {"start": v(51.08, -76.02) * mm, "end": v(39.2, -76.08) * mm});
            skLineSegment(sketch, "E1087", {"start": v(39.2, -76.08) * mm, "end": v(39.14, -73.7) * mm});
            skLineSegment(sketch, "E1088", {"start": v(39.14, -73.7) * mm, "end": v(39.3, -73.5) * mm});
            skLineSegment(sketch, "E1089", {"start": v(4.88, -27.78) * mm, "end": v(6.96, -27.07) * mm});
            skLineSegment(sketch, "E1090", {"start": v(6.96, -27.07) * mm, "end": v(8.17, -25.39) * mm});
            skLineSegment(sketch, "E1091", {"start": v(8.17, -25.39) * mm, "end": v(11.4, -25.42) * mm});
            skLineSegment(sketch, "E1092", {"start": v(11.4, -25.42) * mm, "end": v(11.53, -19.33) * mm});
            skLineSegment(sketch, "E1093", {"start": v(11.53, -19.33) * mm, "end": v(9.65, -16.96) * mm});
            skLineSegment(sketch, "E1094", {"start": v(9.65, -16.96) * mm, "end": v(5.7, -14.4) * mm});
            skLineSegment(sketch, "E1095", {"start": v(5.7, -14.4) * mm, "end": v(1.78, -13.36) * mm});
            skLineSegment(sketch, "E1096", {"start": v(1.78, -13.36) * mm, "end": v(0.02, -15.05) * mm});
            skLineSegment(sketch, "E1097", {"start": v(0.02, -15.05) * mm, "end": v(-3.17, -19.03) * mm});
            skLineSegment(sketch, "E1098", {"start": v(-3.17, -19.03) * mm, "end": v(-6.3, -25.31) * mm});
            skLineSegment(sketch, "E1099", {"start": v(-6.3, -25.31) * mm, "end": v(-5.92, -31.2) * mm});
            skLineSegment(sketch, "E1100", {"start": v(-5.92, -31.2) * mm, "end": v(-1.98, -36.04) * mm});
            skLineSegment(sketch, "E1101", {"start": v(-1.98, -36.04) * mm, "end": v(-0.19, -36.05) * mm});
            skLineSegment(sketch, "E1102", {"start": v(-0.19, -36.05) * mm, "end": v(-0.1, -39.15) * mm});
            skLineSegment(sketch, "E1103", {"start": v(-0.1, -39.15) * mm, "end": v(1.83, -39.49) * mm});
            skLineSegment(sketch, "E1104", {"start": v(1.83, -39.49) * mm, "end": v(1.85, -39.5) * mm});
            skLineSegment(sketch, "E1105", {"start": v(1.85, -39.5) * mm, "end": v(1.85, -29.78) * mm});
            skLineSegment(sketch, "E1106", {"start": v(1.85, -29.78) * mm, "end": v(3.61, -28.6) * mm});
            skLineSegment(sketch, "E1107", {"start": v(3.61, -28.6) * mm, "end": v(3.77, -18.46) * mm});
            skLineSegment(sketch, "E1108", {"start": v(3.77, -18.46) * mm, "end": v(3.77, -18.45) * mm});
            skLineSegment(sketch, "E1109", {"start": v(3.77, -18.45) * mm, "end": v(4.56, -18.5) * mm});
            skLineSegment(sketch, "E1110", {"start": v(4.56, -18.5) * mm, "end": v(4.46, -25.97) * mm});
            skLineSegment(sketch, "E1111", {"start": v(4.46, -25.97) * mm, "end": v(4.81, -27.9) * mm});
            skLineSegment(sketch, "E1112", {"start": v(4.81, -27.9) * mm, "end": v(4.88, -27.78) * mm});
            skLineSegment(sketch, "E1113", {"start": v(8.7, -27.61) * mm, "end": v(12.55, -27.53) * mm});
            skLineSegment(sketch, "E1114", {"start": v(12.55, -27.53) * mm, "end": v(12.47, -34.3) * mm});
            skLineSegment(sketch, "E1115", {"start": v(12.47, -34.3) * mm, "end": v(13.68, -35.1) * mm});
            skLineSegment(sketch, "E1116", {"start": v(13.68, -35.1) * mm, "end": v(13.69, -41.53) * mm});
            skLineSegment(sketch, "E1117", {"start": v(13.69, -41.53) * mm, "end": v(7.25, -41.53) * mm});
            skLineSegment(sketch, "E1118", {"start": v(7.25, -41.53) * mm, "end": v(5.48, -39.04) * mm});
            skLineSegment(sketch, "E1119", {"start": v(5.48, -39.04) * mm, "end": v(3.79, -38.95) * mm});
            skLineSegment(sketch, "E1120", {"start": v(3.79, -38.95) * mm, "end": v(3.79, -30.34) * mm});
            skLineSegment(sketch, "E1121", {"start": v(3.79, -30.34) * mm, "end": v(6.04, -29.78) * mm});
            skLineSegment(sketch, "E1122", {"start": v(6.04, -29.78) * mm, "end": v(7.41, -29.06) * mm});
            skLineSegment(sketch, "E1123", {"start": v(7.41, -29.06) * mm, "end": v(8.7, -27.61) * mm});
            skLineSegment(sketch, "E1124", {"start": v(7.45, 10.52) * mm, "end": v(8.87, 11.85) * mm});
            skLineSegment(sketch, "E1125", {"start": v(8.87, 11.85) * mm, "end": v(12.1, 13.7) * mm});
            skLineSegment(sketch, "E1126", {"start": v(12.1, 13.7) * mm, "end": v(17.56, 13.29) * mm});
            skLineSegment(sketch, "E1127", {"start": v(17.56, 13.29) * mm, "end": v(19.23, 11.74) * mm});
            skLineSegment(sketch, "E1128", {"start": v(19.23, 11.74) * mm, "end": v(19.23, 6.7) * mm});
            skLineSegment(sketch, "E1129", {"start": v(19.23, 6.7) * mm, "end": v(18.04, 6.53) * mm});
            skLineSegment(sketch, "E1130", {"start": v(18.04, 6.53) * mm, "end": v(17.28, 5.85) * mm});
            skLineSegment(sketch, "E1131", {"start": v(17.28, 5.85) * mm, "end": v(17.7, 5.37) * mm});
            skLineSegment(sketch, "E1132", {"start": v(17.7, 5.37) * mm, "end": v(18, 4.57) * mm});
            skLineSegment(sketch, "E1133", {"start": v(18, 4.57) * mm, "end": v(15.98, 1.54) * mm});
            skLineSegment(sketch, "E1134", {"start": v(15.98, 1.54) * mm, "end": v(14.28, 0.73) * mm});
            skLineSegment(sketch, "E1135", {"start": v(14.28, 0.73) * mm, "end": v(12.9, 1.4) * mm});
            skLineSegment(sketch, "E1136", {"start": v(12.9, 1.4) * mm, "end": v(13.01, 2.47) * mm});
            skLineSegment(sketch, "E1137", {"start": v(13.01, 2.47) * mm, "end": v(14.64, 2.97) * mm});
            skLineSegment(sketch, "E1138", {"start": v(14.64, 2.97) * mm, "end": v(15.4, 3.88) * mm});
            skLineSegment(sketch, "E1139", {"start": v(15.4, 3.88) * mm, "end": v(11.3, 4.06) * mm});
            skLineSegment(sketch, "E1140", {"start": v(11.3, 4.06) * mm, "end": v(10.66, 4.96) * mm});
            skLineSegment(sketch, "E1141", {"start": v(10.66, 4.96) * mm, "end": v(8.59, 5.64) * mm});
            skLineSegment(sketch, "E1142", {"start": v(8.59, 5.64) * mm, "end": v(7.77, 7.18) * mm});
            skLineSegment(sketch, "E1143", {"start": v(7.77, 7.18) * mm, "end": v(7.41, 9.12) * mm});
            skLineSegment(sketch, "E1144", {"start": v(7.41, 9.12) * mm, "end": v(7.45, 10.52) * mm});
            skLineSegment(sketch, "E1145", {"start": v(26.37, 6.04) * mm, "end": v(26.36, 11.65) * mm});
            skLineSegment(sketch, "E1146", {"start": v(27.06, 4.36) * mm, "end": v(27.52, 5.62) * mm});
            skLineSegment(sketch, "E1147", {"start": v(27.52, 5.62) * mm, "end": v(26.37, 6.04) * mm});
            skLineSegment(sketch, "E1148", {"start": v(12.92, -25.4) * mm, "end": v(12.96, -26.1) * mm});
            skLineSegment(sketch, "E1149", {"start": v(12.96, -26.1) * mm, "end": v(12.96, -27.1) * mm});
            skLineSegment(sketch, "E1150", {"start": v(12.96, -27.1) * mm, "end": v(14.03, -27.2) * mm});
            skLineSegment(sketch, "E1151", {"start": v(16.56, -27.42) * mm, "end": v(15.37, -27.36) * mm});
            skLineSegment(sketch, "E1152", {"start": v(15.37, -27.36) * mm, "end": v(14.84, -26.97) * mm});
            skLineSegment(sketch, "E1153", {"start": v(14.66, -25.4) * mm, "end": v(12.92, -25.4) * mm});
            skLineSegment(sketch, "E1154", {"start": v(16.72, -30.66) * mm, "end": v(16.1, -30.59) * mm});
            skLineSegment(sketch, "E1155", {"start": v(16.1, -30.59) * mm, "end": v(15.57, -31.4) * mm});
            skLineSegment(sketch, "E1156", {"start": v(14.33, -31.97) * mm, "end": v(14.33, -33.93) * mm});
            skLineSegment(sketch, "E1157", {"start": v(14.33, -33.93) * mm, "end": v(15.43, -33.93) * mm});
            skLineSegment(sketch, "E1158", {"start": v(15.43, -33.93) * mm, "end": v(15.67, -33.38) * mm});
            skLineSegment(sketch, "E1159", {"start": v(15.67, -33.38) * mm, "end": v(16.79, -33.4) * mm});
            skLineSegment(sketch, "E1160", {"start": v(16.79, -33.4) * mm, "end": v(16.72, -30.66) * mm});
            skLineSegment(sketch, "E1161.left", {"start": v(28.71, -24) * mm, "end": v(28.71, -21.41) * mm});
            skLineSegment(sketch, "E1161.right", {"start": v(30.22, -24) * mm, "end": v(30.22, -21.41) * mm});
            skLineSegment(sketch, "E1162", {"start": v(29.95, -25.15) * mm, "end": v(27.72, -26.23) * mm});
            skLineSegment(sketch, "E1163", {"start": v(30.01, -29.12) * mm, "end": v(29.95, -25.15) * mm});
            skLineSegment(sketch, "E1164", {"start": v(30.13, -30.21) * mm, "end": v(27.54, -30.1) * mm});
            skLineSegment(sketch, "E1165", {"start": v(27.54, -30.1) * mm, "end": v(27.54, -33.1) * mm});
            skLineSegment(sketch, "E1166.bottom", {"start": v(29.23, -34.55) * mm, "end": v(27.36, -34.55) * mm});
            skLineSegment(sketch, "E1166.top", {"start": v(29.23, -39.2) * mm, "end": v(27.36, -39.2) * mm});
            skLineSegment(sketch, "E1167", {"start": v(30.36, -39.66) * mm, "end": v(31.14, -37.58) * mm});
            skLineSegment(sketch, "E1168", {"start": v(31.14, -37.58) * mm, "end": v(32.66, -35.93) * mm});
            skLineSegment(sketch, "E1169", {"start": v(32.66, -35.93) * mm, "end": v(33.41, -33.78) * mm});
            skLineSegment(sketch, "E1170", {"start": v(33.41, -33.78) * mm, "end": v(34.02, -31.19) * mm});
            skLineSegment(sketch, "E1171", {"start": v(34.02, -31.19) * mm, "end": v(34.57, -29.2) * mm});
            skLineSegment(sketch, "E1172", {"start": v(34.57, -29.2) * mm, "end": v(36.22, -27.54) * mm});
            skLineSegment(sketch, "E1173", {"start": v(36.22, -27.54) * mm, "end": v(38.7, -26.05) * mm});
            skLineSegment(sketch, "E1174", {"start": v(38.7, -26.05) * mm, "end": v(40.46, -25.21) * mm});
            skLineSegment(sketch, "E1175", {"start": v(40.46, -25.21) * mm, "end": v(40.62, -30.12) * mm});
            skLineSegment(sketch, "E1176", {"start": v(30.87, -40.23) * mm, "end": v(30.36, -39.66) * mm});
            skLineSegment(sketch, "E1177", {"start": v(32.7, -32.46) * mm, "end": v(31.22, -32.46) * mm});
            skLineSegment(sketch, "E1178", {"start": v(31.22, -32.46) * mm, "end": v(31.14, -21.4) * mm});
            skLineSegment(sketch, "E1179", {"start": v(31.14, -21.4) * mm, "end": v(31.62, -20.33) * mm});
            skLineSegment(sketch, "E1180", {"start": v(31.62, -20.33) * mm, "end": v(33.71, -19.65) * mm});
            skLineSegment(sketch, "E1181", {"start": v(33.71, -19.65) * mm, "end": v(34.86, -18.77) * mm});
            skLineSegment(sketch, "E1182", {"start": v(34.86, -18.77) * mm, "end": v(37.1, -18.3) * mm});
            skLineSegment(sketch, "E1183", {"start": v(37.1, -18.3) * mm, "end": v(38.59, -16.74) * mm});
            skLineSegment(sketch, "E1184", {"start": v(38.59, -16.74) * mm, "end": v(39.74, -14.84) * mm});
            skLineSegment(sketch, "E1185", {"start": v(39.74, -14.84) * mm, "end": v(40.89, -13.42) * mm});
            skLineSegment(sketch, "E1186", {"start": v(40.89, -13.42) * mm, "end": v(41.77, -12) * mm});
            skLineSegment(sketch, "E1187", {"start": v(41.77, -12) * mm, "end": v(42.78, -12.2) * mm});
            skLineSegment(sketch, "E1188", {"start": v(42.78, -12.2) * mm, "end": v(43.93, -13.62) * mm});
            skLineSegment(sketch, "E1189", {"start": v(43.93, -13.62) * mm, "end": v(44.75, -15.38) * mm});
            skLineSegment(sketch, "E1190", {"start": v(44.75, -15.38) * mm, "end": v(46.17, -16.87) * mm});
            skLineSegment(sketch, "E1191", {"start": v(46.17, -16.87) * mm, "end": v(46.91, -18.5) * mm});
            skLineSegment(sketch, "E1192", {"start": v(46.91, -18.5) * mm, "end": v(47.25, -19.99) * mm});
            skLineSegment(sketch, "E1193", {"start": v(47.25, -19.99) * mm, "end": v(47.66, -21.48) * mm});
            skLineSegment(sketch, "E1194", {"start": v(47.66, -21.48) * mm, "end": v(47.93, -22.83) * mm});
            skLineSegment(sketch, "E1195", {"start": v(47.93, -22.83) * mm, "end": v(48.8, -23.5) * mm});
            skLineSegment(sketch, "E1196", {"start": v(48.8, -23.5) * mm, "end": v(49.08, -25.4) * mm});
            skLineSegment(sketch, "E1197", {"start": v(49.08, -25.4) * mm, "end": v(49, -27.3) * mm});
            skLineSegment(sketch, "E1198", {"start": v(49, -27.3) * mm, "end": v(50.63, -27.7) * mm});
            skLineSegment(sketch, "E1199", {"start": v(50.63, -27.7) * mm, "end": v(50.7, -28.92) * mm});
            skLineSegment(sketch, "E1200", {"start": v(50.7, -28.92) * mm, "end": v(50.77, -31.63) * mm});
            skLineSegment(sketch, "E1201", {"start": v(50.77, -31.63) * mm, "end": v(50.77, -33.52) * mm});
            skLineSegment(sketch, "E1202", {"start": v(50.77, -33.52) * mm, "end": v(49.35, -33.46) * mm});
            skLineSegment(sketch, "E1203", {"start": v(49.35, -33.46) * mm, "end": v(48.2, -34.47) * mm});
            skLineSegment(sketch, "E1204", {"start": v(48.2, -34.47) * mm, "end": v(47.72, -35.7) * mm});
            skLineSegment(sketch, "E1205", {"start": v(47.72, -35.7) * mm, "end": v(48.06, -36.3) * mm});
            skLineSegment(sketch, "E1206", {"start": v(48.06, -36.3) * mm, "end": v(47.39, -37.72) * mm});
            skLineSegment(sketch, "E1207", {"start": v(47.39, -37.72) * mm, "end": v(45.83, -38.87) * mm});
            skLineSegment(sketch, "E1208", {"start": v(45.83, -38.87) * mm, "end": v(44.48, -39) * mm});
            skLineSegment(sketch, "E1209", {"start": v(44.48, -39) * mm, "end": v(43.33, -38.26) * mm});
            skLineSegment(sketch, "E1210", {"start": v(43.33, -38.26) * mm, "end": v(43.33, -28.8) * mm});
            skLineSegment(sketch, "E1211", {"start": v(43.33, -28.8) * mm, "end": v(42.47, -28.26) * mm});
            skLineSegment(sketch, "E1212", {"start": v(42.47, -28.26) * mm, "end": v(41.6, -23.56) * mm});
            skLineSegment(sketch, "E1213", {"start": v(41.6, -23.56) * mm, "end": v(41.74, -19.13) * mm});
            skLineSegment(sketch, "E1214", {"start": v(41.74, -19.13) * mm, "end": v(43.2, -17.46) * mm});
            skLineSegment(sketch, "E1215", {"start": v(43.2, -17.46) * mm, "end": v(42.51, -17.05) * mm});
            skLineSegment(sketch, "E1216", {"start": v(42.51, -17.05) * mm, "end": v(41.02, -18.77) * mm});
            skLineSegment(sketch, "E1217", {"start": v(41.02, -18.77) * mm, "end": v(40.66, -23.2) * mm});
            skLineSegment(sketch, "E1218", {"start": v(40.66, -23.2) * mm, "end": v(38.94, -24.33) * mm});
            skLineSegment(sketch, "E1219", {"start": v(38.94, -24.33) * mm, "end": v(36.5, -26.04) * mm});
            skLineSegment(sketch, "E1220", {"start": v(36.5, -26.04) * mm, "end": v(34.83, -27.25) * mm});
            skLineSegment(sketch, "E1221", {"start": v(34.83, -27.25) * mm, "end": v(33.49, -28.66) * mm});
            skLineSegment(sketch, "E1222", {"start": v(33.49, -28.66) * mm, "end": v(32.7, -32.46) * mm});
            skLineSegment(sketch, "E1223.bottom", {"start": v(12.84, 10.33) * mm, "end": v(16.02, 10.33) * mm});
            skLineSegment(sketch, "E1223.top", {"start": v(12.84, 6.3) * mm, "end": v(16.02, 6.3) * mm});
            skLineSegment(sketch, "E1223.left", {"start": v(12.84, 10.33) * mm, "end": v(12.84, 6.3) * mm});
            skLineSegment(sketch, "E1223.right", {"start": v(16.02, 10.33) * mm, "end": v(16.02, 6.3) * mm});
            skLineSegment(sketch, "E1224.left", {"start": v(12.84, 6.3) * mm, "end": v(12.84, 10.33) * mm});
            skLineSegment(sketch, "E1224.right", {"start": v(16.02, 6.3) * mm, "end": v(16.02, 10.33) * mm});
            skLineSegment(sketch, "E1225.bottom", {"start": v(29.46, 10.33) * mm, "end": v(33.1, 10.33) * mm});
            skLineSegment(sketch, "E1225.top", {"start": v(29.46, 6.1) * mm, "end": v(33.1, 6.1) * mm});
            skLineSegment(sketch, "E1225.left", {"start": v(29.46, 10.33) * mm, "end": v(29.46, 6.1) * mm});
            skLineSegment(sketch, "E1225.right", {"start": v(33.1, 10.33) * mm, "end": v(33.1, 6.1) * mm});
            skLineSegment(sketch, "E1226", {"start": v(20.42, 3.4) * mm, "end": v(21.77, 3.87) * mm});
            skLineSegment(sketch, "E1227", {"start": v(21.77, 3.87) * mm, "end": v(21.77, 6.56) * mm});
            skLineSegment(sketch, "E1228", {"start": v(21.77, 6.56) * mm, "end": v(24.18, 6.5) * mm});
            skLineSegment(sketch, "E1229", {"start": v(24.18, 6.5) * mm, "end": v(24.18, 4.2) * mm});
            skLineSegment(sketch, "E1230", {"start": v(24.18, 4.2) * mm, "end": v(25.47, 3.2) * mm});
            skLineSegment(sketch, "E1231", {"start": v(25.47, 3.2) * mm, "end": v(25.47, -0.9) * mm});
            skLineSegment(sketch, "E1232", {"start": v(25.47, -0.9) * mm, "end": v(20.42, -0.9) * mm});
            skLineSegment(sketch, "E1233", {"start": v(20.42, -0.9) * mm, "end": v(20.42, 3.4) * mm});
            skLineSegment(sketch, "E1234", {"start": v(10.47, 0.01) * mm, "end": v(11.03, 1.29) * mm});
            skLineSegment(sketch, "E1235", {"start": v(11.03, 1.29) * mm, "end": v(12.22, 1.12) * mm});
            skLineSegment(sketch, "E1236", {"start": v(17.7, -4.2) * mm, "end": v(29.97, -4.2) * mm});
            skLineSegment(sketch, "E1237", {"start": v(30.34, -3.05) * mm, "end": v(31.78, -2.4) * mm});
            skLineSegment(sketch, "E1238", {"start": v(31.78, -2.4) * mm, "end": v(33.2, -1.7) * mm});
            skLineSegment(sketch, "E1239", {"start": v(36.6, -2.38) * mm, "end": v(38.18, -3.23) * mm});
            skLineSegment(sketch, "E1240", {"start": v(38.18, -3.23) * mm, "end": v(37.08, -4.08) * mm});
            skLineSegment(sketch, "E1241", {"start": v(37.08, -4.08) * mm, "end": v(35.24, -3.95) * mm});
            skLineSegment(sketch, "E1242", {"start": v(35.24, -3.95) * mm, "end": v(35.24, -3.95) * mm});
            skLineSegment(sketch, "E1243", {"start": v(35.24, -3.95) * mm, "end": v(33.88, -6.56) * mm});
            skLineSegment(sketch, "E1244", {"start": v(33.88, -6.56) * mm, "end": v(31.23, -9.37) * mm});
            skLineSegment(sketch, "E1245", {"start": v(31.23, -9.37) * mm, "end": v(28.8, -10.73) * mm});
            skLineSegment(sketch, "E1246", {"start": v(12.43, -6.43) * mm, "end": v(11.04, -5.42) * mm});
            skLineSegment(sketch, "E1247", {"start": v(11.04, -5.42) * mm, "end": v(10.15, -3.7) * mm});
            skLineSegment(sketch, "E1248", {"start": v(10.15, -3.7) * mm, "end": v(10.15, -3.7) * mm});
            skLineSegment(sketch, "E1249", {"start": v(10.15, -3.7) * mm, "end": v(8.97, -3.36) * mm});
            skLineSegment(sketch, "E1250.bottom", {"start": v(11.72, -2.3) * mm, "end": v(13.94, -2.3) * mm});
            skLineSegment(sketch, "E1250.top", {"start": v(11.72, -5.74) * mm, "end": v(13.94, -5.74) * mm});
            skLineSegment(sketch, "E1250.left", {"start": v(11.72, -2.3) * mm, "end": v(11.72, -5.74) * mm});
            skLineSegment(sketch, "E1250.right", {"start": v(13.94, -2.3) * mm, "end": v(13.94, -5.74) * mm});
            skLineSegment(sketch, "E1251.bottom", {"start": v(11.72, -5.74) * mm, "end": v(13.93, -5.74) * mm});
            skLineSegment(sketch, "E1251.top", {"start": v(11.72, -2.3) * mm, "end": v(13.93, -2.3) * mm});
            skLineSegment(sketch, "E1251.left", {"start": v(11.72, -5.74) * mm, "end": v(11.72, -2.3) * mm});
            skLineSegment(sketch, "E1251.right", {"start": v(13.93, -5.74) * mm, "end": v(13.93, -2.3) * mm});
            skLineSegment(sketch, "E1252.bottom", {"start": v(18.38, -5.16) * mm, "end": v(22.17, -5.16) * mm});
            skLineSegment(sketch, "E1252.top", {"start": v(18.38, -9.9) * mm, "end": v(22.17, -9.9) * mm});
            skLineSegment(sketch, "E1252.left", {"start": v(18.38, -5.16) * mm, "end": v(18.38, -9.9) * mm});
            skLineSegment(sketch, "E1252.right", {"start": v(22.17, -5.16) * mm, "end": v(22.17, -9.9) * mm});
            skLineSegment(sketch, "E1253.bottom", {"start": v(22.73, -5.18) * mm, "end": v(27.11, -5.18) * mm});
            skLineSegment(sketch, "E1253.top", {"start": v(22.73, -9.88) * mm, "end": v(27.11, -9.88) * mm});
            skLineSegment(sketch, "E1253.left", {"start": v(22.73, -5.18) * mm, "end": v(22.73, -9.88) * mm});
            skLineSegment(sketch, "E1253.right", {"start": v(27.11, -5.18) * mm, "end": v(27.11, -9.88) * mm});
            skLineSegment(sketch, "E1254.bottom", {"start": v(30.66, -3.36) * mm, "end": v(33.13, -3.36) * mm});
            skLineSegment(sketch, "E1254.top", {"start": v(30.66, -7) * mm, "end": v(33.13, -7) * mm});
            skLineSegment(sketch, "E1254.left", {"start": v(30.66, -3.36) * mm, "end": v(30.66, -7) * mm});
            skLineSegment(sketch, "E1254.right", {"start": v(33.13, -3.36) * mm, "end": v(33.13, -7) * mm});
            skLineSegment(sketch, "E1255", {"start": v(14.33, -3.7) * mm, "end": v(14.33, -7.12) * mm});
            skLineSegment(sketch, "E1256", {"start": v(17.9, -8.71) * mm, "end": v(17.9, -5.39) * mm});
            skLineSegment(sketch, "E1257", {"start": v(14.33, -3.7) * mm, "end": v(16, -3.7) * mm});
            skLineSegment(sketch, "E1258", {"start": v(16, -3.7) * mm, "end": v(16, -4.8) * mm});
            skLineSegment(sketch, "E1259", {"start": v(16, -4.8) * mm, "end": v(16.54, -5.3) * mm});
            skLineSegment(sketch, "E1260", {"start": v(16.54, -5.3) * mm, "end": v(17.9, -5.39) * mm});
            skLineSegment(sketch, "E1261", {"start": v(15.75, -8.27) * mm, "end": v(14.98, -7.47) * mm});
            skLineSegment(sketch, "E1262", {"start": v(14.98, -7.47) * mm, "end": v(14.33, -7.12) * mm});
            skLineSegment(sketch, "E1263", {"start": v(15.75, -8.27) * mm, "end": v(15.99, -8.71) * mm});
            skLineSegment(sketch, "E1264", {"start": v(15.99, -8.71) * mm, "end": v(17.9, -8.71) * mm});
            skLineSegment(sketch, "E1265", {"start": v(27.51, -5.15) * mm, "end": v(27.51, -9.45) * mm});
            skLineSegment(sketch, "E1266", {"start": v(27.51, -9.45) * mm, "end": v(29.44, -9.45) * mm});
            skLineSegment(sketch, "E1267", {"start": v(29.44, -9.45) * mm, "end": v(30.34, -8.24) * mm});
            skLineSegment(sketch, "E1268", {"start": v(30.34, -8.24) * mm, "end": v(30.34, -5.15) * mm});
            skLineSegment(sketch, "E1269", {"start": v(30.34, -5.15) * mm, "end": v(27.51, -5.15) * mm});
            skLineSegment(sketch, "E1270", {"start": v(14.33, -7.12) * mm, "end": v(14.98, -7.47) * mm});
            skLineSegment(sketch, "E1271", {"start": v(14.98, -7.47) * mm, "end": v(15.75, -8.26) * mm});
            skLineSegment(sketch, "E1272", {"start": v(15.75, -8.26) * mm, "end": v(15.99, -8.71) * mm});
            skLineSegment(sketch, "E1273", {"start": v(15.99, -8.71) * mm, "end": v(17.89, -8.7) * mm});
            skLineSegment(sketch, "E1274", {"start": v(17.89, -8.7) * mm, "end": v(17.89, -5.4) * mm});
            skLineSegment(sketch, "E1275", {"start": v(17.89, -5.4) * mm, "end": v(16.54, -5.3) * mm});
            skLineSegment(sketch, "E1276", {"start": v(16.54, -5.3) * mm, "end": v(16, -4.8) * mm});
            skLineSegment(sketch, "E1277", {"start": v(16, -4.8) * mm, "end": v(16, -3.7) * mm});
            skLineSegment(sketch, "E1278", {"start": v(16, -3.7) * mm, "end": v(14.33, -3.7) * mm});
            skLineSegment(sketch, "E1279.bottom", {"start": v(18.39, -9.9) * mm, "end": v(22.17, -9.9) * mm});
            skLineSegment(sketch, "E1279.top", {"start": v(18.39, -5.16) * mm, "end": v(22.17, -5.16) * mm});
            skLineSegment(sketch, "E1279.left", {"start": v(18.39, -9.9) * mm, "end": v(18.39, -5.16) * mm});
            skLineSegment(sketch, "E1279.right", {"start": v(22.17, -9.9) * mm, "end": v(22.17, -5.16) * mm});
            skLineSegment(sketch, "E1280.bottom", {"start": v(22.74, -9.88) * mm, "end": v(27.1, -9.88) * mm});
            skLineSegment(sketch, "E1280.top", {"start": v(22.74, -5.19) * mm, "end": v(27.1, -5.19) * mm});
            skLineSegment(sketch, "E1280.left", {"start": v(22.74, -9.88) * mm, "end": v(22.74, -5.19) * mm});
            skLineSegment(sketch, "E1280.right", {"start": v(27.1, -9.88) * mm, "end": v(27.1, -5.19) * mm});
            skLineSegment(sketch, "E1281.bottom", {"start": v(30.66, -7) * mm, "end": v(33.12, -7) * mm});
            skLineSegment(sketch, "E1281.top", {"start": v(30.66, -3.36) * mm, "end": v(33.12, -3.36) * mm});
            skLineSegment(sketch, "E1281.left", {"start": v(30.66, -7) * mm, "end": v(30.66, -3.36) * mm});
            skLineSegment(sketch, "E1281.right", {"start": v(33.12, -7) * mm, "end": v(33.12, -3.36) * mm});
            skLineSegment(sketch, "E1282", {"start": v(27.52, -5.15) * mm, "end": v(27.52, -9.44) * mm});
            skLineSegment(sketch, "E1283", {"start": v(27.52, -9.44) * mm, "end": v(29.44, -9.44) * mm});
            skLineSegment(sketch, "E1284", {"start": v(29.44, -9.44) * mm, "end": v(30.34, -8.24) * mm});
            skLineSegment(sketch, "E1285", {"start": v(30.34, -5.15) * mm, "end": v(27.52, -5.15) * mm});
            skLineSegment(sketch, "E1286", {"start": v(10.54, -43.95) * mm, "end": v(9.97, -45.8) * mm});
            skLineSegment(sketch, "E1287", {"start": v(9.97, -45.8) * mm, "end": v(9.72, -47.8) * mm});
            skLineSegment(sketch, "E1288", {"start": v(9.72, -47.8) * mm, "end": v(8.65, -49.15) * mm});
            skLineSegment(sketch, "E1289", {"start": v(8.65, -49.15) * mm, "end": v(8.37, -55.14) * mm});
            skLineSegment(sketch, "E1290", {"start": v(8.37, -55.14) * mm, "end": v(8.35, -55.2) * mm});
            skLineSegment(sketch, "E1291", {"start": v(8.35, -55.2) * mm, "end": v(7.22, -56.05) * mm});
            skLineSegment(sketch, "E1292", {"start": v(7.22, -56.05) * mm, "end": v(7.4, -62.12) * mm});
            skLineSegment(sketch, "E1293", {"start": v(7.4, -62.12) * mm, "end": v(9.04, -61.94) * mm});
            skLineSegment(sketch, "E1294", {"start": v(9.04, -61.94) * mm, "end": v(9.15, -56.68) * mm});
            skLineSegment(sketch, "E1295", {"start": v(9.15, -56.68) * mm, "end": v(10.48, -54.78) * mm});
            skLineSegment(sketch, "E1296", {"start": v(10.48, -54.78) * mm, "end": v(10.38, -49.57) * mm});
            skLineSegment(sketch, "E1297", {"start": v(10.38, -49.57) * mm, "end": v(12.5, -47) * mm});
            skLineSegment(sketch, "E1298", {"start": v(12.5, -47) * mm, "end": v(14.06, -48.38) * mm});
            skLineSegment(sketch, "E1299", {"start": v(14.06, -48.38) * mm, "end": v(12.78, -49.84) * mm});
            skLineSegment(sketch, "E1300", {"start": v(12.78, -49.84) * mm, "end": v(13.15, -55.2) * mm});
            skLineSegment(sketch, "E1301", {"start": v(13.15, -55.2) * mm, "end": v(11.9, -56.72) * mm});
            skLineSegment(sketch, "E1302", {"start": v(11.9, -56.72) * mm, "end": v(12, -62.25) * mm});
            skLineSegment(sketch, "E1303", {"start": v(12, -62.25) * mm, "end": v(12.76, -63.63) * mm});
            skLineSegment(sketch, "E1304", {"start": v(12.76, -63.63) * mm, "end": v(22.54, -63.75) * mm});
            skLineSegment(sketch, "E1305", {"start": v(22.54, -63.75) * mm, "end": v(22.93, -56.53) * mm});
            skLineSegment(sketch, "E1306", {"start": v(22.93, -56.53) * mm, "end": v(24.13, -56.37) * mm});
            skLineSegment(sketch, "E1307", {"start": v(24.13, -56.37) * mm, "end": v(24.34, -50.42) * mm});
            skLineSegment(sketch, "E1308", {"start": v(24.34, -50.42) * mm, "end": v(25.94, -49.04) * mm});
            skLineSegment(sketch, "E1309", {"start": v(25.94, -49.04) * mm, "end": v(27.95, -50.86) * mm});
            skLineSegment(sketch, "E1310", {"start": v(27.95, -50.86) * mm, "end": v(27.95, -54.02) * mm});
            skLineSegment(sketch, "E1311", {"start": v(27.95, -54.02) * mm, "end": v(29.57, -55.65) * mm});
            skLineSegment(sketch, "E1312", {"start": v(35.89, -63.21) * mm, "end": v(36.05, -59.4) * mm});
            skLineSegment(sketch, "E1313", {"start": v(36.05, -59.4) * mm, "end": v(34.55, -57.99) * mm});
            skLineSegment(sketch, "E1314", {"start": v(34.55, -57.99) * mm, "end": v(34.52, -57.94) * mm});
            skLineSegment(sketch, "E1315", {"start": v(34.52, -57.94) * mm, "end": v(34.71, -44.62) * mm});
            skLineSegment(sketch, "E1316", {"start": v(34.71, -44.62) * mm, "end": v(37.63, -44.73) * mm});
            skLineSegment(sketch, "E1317", {"start": v(37.63, -44.73) * mm, "end": v(37.63, -51.73) * mm});
            skLineSegment(sketch, "E1318", {"start": v(37.63, -51.73) * mm, "end": v(39.34, -53.16) * mm});
            skLineSegment(sketch, "E1319", {"start": v(39.34, -53.16) * mm, "end": v(38.6, -62.06) * mm});
            skLineSegment(sketch, "E1320", {"start": v(38.6, -62.06) * mm, "end": v(40.2, -63.48) * mm});
            skLineSegment(sketch, "E1321", {"start": v(40.2, -63.48) * mm, "end": v(42, -62.42) * mm});
            skLineSegment(sketch, "E1322", {"start": v(42, -62.42) * mm, "end": v(45.55, -62.35) * mm});
            skLineSegment(sketch, "E1323", {"start": v(45.55, -62.35) * mm, "end": v(45.5, -55.08) * mm});
            skLineSegment(sketch, "E1324", {"start": v(45.5, -55.08) * mm, "end": v(44.57, -54.02) * mm});
            skLineSegment(sketch, "E1325", {"start": v(44.57, -54.02) * mm, "end": v(44.38, -49.24) * mm});
            skLineSegment(sketch, "E1326", {"start": v(44.38, -49.24) * mm, "end": v(43.3, -46.27) * mm});
            skLineSegment(sketch, "E1327", {"start": v(43.3, -46.27) * mm, "end": v(43.69, -44.64) * mm});
            skLineSegment(sketch, "E1328", {"start": v(43.69, -44.64) * mm, "end": v(43.69, -41.7) * mm});
            skLineSegment(sketch, "E1329", {"start": v(43.69, -41.7) * mm, "end": v(42.95, -40.43) * mm});
            skLineSegment(sketch, "E1330", {"start": v(42.95, -40.43) * mm, "end": v(40.88, -41.15) * mm});
            skLineSegment(sketch, "E1331", {"start": v(40.88, -41.15) * mm, "end": v(38.59, -41.99) * mm});
            skLineSegment(sketch, "E1332", {"start": v(38.59, -41.99) * mm, "end": v(32.68, -41.66) * mm});
            skLineSegment(sketch, "E1333", {"start": v(32.68, -41.66) * mm, "end": v(28.8, -42) * mm});
            skLineSegment(sketch, "E1334", {"start": v(28.8, -42) * mm, "end": v(27.66, -42.02) * mm});
            skLineSegment(sketch, "E1335", {"start": v(27.66, -42.02) * mm, "end": v(26.78, -40.76) * mm});
            skLineSegment(sketch, "E1336", {"start": v(26.78, -40.76) * mm, "end": v(21.8, -40.92) * mm});
            skLineSegment(sketch, "E1337", {"start": v(21.8, -40.92) * mm, "end": v(20.41, -41.6) * mm});
            skLineSegment(sketch, "E1338", {"start": v(20.41, -41.6) * mm, "end": v(19.7, -42.64) * mm});
            skLineSegment(sketch, "E1339", {"start": v(19.7, -42.64) * mm, "end": v(19.62, -42.68) * mm});
            skLineSegment(sketch, "E1340", {"start": v(19.62, -42.68) * mm, "end": v(15.2, -42.77) * mm});
            skLineSegment(sketch, "E1341", {"start": v(15.2, -42.77) * mm, "end": v(13.61, -44.08) * mm});
            skLineSegment(sketch, "E1342", {"start": v(13.61, -44.08) * mm, "end": v(10.54, -43.95) * mm});
            skSolve(sketch);
        }
        {
            var Q0;
            Q0=makeQuery(id+"F2.imprint","IMPRINT",FACE,{"disambiguationData":[TD([[makeQuery(id+"F2.imprint","IMPRINT",EDGE,{"derivedFrom":sQuery(id+"F2.wireOp",EDGE,"E722")}),-1.0]])]});
            var Q1;
            Q1=makeQuery(id+"F2.imprint","IMPRINT",FACE,{"disambiguationData":[TD([[makeQuery(id+"F2.imprint","IMPRINT",EDGE,{"derivedFrom":sQuery(id+"F2.wireOp",EDGE,"E737")}),1.0]])]});
            var Q2;
            Q2=makeQuery(id+"F2.imprint","IMPRINT",FACE,{"disambiguationData":[TD([[makeQuery(id+"F2.imprint","IMPRINT",EDGE,{"derivedFrom":sQuery(id+"F2.wireOp",EDGE,"E967")}),-1.0]])]});
            var Q3;
            Q3=makeQuery(id+"F2.imprint","IMPRINT",FACE,{"disambiguationData":[TD([[makeQuery(id+"F2.imprint","IMPRINT",EDGE,{"derivedFrom":sQuery(id+"F2.wireOp",EDGE,"E1035")}),-1.0]])]});
            var Q4;
            Q4=makeQuery(id+"F2.imprint","IMPRINT",FACE,{"disambiguationData":[TD([[makeQuery(id+"F2.imprint","IMPRINT",EDGE,{"derivedFrom":sQuery(id+"F2.wireOp",EDGE,"E1046")}),1.0]])]});
            var Q5;
            Q5=makeQuery(id+"F2.imprint","IMPRINT",FACE,{"disambiguationData":[TD([[makeQuery(id+"F2.imprint","IMPRINT",EDGE,{"derivedFrom":sQuery(id+"F2.wireOp",EDGE,"E1054")}),1.0]])]});
            var Q6;
            Q6=makeQuery(id+"F2.imprint","IMPRINT",FACE,{"disambiguationData":[TD([[makeQuery(id+"F2.imprint","IMPRINT",EDGE,{"derivedFrom":sQuery(id+"F2.wireOp",EDGE,"E1058")}),1.0]])]});
            var Q7;
            Q7=makeQuery(id+"F2.imprint","IMPRINT",FACE,{"disambiguationData":[TD([[makeQuery(id+"F2.imprint","IMPRINT",EDGE,{"derivedFrom":sQuery(id+"F2.wireOp",EDGE,"E1070")}),-1.0]])]});
            var Q8;
            Q8=makeQuery(id+"F2.imprint","IMPRINT",FACE,{"disambiguationData":[TD([[makeQuery(id+"F2.imprint","IMPRINT",EDGE,{"derivedFrom":sQuery(id+"F2.wireOp",EDGE,"c1c82c28-52c2-4fab-9710-17f7591158fe")}),-1.0]])]});
            var Q9;
            Q9=makeQuery(id+"F2.imprint","IMPRINT",FACE,{"disambiguationData":[TD([[makeQuery(id+"F2.imprint","IMPRINT",EDGE,{"derivedFrom":sQuery(id+"F2.wireOp",EDGE,"4ee1179b-3031-4ee2-a42b-07435d50cfc0")}),1.0]])]});
            var Q10;
            Q10=makeQuery(id+"F2.imprint","IMPRINT",FACE,{"disambiguationData":[TD([[makeQuery(id+"F2.imprint","IMPRINT",EDGE,{"derivedFrom":sQuery(id+"F2.wireOp",EDGE,"10aeca11-c88a-4ddb-b15b-c2b15c4dfa68.bottom")}),-1.0]])]});
            var Q11;
            Q11=makeQuery(id+"F2.imprint","IMPRINT",FACE,{"disambiguationData":[TD([[makeQuery(id+"F2.imprint","IMPRINT",EDGE,{"derivedFrom":sQuery(id+"F2.wireOp",EDGE,"37253bd0-4693-48ca-a450-64db61d699f5")}),1.0]])]});
            var Q12;
            Q12=makeQuery(id+"F2.imprint","IMPRINT",FACE,{"disambiguationData":[TD([[makeQuery(id+"F2.imprint","IMPRINT",EDGE,{"derivedFrom":sQuery(id+"F2.wireOp",EDGE,"4021a4ca-61fd-4e59-a8d2-e24243b1d5b2.bottom")}),-1.0]])]});
            var Q13;
            Q13=makeQuery(id+"F2.imprint","IMPRINT",FACE,{"disambiguationData":[TD([[makeQuery(id+"F2.imprint","IMPRINT",EDGE,{"derivedFrom":sQuery(id+"F2.wireOp",EDGE,"E1089")}),1.0]])]});
            var Q14;
            Q14=makeQuery(id+"F2.imprint","IMPRINT",FACE,{"disambiguationData":[TD([[makeQuery(id+"F2.imprint","IMPRINT",EDGE,{"derivedFrom":sQuery(id+"F2.wireOp",EDGE,"E1113")}),-1.0]])]});
            var Q15;
            Q15=makeQuery(id+"F2.imprint","IMPRINT",FACE,{"disambiguationData":[TD([[makeQuery(id+"F2.imprint","IMPRINT",EDGE,{"derivedFrom":sQuery(id+"F2.wireOp",EDGE,"E1124")}),-1.0]])]});
            var Q16;
            Q16=makeQuery(id+"F2.imprint","IMPRINT",FACE,{"disambiguationData":[TD([[makeQuery(id+"F2.imprint","IMPRINT",EDGE,{"derivedFrom":sQuery(id+"F2.wireOp",EDGE,"E1145")}),-1.0]])]});
            var Q17;
            Q17=makeQuery(id+"F2.imprint","IMPRINT",FACE,{"disambiguationData":[TD([[makeQuery(id+"F2.imprint","IMPRINT",EDGE,{"derivedFrom":sQuery(id+"F2.wireOp",EDGE,"E863")}),1.0]])]});
            var Q18;
            Q18=makeQuery(id+"F2.imprint","IMPRINT",FACE,{"disambiguationData":[TD([[makeQuery(id+"F2.imprint","IMPRINT",EDGE,{"derivedFrom":sQuery(id+"F2.wireOp",EDGE,"E1148")}),1.0]])]});
            var Q19;
            Q19=makeQuery(id+"F2.imprint","IMPRINT",FACE,{"disambiguationData":[TD([[makeQuery(id+"F2.imprint","IMPRINT",EDGE,{"derivedFrom":sQuery(id+"F2.wireOp",EDGE,"E1154")}),1.0]])]});
            var Q20;
            Q20=makeQuery(id+"F2.imprint","IMPRINT",FACE,{"disambiguationData":[TD([[makeQuery(id+"F2.imprint","IMPRINT",EDGE,{"derivedFrom":sQuery(id+"F2.wireOp",EDGE,"E890")}),1.0]])]});
            var Q21;
            Q21=makeQuery(id+"F2.imprint","IMPRINT",FACE,{"disambiguationData":[TD([[makeQuery(id+"F2.imprint","IMPRINT",EDGE,{"derivedFrom":sQuery(id+"F2.wireOp",EDGE,"E1177")}),-1.0]])]});
            var Q22;
            Q22=makeQuery(id+"F2.imprint","IMPRINT",FACE,{"disambiguationData":[TD([[makeQuery(id+"F2.imprint","IMPRINT",EDGE,{"derivedFrom":sQuery(id+"F2.wireOp",EDGE,"E1167")}),-1.0]])]});
            var Q23;
            Q23=makeQuery(id+"F2.imprint","IMPRINT",FACE,{"disambiguationData":[TD([[makeQuery(id+"F2.imprint","IMPRINT",EDGE,{"derivedFrom":sQuery(id+"F2.wireOp",EDGE,"E1164")}),1.0]])]});
            var Q24;
            Q24=makeQuery(id+"F2.imprint","IMPRINT",FACE,{"disambiguationData":[TD([[makeQuery(id+"F2.imprint","IMPRINT",EDGE,{"derivedFrom":sQuery(id+"F2.wireOp",EDGE,"E1166.bottom")}),1.0]])]});
            var Q25;
            Q25=makeQuery(id+"F2.imprint","IMPRINT",FACE,{"disambiguationData":[TD([[makeQuery(id+"F2.imprint","IMPRINT",EDGE,{"derivedFrom":sQuery(id+"F2.wireOp",EDGE,"E1162")}),1.0]])]});
            var Q26;
            Q26=makeQuery(id+"F2.imprint","IMPRINT",FACE,{"disambiguationData":[TD([[makeQuery(id+"F2.imprint","IMPRINT",EDGE,{"derivedFrom":sQuery(id+"F2.wireOp",EDGE,"E952.top")}),1.0]])]});
            var Q27;
            Q27=makeQuery(id+"F2.imprint","IMPRINT",FACE,{"disambiguationData":[TD([[makeQuery(id+"F2.imprint","IMPRINT",EDGE,{"derivedFrom":sQuery(id+"F2.wireOp",EDGE,"E1124")}),-1.0]])]});
            var Q28;
            Q28=makeQuery(id+"F2.imprint","IMPRINT",FACE,{"disambiguationData":[TD([[makeQuery(id+"F2.imprint","IMPRINT",EDGE,{"derivedFrom":sQuery(id+"F2.wireOp",EDGE,"E1145")}),-1.0]])]});
            var Q29;
            Q29=makeQuery(id+"F2.imprint","IMPRINT",FACE,{"disambiguationData":[TD([[makeQuery(id+"F2.imprint","IMPRINT",EDGE,{"derivedFrom":sQuery(id+"F2.wireOp",EDGE,"E1223.top")}),1.0]])]});
            var Q30;
            Q30=makeQuery(id+"F2.imprint","IMPRINT",FACE,{"disambiguationData":[TD([[makeQuery(id+"F2.imprint","IMPRINT",EDGE,{"derivedFrom":sQuery(id+"F2.wireOp",EDGE,"E1225.bottom")}),-1.0]])]});
            var Q31;
            Q31=makeQuery(id+"F2.imprint","IMPRINT",FACE,{"disambiguationData":[TD([[makeQuery(id+"F2.imprint","IMPRINT",EDGE,{"derivedFrom":sQuery(id+"F2.wireOp",EDGE,"E1226")}),-1.0]])]});
            var Q32;
            Q32=makeQuery(id+"F2.imprint","IMPRINT",FACE,{"disambiguationData":[TD([[makeQuery(id+"F2.imprint","IMPRINT",EDGE,{"derivedFrom":sQuery(id+"F2.wireOp",EDGE,"E1251.bottom")}),1.0]])]});
            var Q33;
            Q33=makeQuery(id+"F2.imprint","IMPRINT",FACE,{"disambiguationData":[TD([[makeQuery(id+"F2.imprint","IMPRINT",EDGE,{"derivedFrom":sQuery(id+"F2.wireOp",EDGE,"E607")}),-1.0]])]});
            var Q34;
            Q34=makeQuery(id+"F2.imprint","IMPRINT",FACE,{"disambiguationData":[TD([[makeQuery(id+"F2.imprint","IMPRINT",EDGE,{"derivedFrom":sQuery(id+"F2.wireOp",EDGE,"6f6eea80-531d-413f-83e2-d218fd4cdfc1.bottom")}),-1.0]])]});
            var Q35;
            Q35=makeQuery(id+"F2.imprint","IMPRINT",FACE,{"disambiguationData":[TD([[makeQuery(id+"F2.imprint","IMPRINT",EDGE,{"derivedFrom":sQuery(id+"F2.wireOp",EDGE,"b7e1cb25-9bb9-44e2-b99a-fb5c20a56b0c.bottom")}),-1.0]])]});
            var Q36;
            Q36=makeQuery(id+"F2.imprint","IMPRINT",FACE,{"disambiguationData":[TD([[makeQuery(id+"F2.imprint","IMPRINT",EDGE,{"derivedFrom":sQuery(id+"F2.wireOp",EDGE,"ce22afcd-61db-4a55-a298-b4625a8987c8")}),1.0]])]});
            var Q37;
            Q37=makeQuery(id+"F2.imprint","IMPRINT",FACE,{"disambiguationData":[TD([[makeQuery(id+"F2.imprint","IMPRINT",EDGE,{"derivedFrom":sQuery(id+"F2.wireOp",EDGE,"780705e2-dc3a-4fd6-9091-f85142a16bed.bottom")}),1.0]])]});
            var Q38;
            Q38=makeQuery(id+"F2.imprint","IMPRINT",FACE,{"disambiguationData":[TD([[makeQuery(id+"F2.imprint","IMPRINT",EDGE,{"derivedFrom":sQuery(id+"F2.wireOp",EDGE,"c1c82c28-52c2-4fab-9710-17f7591158fe")}),1.0]])]});
            var Q39;
            Q39=makeQuery(id+"F2.imprint","IMPRINT",FACE,{"disambiguationData":[TD([[makeQuery(id+"F2.imprint","IMPRINT",EDGE,{"derivedFrom":sQuery(id+"F2.wireOp",EDGE,"e8153c08-a27a-4b41-8524-6b09fd277459")}),1.0]])]});
            var Q40;
            Q40=makeQuery(id+"F2.imprint","IMPRINT",FACE,{"disambiguationData":[TD([[makeQuery(id+"F2.imprint","IMPRINT",EDGE,{"derivedFrom":sQuery(id+"F2.wireOp",EDGE,"E745")}),-1.0]])]});
            var Q41;
            Q41=makeQuery(id+"F2.imprint","IMPRINT",FACE,{"disambiguationData":[TD([[makeQuery(id+"F2.imprint","IMPRINT",EDGE,{"derivedFrom":sQuery(id+"F2.wireOp",EDGE,"E1255")}),1.0]])]});
            var Q42;
            Q42=makeQuery(id+"F2.imprint","IMPRINT",FACE,{"disambiguationData":[TD([[makeQuery(id+"F2.imprint","IMPRINT",EDGE,{"derivedFrom":sQuery(id+"F2.wireOp",EDGE,"E1279.bottom")}),1.0]])]});
            var Q43;
            Q43=makeQuery(id+"F2.imprint","IMPRINT",FACE,{"disambiguationData":[TD([[makeQuery(id+"F2.imprint","IMPRINT",EDGE,{"derivedFrom":sQuery(id+"F2.wireOp",EDGE,"E1280.bottom")}),1.0]])]});
            var Q44;
            Q44=makeQuery(id+"F2.imprint","IMPRINT",FACE,{"disambiguationData":[TD([[makeQuery(id+"F2.imprint","IMPRINT",EDGE,{"derivedFrom":sQuery(id+"F2.wireOp",EDGE,"E1282")}),1.0]])]});
            var Q45;
            Q45=makeQuery(id+"F2.imprint","IMPRINT",FACE,{"disambiguationData":[TD([[makeQuery(id+"F2.imprint","IMPRINT",EDGE,{"derivedFrom":sQuery(id+"F2.wireOp",EDGE,"E1281.bottom")}),1.0]])]});
            var Q46;
            Q46=makeQuery(id+"F2.imprint","IMPRINT",FACE,{"disambiguationData":[TD([[makeQuery(id+"F2.imprint","IMPRINT",EDGE,{"derivedFrom":sQuery(id+"F2.wireOp",EDGE,"E639")}),-1.0]])]});
            var Q47;
            Q47=makeQuery(id+"F2.imprint","IMPRINT",FACE,{"disambiguationData":[TD([[makeQuery(id+"F2.imprint","IMPRINT",EDGE,{"derivedFrom":sQuery(id+"F2.wireOp",EDGE,"E1286")}),1.0]])]});
            extrude(context, id + "F3", {"entities" : qUnion([Q0, Q1, Q2, Q3, Q4, Q5, Q6, Q7, Q8, Q9, Q10, Q11, Q12, Q13, Q14, Q15, Q16, Q17, Q18, Q19, Q20, Q21, Q22, Q23, Q24, Q25, Q26, Q27, Q28, Q29, Q30, Q31, Q32, Q33, Q34, Q35, Q36, Q37, Q38, Q39, Q40, Q41, Q42, Q43, Q44, Q45, Q46, Q47]), "depth" : 12.7 * mm, "hasSecondDirection" : true, "secondDirectionOppositeDirection" : true, "secondDirectionDepth" : 12.7 * mm});
        }
    });
